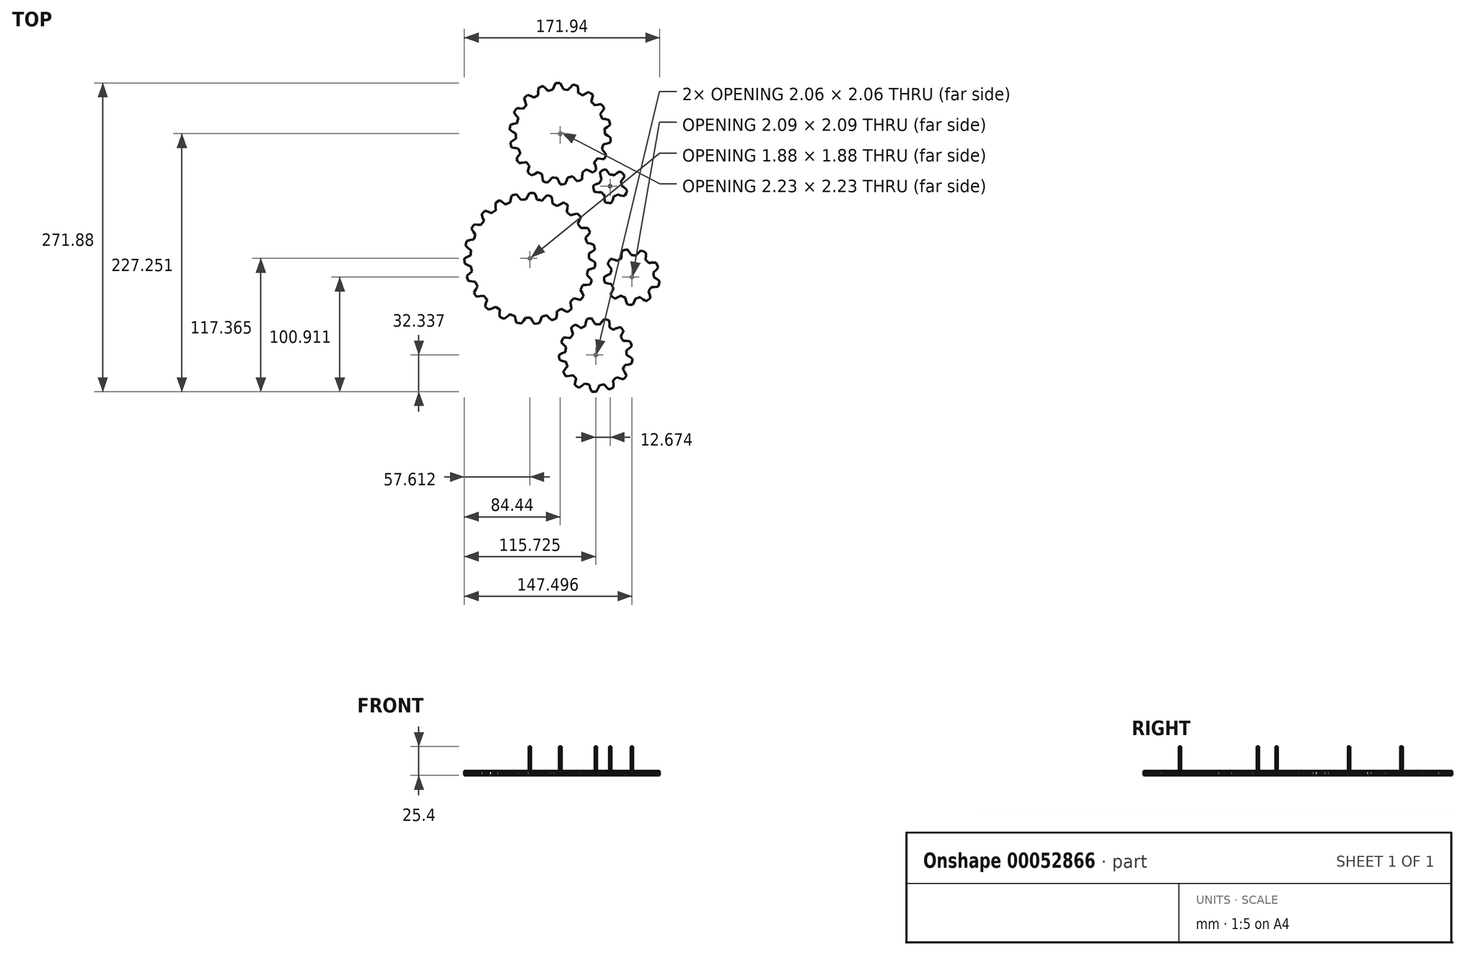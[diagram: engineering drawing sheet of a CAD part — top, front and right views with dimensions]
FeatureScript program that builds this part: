
annotation { "Feature Type Name" : "Feature", "Feature Type Description" : "" }
export const myFeature = defineFeature(function(context is Context, id is Id, definition is map)
    precondition{}
    {
        {
            var Q0;
            Q0=qCreatedBy(makeId("Top.planeOp"),FACE);
            var sketch = newSketch(context, id + "F0", { "sketchPlane" : qUnion([Q0])});
            skLineSegment(sketch, "E0", {"start": v(23.91, -18.64) * mm, "end": v(23.86, -16.49) * mm});
            skLineSegment(sketch, "E1", {"start": v(23.86, -16.49) * mm, "end": v(23.77, -15) * mm});
            skLineSegment(sketch, "E2", {"start": v(23.77, -15) * mm, "end": v(23.72, -14.33) * mm});
            skLineSegment(sketch, "E3", {"start": v(23.72, -14.33) * mm, "end": v(24.54, -13.82) * mm});
            skLineSegment(sketch, "E4", {"start": v(24.54, -13.82) * mm, "end": v(26.32, -12.65) * mm});
            skLineSegment(sketch, "E5", {"start": v(26.32, -12.65) * mm, "end": v(28.84, -10.83) * mm});
            skLineSegment(sketch, "E6", {"start": v(28.84, -10.83) * mm, "end": v(28.51, -8.7) * mm});
            skLineSegment(sketch, "E7", {"start": v(28.51, -8.7) * mm, "end": v(28.25, -7.25) * mm});
            skLineSegment(sketch, "E8", {"start": v(28.25, -7.25) * mm, "end": v(28.15, -6.77) * mm});
            skLineSegment(sketch, "E9", {"start": v(28.15, -6.77) * mm, "end": v(28.11, -6.6) * mm});
            skLineSegment(sketch, "E10", {"start": v(28.11, -6.6) * mm, "end": v(25.07, -5.56) * mm});
            skLineSegment(sketch, "E11", {"start": v(25.07, -5.56) * mm, "end": v(22.97, -4.95) * mm});
            skLineSegment(sketch, "E12", {"start": v(22.97, -4.95) * mm, "end": v(22.02, -4.7) * mm});
            skLineSegment(sketch, "E13", {"start": v(22.02, -4.7) * mm, "end": v(21.8, -3.9) * mm});
            skLineSegment(sketch, "E14", {"start": v(21.8, -3.9) * mm, "end": v(21.36, -2.5) * mm});
            skLineSegment(sketch, "E15", {"start": v(21.36, -2.5) * mm, "end": v(20.88, -1.09) * mm});
            skLineSegment(sketch, "E16", {"start": v(20.88, -1.09) * mm, "end": v(20.65, -0.46) * mm});
            skLineSegment(sketch, "E17", {"start": v(20.65, -0.46) * mm, "end": v(22.68, 1.86) * mm});
            skLineSegment(sketch, "E18", {"start": v(22.68, 1.86) * mm, "end": v(24.04, 3.53) * mm});
            skLineSegment(sketch, "E19", {"start": v(24.04, 3.53) * mm, "end": v(24.62, 4.3) * mm});
            skLineSegment(sketch, "E20", {"start": v(24.62, 4.3) * mm, "end": v(23.74, 6.27) * mm});
            skLineSegment(sketch, "E21", {"start": v(23.74, 6.27) * mm, "end": v(22.76, 8.18) * mm});
            skLineSegment(sketch, "E22", {"start": v(22.76, 8.18) * mm, "end": v(21.77, 8.26) * mm});
            skLineSegment(sketch, "E23", {"start": v(21.77, 8.26) * mm, "end": v(19.56, 8.35) * mm});
            skLineSegment(sketch, "E24", {"start": v(19.56, 8.35) * mm, "end": v(16.4, 8.36) * mm});
            skLineSegment(sketch, "E25", {"start": v(16.4, 8.36) * mm, "end": v(16.32, 8.48) * mm});
            skLineSegment(sketch, "E26", {"start": v(16.32, 8.48) * mm, "end": v(15.16, 10.3) * mm});
            skLineSegment(sketch, "E27", {"start": v(15.16, 10.3) * mm, "end": v(13.92, 12.06) * mm});
            skLineSegment(sketch, "E28", {"start": v(13.92, 12.06) * mm, "end": v(15.25, 14.85) * mm});
            skLineSegment(sketch, "E29", {"start": v(15.25, 14.85) * mm, "end": v(16.46, 17.73) * mm});
            skLineSegment(sketch, "E30", {"start": v(16.46, 17.73) * mm, "end": v(16.35, 17.87) * mm});
            skLineSegment(sketch, "E31", {"start": v(16.35, 17.87) * mm, "end": v(16.04, 18.25) * mm});
            skLineSegment(sketch, "E32", {"start": v(16.04, 18.25) * mm, "end": v(14.09, 20.47) * mm});
            skLineSegment(sketch, "E33", {"start": v(14.09, 20.47) * mm, "end": v(13.63, 20.95) * mm});
            skLineSegment(sketch, "E34", {"start": v(13.63, 20.95) * mm, "end": v(10.5, 20.26) * mm});
            skLineSegment(sketch, "E35", {"start": v(10.5, 20.26) * mm, "end": v(7.44, 19.4) * mm});
            skLineSegment(sketch, "E36", {"start": v(7.44, 19.4) * mm, "end": v(6.84, 19.97) * mm});
            skLineSegment(sketch, "E37", {"start": v(6.84, 19.97) * mm, "end": v(4.6, 21.9) * mm});
            skLineSegment(sketch, "E38", {"start": v(4.6, 21.9) * mm, "end": v(4.06, 22.31) * mm});
            skLineSegment(sketch, "E39", {"start": v(4.06, 22.31) * mm, "end": v(4.6, 25.37) * mm});
            skLineSegment(sketch, "E40", {"start": v(4.6, 25.37) * mm, "end": v(4.99, 28.45) * mm});
            skLineSegment(sketch, "E41", {"start": v(4.99, 28.45) * mm, "end": v(3.88, 29.23) * mm});
            skLineSegment(sketch, "E42", {"start": v(3.88, 29.23) * mm, "end": v(1.97, 30.46) * mm});
            skLineSegment(sketch, "E43", {"start": v(1.97, 30.46) * mm, "end": v(1.4, 30.8) * mm});
            skLineSegment(sketch, "E44", {"start": v(1.4, 30.8) * mm, "end": v(-1.44, 29.29) * mm});
            skLineSegment(sketch, "E45", {"start": v(-1.44, 29.29) * mm, "end": v(-3.31, 28.18) * mm});
            skLineSegment(sketch, "E46", {"start": v(-3.31, 28.18) * mm, "end": v(-4.15, 27.65) * mm});
            skLineSegment(sketch, "E47", {"start": v(-4.15, 27.65) * mm, "end": v(-4.88, 28.02) * mm});
            skLineSegment(sketch, "E48", {"start": v(-4.88, 28.02) * mm, "end": v(-6.21, 28.67) * mm});
            skLineSegment(sketch, "E49", {"start": v(-6.21, 28.67) * mm, "end": v(-8, 29.48) * mm});
            skLineSegment(sketch, "E50", {"start": v(-8, 29.48) * mm, "end": v(-8.18, 29.55) * mm});
            skLineSegment(sketch, "E51", {"start": v(-8.18, 29.55) * mm, "end": v(-8.5, 32.6) * mm});
            skLineSegment(sketch, "E52", {"start": v(-8.5, 32.6) * mm, "end": v(-8.78, 34.74) * mm});
            skLineSegment(sketch, "E53", {"start": v(-8.78, 34.74) * mm, "end": v(-8.95, 35.7) * mm});
            skLineSegment(sketch, "E54", {"start": v(-8.95, 35.7) * mm, "end": v(-10.98, 36.39) * mm});
            skLineSegment(sketch, "E55", {"start": v(-10.98, 36.39) * mm, "end": v(-13.05, 36.98) * mm});
            skLineSegment(sketch, "E56", {"start": v(-13.05, 36.98) * mm, "end": v(-15.36, 34.76) * mm});
            skLineSegment(sketch, "E57", {"start": v(-15.36, 34.76) * mm, "end": v(-17.53, 32.45) * mm});
            skLineSegment(sketch, "E58", {"start": v(-17.53, 32.45) * mm, "end": v(-17.67, 32.48) * mm});
            skLineSegment(sketch, "E59", {"start": v(-17.67, 32.48) * mm, "end": v(-17.85, 32.52) * mm});
            skLineSegment(sketch, "E60", {"start": v(-17.85, 32.52) * mm, "end": v(-19.79, 32.87) * mm});
            skLineSegment(sketch, "E61", {"start": v(-19.79, 32.87) * mm, "end": v(-21.26, 33.08) * mm});
            skLineSegment(sketch, "E62", {"start": v(-21.26, 33.08) * mm, "end": v(-21.92, 33.17) * mm});
            skLineSegment(sketch, "E63", {"start": v(-21.92, 33.17) * mm, "end": v(-22.26, 34.07) * mm});
            skLineSegment(sketch, "E64", {"start": v(-22.26, 34.07) * mm, "end": v(-23.05, 36.05) * mm});
            skLineSegment(sketch, "E65", {"start": v(-23.05, 36.05) * mm, "end": v(-24.33, 38.89) * mm});
            skLineSegment(sketch, "E66", {"start": v(-24.33, 38.89) * mm, "end": v(-26.47, 39) * mm});
            skLineSegment(sketch, "E67", {"start": v(-26.47, 39) * mm, "end": v(-27.95, 39.03) * mm});
            skLineSegment(sketch, "E68", {"start": v(-27.95, 39.03) * mm, "end": v(-28.62, 39.03) * mm});
            skLineSegment(sketch, "E69", {"start": v(-28.62, 39.03) * mm, "end": v(-30.25, 36.25) * mm});
            skLineSegment(sketch, "E70", {"start": v(-30.25, 36.25) * mm, "end": v(-31.72, 33.44) * mm});
            skLineSegment(sketch, "E71", {"start": v(-31.72, 33.44) * mm, "end": v(-34, 33.25) * mm});
            skLineSegment(sketch, "E72", {"start": v(-34, 33.25) * mm, "end": v(-36.15, 32.98) * mm});
            skLineSegment(sketch, "E73", {"start": v(-36.15, 32.98) * mm, "end": v(-36.71, 33.75) * mm});
            skLineSegment(sketch, "E74", {"start": v(-36.71, 33.75) * mm, "end": v(-38, 35.43) * mm});
            skLineSegment(sketch, "E75", {"start": v(-38, 35.43) * mm, "end": v(-39.36, 37.1) * mm});
            skLineSegment(sketch, "E76", {"start": v(-39.36, 37.1) * mm, "end": v(-40, 37.85) * mm});
            skLineSegment(sketch, "E77", {"start": v(-40, 37.85) * mm, "end": v(-42.1, 37.36) * mm});
            skLineSegment(sketch, "E78", {"start": v(-42.1, 37.36) * mm, "end": v(-43.52, 36.99) * mm});
            skLineSegment(sketch, "E79", {"start": v(-43.52, 36.99) * mm, "end": v(-44.17, 36.8) * mm});
            skLineSegment(sketch, "E80", {"start": v(-44.17, 36.8) * mm, "end": v(-44.44, 35.84) * mm});
            skLineSegment(sketch, "E81", {"start": v(-44.44, 35.84) * mm, "end": v(-45, 33.71) * mm});
            skLineSegment(sketch, "E82", {"start": v(-45, 33.71) * mm, "end": v(-45.64, 30.6) * mm});
            skLineSegment(sketch, "E83", {"start": v(-45.64, 30.6) * mm, "end": v(-45.96, 30.5) * mm});
            skLineSegment(sketch, "E84", {"start": v(-45.96, 30.5) * mm, "end": v(-46.42, 30.33) * mm});
            skLineSegment(sketch, "E85", {"start": v(-46.42, 30.33) * mm, "end": v(-48.53, 29.5) * mm});
            skLineSegment(sketch, "E86", {"start": v(-48.53, 29.5) * mm, "end": v(-49.78, 28.94) * mm});
            skLineSegment(sketch, "E87", {"start": v(-49.78, 28.94) * mm, "end": v(-50.53, 29.54) * mm});
            skLineSegment(sketch, "E88", {"start": v(-50.53, 29.54) * mm, "end": v(-52.24, 30.82) * mm});
            skLineSegment(sketch, "E89", {"start": v(-52.24, 30.82) * mm, "end": v(-54.8, 32.58) * mm});
            skLineSegment(sketch, "E90", {"start": v(-54.8, 32.58) * mm, "end": v(-55.4, 32.27) * mm});
            skLineSegment(sketch, "E91", {"start": v(-55.4, 32.27) * mm, "end": v(-57.97, 30.82) * mm});
            skLineSegment(sketch, "E92", {"start": v(-57.97, 30.82) * mm, "end": v(-58.39, 30.57) * mm});
            skLineSegment(sketch, "E93", {"start": v(-58.39, 30.57) * mm, "end": v(-58.54, 30.47) * mm});
            skLineSegment(sketch, "E94", {"start": v(-58.54, 30.47) * mm, "end": v(-58.5, 27.25) * mm});
            skLineSegment(sketch, "E95", {"start": v(-58.5, 27.25) * mm, "end": v(-58.44, 26.1) * mm});
            skLineSegment(sketch, "E96", {"start": v(-58.44, 26.1) * mm, "end": v(-58.28, 24.09) * mm});
            skLineSegment(sketch, "E97", {"start": v(-58.28, 24.09) * mm, "end": v(-59.5, 23.21) * mm});
            skLineSegment(sketch, "E98", {"start": v(-59.5, 23.21) * mm, "end": v(-61.3, 21.8) * mm});
            skLineSegment(sketch, "E99", {"start": v(-61.3, 21.8) * mm, "end": v(-61.67, 21.5) * mm});
            skLineSegment(sketch, "E100", {"start": v(-61.67, 21.5) * mm, "end": v(-61.81, 21.38) * mm});
            skLineSegment(sketch, "E101", {"start": v(-61.81, 21.38) * mm, "end": v(-64.68, 22.51) * mm});
            skLineSegment(sketch, "E102", {"start": v(-64.68, 22.51) * mm, "end": v(-67.63, 23.52) * mm});
            skLineSegment(sketch, "E103", {"start": v(-67.63, 23.52) * mm, "end": v(-69.18, 22.04) * mm});
            skLineSegment(sketch, "E104", {"start": v(-69.18, 22.04) * mm, "end": v(-70.66, 20.48) * mm});
            skLineSegment(sketch, "E105", {"start": v(-70.66, 20.48) * mm, "end": v(-70.4, 19.52) * mm});
            skLineSegment(sketch, "E106", {"start": v(-70.4, 19.52) * mm, "end": v(-69.75, 17.4) * mm});
            skLineSegment(sketch, "E107", {"start": v(-69.75, 17.4) * mm, "end": v(-69.05, 15.34) * mm});
            skLineSegment(sketch, "E108", {"start": v(-69.05, 15.34) * mm, "end": v(-68.7, 14.42) * mm});
            skLineSegment(sketch, "E109", {"start": v(-68.7, 14.42) * mm, "end": v(-70.13, 12.6) * mm});
            skLineSegment(sketch, "E110", {"start": v(-70.13, 12.6) * mm, "end": v(-71.38, 10.85) * mm});
            skLineSegment(sketch, "E111", {"start": v(-71.38, 10.85) * mm, "end": v(-72.34, 10.97) * mm});
            skLineSegment(sketch, "E112", {"start": v(-72.34, 10.97) * mm, "end": v(-74.44, 11.17) * mm});
            skLineSegment(sketch, "E113", {"start": v(-74.44, 11.17) * mm, "end": v(-77.57, 11.36) * mm});
            skLineSegment(sketch, "E114", {"start": v(-77.57, 11.36) * mm, "end": v(-77.66, 11.2) * mm});
            skLineSegment(sketch, "E115", {"start": v(-77.66, 11.2) * mm, "end": v(-79.03, 8.81) * mm});
            skLineSegment(sketch, "E116", {"start": v(-79.03, 8.81) * mm, "end": v(-79.65, 7.6) * mm});
            skLineSegment(sketch, "E117", {"start": v(-79.65, 7.6) * mm, "end": v(-79.13, 6.74) * mm});
            skLineSegment(sketch, "E118", {"start": v(-79.13, 6.74) * mm, "end": v(-77.96, 4.89) * mm});
            skLineSegment(sketch, "E119", {"start": v(-77.96, 4.89) * mm, "end": v(-76.13, 2.29) * mm});
            skLineSegment(sketch, "E120", {"start": v(-76.13, 2.29) * mm, "end": v(-76.46, 1.54) * mm});
            skLineSegment(sketch, "E121", {"start": v(-76.46, 1.54) * mm, "end": v(-77, 0.16) * mm});
            skLineSegment(sketch, "E122", {"start": v(-77, 0.16) * mm, "end": v(-77.52, -1.23) * mm});
            skLineSegment(sketch, "E123", {"start": v(-77.52, -1.23) * mm, "end": v(-77.74, -1.86) * mm});
            skLineSegment(sketch, "E124", {"start": v(-77.74, -1.86) * mm, "end": v(-80.8, -2.38) * mm});
            skLineSegment(sketch, "E125", {"start": v(-80.8, -2.38) * mm, "end": v(-83.83, -3.05) * mm});
            skLineSegment(sketch, "E126", {"start": v(-83.83, -3.05) * mm, "end": v(-84, -3.7) * mm});
            skLineSegment(sketch, "E127", {"start": v(-84, -3.7) * mm, "end": v(-84.37, -5.13) * mm});
            skLineSegment(sketch, "E128", {"start": v(-84.37, -5.13) * mm, "end": v(-84.8, -7.04) * mm});
            skLineSegment(sketch, "E129", {"start": v(-84.8, -7.04) * mm, "end": v(-84.84, -7.23) * mm});
            skLineSegment(sketch, "E130", {"start": v(-84.84, -7.23) * mm, "end": v(-82.45, -9.38) * mm});
            skLineSegment(sketch, "E131", {"start": v(-82.45, -9.38) * mm, "end": v(-80, -11.39) * mm});
            skLineSegment(sketch, "E132", {"start": v(-80, -11.39) * mm, "end": v(-80.27, -13.67) * mm});
            skLineSegment(sketch, "E133", {"start": v(-80.27, -13.67) * mm, "end": v(-80.43, -15.82) * mm});
            skLineSegment(sketch, "E134", {"start": v(-80.43, -15.82) * mm, "end": v(-81.3, -16.22) * mm});
            skLineSegment(sketch, "E135", {"start": v(-81.3, -16.22) * mm, "end": v(-83.2, -17.14) * mm});
            skLineSegment(sketch, "E136", {"start": v(-83.2, -17.14) * mm, "end": v(-85.97, -18.61) * mm});
            skLineSegment(sketch, "E137", {"start": v(-85.97, -18.61) * mm, "end": v(-85.9, -21.54) * mm});
            skLineSegment(sketch, "E138", {"start": v(-85.9, -21.54) * mm, "end": v(-85.8, -22.9) * mm});
            skLineSegment(sketch, "E139", {"start": v(-85.8, -22.9) * mm, "end": v(-82.95, -24.34) * mm});
            skLineSegment(sketch, "E140", {"start": v(-82.95, -24.34) * mm, "end": v(-80.03, -25.61) * mm});
            skLineSegment(sketch, "E141", {"start": v(-80.03, -25.61) * mm, "end": v(-79.93, -26.42) * mm});
            skLineSegment(sketch, "E142", {"start": v(-79.93, -26.42) * mm, "end": v(-79.4, -29.34) * mm});
            skLineSegment(sketch, "E143", {"start": v(-79.4, -29.34) * mm, "end": v(-79.25, -30) * mm});
            skLineSegment(sketch, "E144", {"start": v(-79.25, -30) * mm, "end": v(-81.6, -32.02) * mm});
            skLineSegment(sketch, "E145", {"start": v(-81.6, -32.02) * mm, "end": v(-83.15, -33.49) * mm});
            skLineSegment(sketch, "E146", {"start": v(-83.15, -33.49) * mm, "end": v(-83.84, -34.17) * mm});
            skLineSegment(sketch, "E147", {"start": v(-83.84, -34.17) * mm, "end": v(-83.23, -36.23) * mm});
            skLineSegment(sketch, "E148", {"start": v(-83.23, -36.23) * mm, "end": v(-82.55, -38.27) * mm});
            skLineSegment(sketch, "E149", {"start": v(-82.55, -38.27) * mm, "end": v(-81.56, -38.47) * mm});
            skLineSegment(sketch, "E150", {"start": v(-81.56, -38.47) * mm, "end": v(-79.38, -38.87) * mm});
            skLineSegment(sketch, "E151", {"start": v(-79.38, -38.87) * mm, "end": v(-77.23, -39.2) * mm});
            skLineSegment(sketch, "E152", {"start": v(-77.23, -39.2) * mm, "end": v(-76.25, -39.31) * mm});
            skLineSegment(sketch, "E153", {"start": v(-76.25, -39.31) * mm, "end": v(-75.3, -41.4) * mm});
            skLineSegment(sketch, "E154", {"start": v(-75.3, -41.4) * mm, "end": v(-74.31, -43.32) * mm});
            skLineSegment(sketch, "E155", {"start": v(-74.31, -43.32) * mm, "end": v(-74.85, -44.12) * mm});
            skLineSegment(sketch, "E156", {"start": v(-74.85, -44.12) * mm, "end": v(-76, -45.9) * mm});
            skLineSegment(sketch, "E157", {"start": v(-76, -45.9) * mm, "end": v(-77.6, -48.59) * mm});
            skLineSegment(sketch, "E158", {"start": v(-77.6, -48.59) * mm, "end": v(-76.44, -50.4) * mm});
            skLineSegment(sketch, "E159", {"start": v(-76.44, -50.4) * mm, "end": v(-75.61, -51.62) * mm});
            skLineSegment(sketch, "E160", {"start": v(-75.61, -51.62) * mm, "end": v(-75.22, -52.16) * mm});
            skLineSegment(sketch, "E161", {"start": v(-75.22, -52.16) * mm, "end": v(-74.22, -52.1) * mm});
            skLineSegment(sketch, "E162", {"start": v(-74.22, -52.1) * mm, "end": v(-72.03, -51.9) * mm});
            skLineSegment(sketch, "E163", {"start": v(-72.03, -51.9) * mm, "end": v(-68.88, -51.47) * mm});
            skLineSegment(sketch, "E164", {"start": v(-68.88, -51.47) * mm, "end": v(-68.8, -51.59) * mm});
            skLineSegment(sketch, "E165", {"start": v(-68.8, -51.59) * mm, "end": v(-68.37, -52.1) * mm});
            skLineSegment(sketch, "E166", {"start": v(-68.37, -52.1) * mm, "end": v(-66.87, -53.82) * mm});
            skLineSegment(sketch, "E167", {"start": v(-66.87, -53.82) * mm, "end": v(-65.93, -54.81) * mm});
            skLineSegment(sketch, "E168", {"start": v(-65.93, -54.81) * mm, "end": v(-66.24, -55.72) * mm});
            skLineSegment(sketch, "E169", {"start": v(-66.24, -55.72) * mm, "end": v(-66.88, -57.76) * mm});
            skLineSegment(sketch, "E170", {"start": v(-66.88, -57.76) * mm, "end": v(-67.68, -60.76) * mm});
            skLineSegment(sketch, "E171", {"start": v(-67.68, -60.76) * mm, "end": v(-67.2, -61.23) * mm});
            skLineSegment(sketch, "E172", {"start": v(-67.2, -61.23) * mm, "end": v(-64.97, -63.17) * mm});
            skLineSegment(sketch, "E173", {"start": v(-64.97, -63.17) * mm, "end": v(-64.44, -63.58) * mm});
            skLineSegment(sketch, "E174", {"start": v(-64.44, -63.58) * mm, "end": v(-61.43, -62.47) * mm});
            skLineSegment(sketch, "E175", {"start": v(-61.43, -62.47) * mm, "end": v(-59.41, -61.62) * mm});
            skLineSegment(sketch, "E176", {"start": v(-59.41, -61.62) * mm, "end": v(-58.51, -61.2) * mm});
            skLineSegment(sketch, "E177", {"start": v(-58.51, -61.2) * mm, "end": v(-57.85, -61.68) * mm});
            skLineSegment(sketch, "E178", {"start": v(-57.85, -61.68) * mm, "end": v(-55.36, -63.3) * mm});
            skLineSegment(sketch, "E179", {"start": v(-55.36, -63.3) * mm, "end": v(-54.78, -63.63) * mm});
            skLineSegment(sketch, "E180", {"start": v(-54.78, -63.63) * mm, "end": v(-54.9, -66.72) * mm});
            skLineSegment(sketch, "E181", {"start": v(-54.9, -66.72) * mm, "end": v(-54.89, -68.86) * mm});
            skLineSegment(sketch, "E182", {"start": v(-54.89, -68.86) * mm, "end": v(-54.86, -69.84) * mm});
            skLineSegment(sketch, "E183", {"start": v(-54.86, -69.84) * mm, "end": v(-52.94, -70.8) * mm});
            skLineSegment(sketch, "E184", {"start": v(-52.94, -70.8) * mm, "end": v(-50.98, -71.68) * mm});
            skLineSegment(sketch, "E185", {"start": v(-50.98, -71.68) * mm, "end": v(-50.16, -71.1) * mm});
            skLineSegment(sketch, "E186", {"start": v(-50.16, -71.1) * mm, "end": v(-48.38, -69.78) * mm});
            skLineSegment(sketch, "E187", {"start": v(-48.38, -69.78) * mm, "end": v(-46.68, -68.44) * mm});
            skLineSegment(sketch, "E188", {"start": v(-46.68, -68.44) * mm, "end": v(-45.92, -67.8) * mm});
            skLineSegment(sketch, "E189", {"start": v(-45.92, -67.8) * mm, "end": v(-43.74, -68.53) * mm});
            skLineSegment(sketch, "E190", {"start": v(-43.74, -68.53) * mm, "end": v(-41.67, -69.12) * mm});
            skLineSegment(sketch, "E191", {"start": v(-41.67, -69.12) * mm, "end": v(-41.46, -70.06) * mm});
            skLineSegment(sketch, "E192", {"start": v(-41.46, -70.06) * mm, "end": v(-40.94, -72.11) * mm});
            skLineSegment(sketch, "E193", {"start": v(-40.94, -72.11) * mm, "end": v(-40.06, -75.12) * mm});
            skLineSegment(sketch, "E194", {"start": v(-40.06, -75.12) * mm, "end": v(-39.88, -75.16) * mm});
            skLineSegment(sketch, "E195", {"start": v(-39.88, -75.16) * mm, "end": v(-37.17, -75.64) * mm});
            skLineSegment(sketch, "E196", {"start": v(-37.17, -75.64) * mm, "end": v(-35.83, -75.82) * mm});
            skLineSegment(sketch, "E197", {"start": v(-35.83, -75.82) * mm, "end": v(-33.84, -73.31) * mm});
            skLineSegment(sketch, "E198", {"start": v(-33.84, -73.31) * mm, "end": v(-32, -70.7) * mm});
            skLineSegment(sketch, "E199", {"start": v(-32, -70.7) * mm, "end": v(-31.19, -70.77) * mm});
            skLineSegment(sketch, "E200", {"start": v(-31.19, -70.77) * mm, "end": v(-28.22, -70.85) * mm});
            skLineSegment(sketch, "E201", {"start": v(-28.22, -70.85) * mm, "end": v(-27.55, -70.83) * mm});
            skLineSegment(sketch, "E202", {"start": v(-27.55, -70.83) * mm, "end": v(-26.04, -73.53) * mm});
            skLineSegment(sketch, "E203", {"start": v(-26.04, -73.53) * mm, "end": v(-24.93, -75.36) * mm});
            skLineSegment(sketch, "E204", {"start": v(-24.93, -75.36) * mm, "end": v(-24.4, -76.18) * mm});
            skLineSegment(sketch, "E205", {"start": v(-24.4, -76.18) * mm, "end": v(-22.26, -76) * mm});
            skLineSegment(sketch, "E206", {"start": v(-22.26, -76) * mm, "end": v(-20.13, -75.74) * mm});
            skLineSegment(sketch, "E207", {"start": v(-20.13, -75.74) * mm, "end": v(-19.72, -74.82) * mm});
            skLineSegment(sketch, "E208", {"start": v(-19.72, -74.82) * mm, "end": v(-18.88, -72.77) * mm});
            skLineSegment(sketch, "E209", {"start": v(-18.88, -72.77) * mm, "end": v(-17.81, -69.8) * mm});
            skLineSegment(sketch, "E210", {"start": v(-17.81, -69.8) * mm, "end": v(-15.57, -69.29) * mm});
            skLineSegment(sketch, "E211", {"start": v(-15.57, -69.29) * mm, "end": v(-13.5, -68.71) * mm});
            skLineSegment(sketch, "E212", {"start": v(-13.5, -68.71) * mm, "end": v(-12.82, -69.41) * mm});
            skLineSegment(sketch, "E213", {"start": v(-12.82, -69.41) * mm, "end": v(-11.32, -70.9) * mm});
            skLineSegment(sketch, "E214", {"start": v(-11.32, -70.9) * mm, "end": v(-9.01, -73) * mm});
            skLineSegment(sketch, "E215", {"start": v(-9.01, -73) * mm, "end": v(-8.38, -72.79) * mm});
            skLineSegment(sketch, "E216", {"start": v(-8.38, -72.79) * mm, "end": v(-5.63, -71.7) * mm});
            skLineSegment(sketch, "E217", {"start": v(-5.63, -71.7) * mm, "end": v(-5.02, -71.42) * mm});
            skLineSegment(sketch, "E218", {"start": v(-5.02, -71.42) * mm, "end": v(-4.63, -68.24) * mm});
            skLineSegment(sketch, "E219", {"start": v(-4.63, -68.24) * mm, "end": v(-4.46, -66.05) * mm});
            skLineSegment(sketch, "E220", {"start": v(-4.46, -66.05) * mm, "end": v(-4.4, -65.06) * mm});
            skLineSegment(sketch, "E221", {"start": v(-4.4, -65.06) * mm, "end": v(-4.28, -65) * mm});
            skLineSegment(sketch, "E222", {"start": v(-4.28, -65) * mm, "end": v(-2.39, -63.97) * mm});
            skLineSegment(sketch, "E223", {"start": v(-2.39, -63.97) * mm, "end": v(-1.1, -63.22) * mm});
            skLineSegment(sketch, "E224", {"start": v(-1.1, -63.22) * mm, "end": v(-0.54, -62.86) * mm});
            skLineSegment(sketch, "E225", {"start": v(-0.54, -62.86) * mm, "end": v(2.15, -64.38) * mm});
            skLineSegment(sketch, "E226", {"start": v(2.15, -64.38) * mm, "end": v(4.05, -65.35) * mm});
            skLineSegment(sketch, "E227", {"start": v(4.05, -65.35) * mm, "end": v(4.93, -65.78) * mm});
            skLineSegment(sketch, "E228", {"start": v(4.93, -65.78) * mm, "end": v(5.48, -65.39) * mm});
            skLineSegment(sketch, "E229", {"start": v(5.48, -65.39) * mm, "end": v(6.67, -64.5) * mm});
            skLineSegment(sketch, "E230", {"start": v(6.67, -64.5) * mm, "end": v(8.36, -63.18) * mm});
            skLineSegment(sketch, "E231", {"start": v(8.36, -63.18) * mm, "end": v(8.22, -62.18) * mm});
            skLineSegment(sketch, "E232", {"start": v(8.22, -62.18) * mm, "end": v(7.86, -60) * mm});
            skLineSegment(sketch, "E233", {"start": v(7.86, -60) * mm, "end": v(7.45, -57.86) * mm});
            skLineSegment(sketch, "E234", {"start": v(7.45, -57.86) * mm, "end": v(7.23, -56.9) * mm});
            skLineSegment(sketch, "E235", {"start": v(7.23, -56.9) * mm, "end": v(8.88, -55.3) * mm});
            skLineSegment(sketch, "E236", {"start": v(8.88, -55.3) * mm, "end": v(10.37, -53.73) * mm});
            skLineSegment(sketch, "E237", {"start": v(10.37, -53.73) * mm, "end": v(13.35, -54.46) * mm});
            skLineSegment(sketch, "E238", {"start": v(13.35, -54.46) * mm, "end": v(15.46, -54.9) * mm});
            skLineSegment(sketch, "E239", {"start": v(15.46, -54.9) * mm, "end": v(16.42, -55.07) * mm});
            skLineSegment(sketch, "E240", {"start": v(16.42, -55.07) * mm, "end": v(17.75, -53.38) * mm});
            skLineSegment(sketch, "E241", {"start": v(17.75, -53.38) * mm, "end": v(19, -51.64) * mm});
            skLineSegment(sketch, "E242", {"start": v(19, -51.64) * mm, "end": v(18.61, -50.71) * mm});
            skLineSegment(sketch, "E243", {"start": v(18.61, -50.71) * mm, "end": v(17.68, -48.7) * mm});
            skLineSegment(sketch, "E244", {"start": v(17.68, -48.7) * mm, "end": v(16.24, -45.9) * mm});
            skLineSegment(sketch, "E245", {"start": v(16.24, -45.9) * mm, "end": v(16.32, -45.77) * mm});
            skLineSegment(sketch, "E246", {"start": v(16.32, -45.77) * mm, "end": v(17.4, -43.9) * mm});
            skLineSegment(sketch, "E247", {"start": v(17.4, -43.9) * mm, "end": v(18.4, -42) * mm});
            skLineSegment(sketch, "E248", {"start": v(18.4, -42) * mm, "end": v(19.36, -41.98) * mm});
            skLineSegment(sketch, "E249", {"start": v(19.36, -41.98) * mm, "end": v(21.49, -41.9) * mm});
            skLineSegment(sketch, "E250", {"start": v(21.49, -41.9) * mm, "end": v(24.6, -41.66) * mm});
            skLineSegment(sketch, "E251", {"start": v(24.6, -41.66) * mm, "end": v(24.87, -41.04) * mm});
            skLineSegment(sketch, "E252", {"start": v(24.87, -41.04) * mm, "end": v(25.94, -38.3) * mm});
            skLineSegment(sketch, "E253", {"start": v(25.94, -38.3) * mm, "end": v(26.16, -37.65) * mm});
            skLineSegment(sketch, "E254", {"start": v(26.16, -37.65) * mm, "end": v(24.1, -35.2) * mm});
            skLineSegment(sketch, "E255", {"start": v(24.1, -35.2) * mm, "end": v(22.62, -33.58) * mm});
            skLineSegment(sketch, "E256", {"start": v(22.62, -33.58) * mm, "end": v(21.94, -32.87) * mm});
            skLineSegment(sketch, "E257", {"start": v(21.94, -32.87) * mm, "end": v(22.16, -32.08) * mm});
            skLineSegment(sketch, "E258", {"start": v(22.16, -32.08) * mm, "end": v(22.85, -29.2) * mm});
            skLineSegment(sketch, "E259", {"start": v(22.85, -29.2) * mm, "end": v(22.97, -28.54) * mm});
            skLineSegment(sketch, "E260", {"start": v(22.97, -28.54) * mm, "end": v(25.9, -27.6) * mm});
            skLineSegment(sketch, "E261", {"start": v(25.9, -27.6) * mm, "end": v(27.93, -26.88) * mm});
            skLineSegment(sketch, "E262", {"start": v(27.93, -26.88) * mm, "end": v(28.83, -26.53) * mm});
            skLineSegment(sketch, "E263", {"start": v(28.83, -26.53) * mm, "end": v(29.1, -24.4) * mm});
            skLineSegment(sketch, "E264", {"start": v(29.1, -24.4) * mm, "end": v(29.26, -22.25) * mm});
            skLineSegment(sketch, "E265", {"start": v(29.26, -22.25) * mm, "end": v(28.45, -21.67) * mm});
            skLineSegment(sketch, "E266", {"start": v(28.45, -21.67) * mm, "end": v(26.6, -20.44) * mm});
            skLineSegment(sketch, "E267", {"start": v(26.6, -20.44) * mm, "end": v(23.91, -18.79) * mm});
            skLineSegment(sketch, "E268", {"start": v(23.91, -18.79) * mm, "end": v(23.91, -18.64) * mm});
            skLineSegment(sketch, "E269", {"start": v(-40.68, 91.45) * mm, "end": v(-43.38, 93.06) * mm});
            skLineSegment(sketch, "E270", {"start": v(-43.38, 93.06) * mm, "end": v(-45.2, 94.29) * mm});
            skLineSegment(sketch, "E271", {"start": v(-45.2, 94.29) * mm, "end": v(-46, 94.88) * mm});
            skLineSegment(sketch, "E272", {"start": v(-46, 94.88) * mm, "end": v(-45.78, 96.99) * mm});
            skLineSegment(sketch, "E273", {"start": v(-45.78, 96.99) * mm, "end": v(-45.47, 99.09) * mm});
            skLineSegment(sketch, "E274", {"start": v(-45.47, 99.09) * mm, "end": v(-44.54, 99.4) * mm});
            skLineSegment(sketch, "E275", {"start": v(-44.54, 99.4) * mm, "end": v(-42.5, 100.02) * mm});
            skLineSegment(sketch, "E276", {"start": v(-42.5, 100.02) * mm, "end": v(-39.53, 100.76) * mm});
            skLineSegment(sketch, "E277", {"start": v(-39.53, 100.76) * mm, "end": v(-39.5, 100.93) * mm});
            skLineSegment(sketch, "E278", {"start": v(-39.5, 100.93) * mm, "end": v(-39.37, 101.38) * mm});
            skLineSegment(sketch, "E279", {"start": v(-39.37, 101.38) * mm, "end": v(-38.99, 102.75) * mm});
            skLineSegment(sketch, "E280", {"start": v(-38.99, 102.75) * mm, "end": v(-38.34, 104.7) * mm});
            skLineSegment(sketch, "E281", {"start": v(-38.34, 104.7) * mm, "end": v(-38.29, 104.84) * mm});
            skLineSegment(sketch, "E282", {"start": v(-38.29, 104.84) * mm, "end": v(-40.27, 107.27) * mm});
            skLineSegment(sketch, "E283", {"start": v(-40.27, 107.27) * mm, "end": v(-41.55, 109.05) * mm});
            skLineSegment(sketch, "E284", {"start": v(-41.55, 109.05) * mm, "end": v(-42.1, 109.88) * mm});
            skLineSegment(sketch, "E285", {"start": v(-42.1, 109.88) * mm, "end": v(-41.83, 110.49) * mm});
            skLineSegment(sketch, "E286", {"start": v(-41.83, 110.49) * mm, "end": v(-41.18, 111.79) * mm});
            skLineSegment(sketch, "E287", {"start": v(-41.18, 111.79) * mm, "end": v(-40.49, 113.08) * mm});
            skLineSegment(sketch, "E288", {"start": v(-40.49, 113.08) * mm, "end": v(-40.16, 113.65) * mm});
            skLineSegment(sketch, "E289", {"start": v(-40.16, 113.65) * mm, "end": v(-39.18, 113.63) * mm});
            skLineSegment(sketch, "E290", {"start": v(-39.18, 113.63) * mm, "end": v(-37.05, 113.5) * mm});
            skLineSegment(sketch, "E291", {"start": v(-37.05, 113.5) * mm, "end": v(-34.02, 113.18) * mm});
            skLineSegment(sketch, "E292", {"start": v(-34.02, 113.18) * mm, "end": v(-32.81, 114.86) * mm});
            skLineSegment(sketch, "E293", {"start": v(-32.81, 114.86) * mm, "end": v(-31.64, 116.34) * mm});
            skLineSegment(sketch, "E294", {"start": v(-31.64, 116.34) * mm, "end": v(-31.43, 116.58) * mm});
            skLineSegment(sketch, "E295", {"start": v(-31.43, 116.58) * mm, "end": v(-32.47, 119.56) * mm});
            skLineSegment(sketch, "E296", {"start": v(-32.47, 119.56) * mm, "end": v(-33.3, 122.64) * mm});
            skLineSegment(sketch, "E297", {"start": v(-33.3, 122.64) * mm, "end": v(-32.84, 123.1) * mm});
            skLineSegment(sketch, "E298", {"start": v(-32.84, 123.1) * mm, "end": v(-31.78, 124.11) * mm});
            skLineSegment(sketch, "E299", {"start": v(-31.78, 124.11) * mm, "end": v(-30.19, 125.51) * mm});
            skLineSegment(sketch, "E300", {"start": v(-30.19, 125.51) * mm, "end": v(-29.28, 125.16) * mm});
            skLineSegment(sketch, "E301", {"start": v(-29.28, 125.16) * mm, "end": v(-27.32, 124.31) * mm});
            skLineSegment(sketch, "E302", {"start": v(-27.32, 124.31) * mm, "end": v(-25.42, 123.41) * mm});
            skLineSegment(sketch, "E303", {"start": v(-25.42, 123.41) * mm, "end": v(-24.57, 122.97) * mm});
            skLineSegment(sketch, "E304", {"start": v(-24.57, 122.97) * mm, "end": v(-23.5, 123.73) * mm});
            skLineSegment(sketch, "E305", {"start": v(-23.5, 123.73) * mm, "end": v(-21.66, 124.9) * mm});
            skLineSegment(sketch, "E306", {"start": v(-21.66, 124.9) * mm, "end": v(-20.98, 125.29) * mm});
            skLineSegment(sketch, "E307", {"start": v(-20.98, 125.29) * mm, "end": v(-21, 126.27) * mm});
            skLineSegment(sketch, "E308", {"start": v(-21, 126.27) * mm, "end": v(-20.98, 127.28) * mm});
            skLineSegment(sketch, "E309", {"start": v(-20.98, 127.28) * mm, "end": v(-20.94, 128.43) * mm});
            skLineSegment(sketch, "E310", {"start": v(-20.94, 128.43) * mm, "end": v(-20.79, 130.62) * mm});
            skLineSegment(sketch, "E311", {"start": v(-20.79, 130.62) * mm, "end": v(-20.68, 131.62) * mm});
            skLineSegment(sketch, "E312", {"start": v(-20.68, 131.62) * mm, "end": v(-18.74, 132.5) * mm});
            skLineSegment(sketch, "E313", {"start": v(-18.74, 132.5) * mm, "end": v(-16.94, 133.2) * mm});
            skLineSegment(sketch, "E314", {"start": v(-16.94, 133.2) * mm, "end": v(-16.76, 133.27) * mm});
            skLineSegment(sketch, "E315", {"start": v(-16.76, 133.27) * mm, "end": v(-14.48, 131.15) * mm});
            skLineSegment(sketch, "E316", {"start": v(-14.48, 131.15) * mm, "end": v(-13.68, 130.36) * mm});
            skLineSegment(sketch, "E317", {"start": v(-13.68, 130.36) * mm, "end": v(-12.35, 128.94) * mm});
            skLineSegment(sketch, "E318", {"start": v(-12.35, 128.94) * mm, "end": v(-11.73, 129.12) * mm});
            skLineSegment(sketch, "E319", {"start": v(-11.73, 129.12) * mm, "end": v(-10.36, 129.46) * mm});
            skLineSegment(sketch, "E320", {"start": v(-10.36, 129.46) * mm, "end": v(-8.97, 129.75) * mm});
            skLineSegment(sketch, "E321", {"start": v(-8.97, 129.75) * mm, "end": v(-8.2, 129.9) * mm});
            skLineSegment(sketch, "E322", {"start": v(-8.2, 129.9) * mm, "end": v(-7.07, 132.83) * mm});
            skLineSegment(sketch, "E323", {"start": v(-7.07, 132.83) * mm, "end": v(-6.18, 134.83) * mm});
            skLineSegment(sketch, "E324", {"start": v(-6.18, 134.83) * mm, "end": v(-5.73, 135.73) * mm});
            skLineSegment(sketch, "E325", {"start": v(-5.73, 135.73) * mm, "end": v(-3.62, 135.88) * mm});
            skLineSegment(sketch, "E326", {"start": v(-3.62, 135.88) * mm, "end": v(-1.5, 135.94) * mm});
            skLineSegment(sketch, "E327", {"start": v(-1.5, 135.94) * mm, "end": v(-0.07, 133.17) * mm});
            skLineSegment(sketch, "E328", {"start": v(-0.07, 133.17) * mm, "end": v(0.8, 131.25) * mm});
            skLineSegment(sketch, "E329", {"start": v(0.8, 131.25) * mm, "end": v(1.17, 130.37) * mm});
            skLineSegment(sketch, "E330", {"start": v(1.17, 130.37) * mm, "end": v(2.48, 130.27) * mm});
            skLineSegment(sketch, "E331", {"start": v(2.48, 130.27) * mm, "end": v(4.64, 129.98) * mm});
            skLineSegment(sketch, "E332", {"start": v(4.64, 129.98) * mm, "end": v(5.4, 129.84) * mm});
            skLineSegment(sketch, "E333", {"start": v(5.4, 129.84) * mm, "end": v(6.03, 130.6) * mm});
            skLineSegment(sketch, "E334", {"start": v(6.03, 130.6) * mm, "end": v(6.69, 131.37) * mm});
            skLineSegment(sketch, "E335", {"start": v(6.69, 131.37) * mm, "end": v(7.46, 132.22) * mm});
            skLineSegment(sketch, "E336", {"start": v(7.46, 132.22) * mm, "end": v(8.99, 133.8) * mm});
            skLineSegment(sketch, "E337", {"start": v(8.99, 133.8) * mm, "end": v(9.71, 134.5) * mm});
            skLineSegment(sketch, "E338", {"start": v(9.71, 134.5) * mm, "end": v(11.76, 133.93) * mm});
            skLineSegment(sketch, "E339", {"start": v(11.76, 133.93) * mm, "end": v(13.77, 133.24) * mm});
            skLineSegment(sketch, "E340", {"start": v(13.77, 133.24) * mm, "end": v(13.91, 132.27) * mm});
            skLineSegment(sketch, "E341", {"start": v(13.91, 132.27) * mm, "end": v(14.16, 130.15) * mm});
            skLineSegment(sketch, "E342", {"start": v(14.16, 130.15) * mm, "end": v(14.33, 128.05) * mm});
            skLineSegment(sketch, "E343", {"start": v(14.33, 128.05) * mm, "end": v(14.37, 127.1) * mm});
            skLineSegment(sketch, "E344", {"start": v(14.37, 127.1) * mm, "end": v(14.95, 126.83) * mm});
            skLineSegment(sketch, "E345", {"start": v(14.95, 126.83) * mm, "end": v(16.23, 126.2) * mm});
            skLineSegment(sketch, "E346", {"start": v(16.23, 126.2) * mm, "end": v(17.48, 125.54) * mm});
            skLineSegment(sketch, "E347", {"start": v(17.48, 125.54) * mm, "end": v(18.16, 125.15) * mm});
            skLineSegment(sketch, "E348", {"start": v(18.16, 125.15) * mm, "end": v(20.91, 126.68) * mm});
            skLineSegment(sketch, "E349", {"start": v(20.91, 126.68) * mm, "end": v(22.89, 127.64) * mm});
            skLineSegment(sketch, "E350", {"start": v(22.89, 127.64) * mm, "end": v(23.8, 128.04) * mm});
            skLineSegment(sketch, "E351", {"start": v(23.8, 128.04) * mm, "end": v(25.52, 126.8) * mm});
            skLineSegment(sketch, "E352", {"start": v(25.52, 126.8) * mm, "end": v(26.67, 125.9) * mm});
            skLineSegment(sketch, "E353", {"start": v(26.67, 125.9) * mm, "end": v(27.04, 125.59) * mm});
            skLineSegment(sketch, "E354", {"start": v(27.04, 125.59) * mm, "end": v(27.18, 125.47) * mm});
            skLineSegment(sketch, "E355", {"start": v(27.18, 125.47) * mm, "end": v(26.5, 122.44) * mm});
            skLineSegment(sketch, "E356", {"start": v(26.5, 122.44) * mm, "end": v(25.93, 120.4) * mm});
            skLineSegment(sketch, "E357", {"start": v(25.93, 120.4) * mm, "end": v(25.64, 119.5) * mm});
            skLineSegment(sketch, "E358", {"start": v(25.64, 119.5) * mm, "end": v(26.1, 119.05) * mm});
            skLineSegment(sketch, "E359", {"start": v(26.1, 119.05) * mm, "end": v(27.1, 118.02) * mm});
            skLineSegment(sketch, "E360", {"start": v(27.1, 118.02) * mm, "end": v(28.56, 116.37) * mm});
            skLineSegment(sketch, "E361", {"start": v(28.56, 116.37) * mm, "end": v(29.51, 116.55) * mm});
            skLineSegment(sketch, "E362", {"start": v(29.51, 116.55) * mm, "end": v(31.65, 116.87) * mm});
            skLineSegment(sketch, "E363", {"start": v(31.65, 116.87) * mm, "end": v(32.82, 117) * mm});
            skLineSegment(sketch, "E364", {"start": v(32.82, 117) * mm, "end": v(33.83, 117.1) * mm});
            skLineSegment(sketch, "E365", {"start": v(33.83, 117.1) * mm, "end": v(34.83, 117.16) * mm});
            skLineSegment(sketch, "E366", {"start": v(34.83, 117.16) * mm, "end": v(35.22, 116.62) * mm});
            skLineSegment(sketch, "E367", {"start": v(35.22, 116.62) * mm, "end": v(36.02, 115.4) * mm});
            skLineSegment(sketch, "E368", {"start": v(36.02, 115.4) * mm, "end": v(37.13, 113.6) * mm});
            skLineSegment(sketch, "E369", {"start": v(37.13, 113.6) * mm, "end": v(36.62, 112.76) * mm});
            skLineSegment(sketch, "E370", {"start": v(36.62, 112.76) * mm, "end": v(35.46, 110.98) * mm});
            skLineSegment(sketch, "E371", {"start": v(35.46, 110.98) * mm, "end": v(33.66, 108.5) * mm});
            skLineSegment(sketch, "E372", {"start": v(33.66, 108.5) * mm, "end": v(33.93, 107.92) * mm});
            skLineSegment(sketch, "E373", {"start": v(33.93, 107.92) * mm, "end": v(34.52, 106.63) * mm});
            skLineSegment(sketch, "E374", {"start": v(34.52, 106.63) * mm, "end": v(35.21, 104.87) * mm});
            skLineSegment(sketch, "E375", {"start": v(35.21, 104.87) * mm, "end": v(35.28, 104.7) * mm});
            skLineSegment(sketch, "E376", {"start": v(35.28, 104.7) * mm, "end": v(35.32, 104.57) * mm});
            skLineSegment(sketch, "E377", {"start": v(35.32, 104.57) * mm, "end": v(38.4, 103.98) * mm});
            skLineSegment(sketch, "E378", {"start": v(38.4, 103.98) * mm, "end": v(40.52, 103.45) * mm});
            skLineSegment(sketch, "E379", {"start": v(40.52, 103.45) * mm, "end": v(41.5, 103.17) * mm});
            skLineSegment(sketch, "E380", {"start": v(41.5, 103.17) * mm, "end": v(41.67, 102.53) * mm});
            skLineSegment(sketch, "E381", {"start": v(41.67, 102.53) * mm, "end": v(42.18, 100.35) * mm});
            skLineSegment(sketch, "E382", {"start": v(42.18, 100.35) * mm, "end": v(42.42, 99.02) * mm});
            skLineSegment(sketch, "E383", {"start": v(42.42, 99.02) * mm, "end": v(41.66, 98.42) * mm});
            skLineSegment(sketch, "E384", {"start": v(41.66, 98.42) * mm, "end": v(39.95, 97.14) * mm});
            skLineSegment(sketch, "E385", {"start": v(39.95, 97.14) * mm, "end": v(37.41, 95.44) * mm});
            skLineSegment(sketch, "E386", {"start": v(37.41, 95.44) * mm, "end": v(37.43, 95.26) * mm});
            skLineSegment(sketch, "E387", {"start": v(37.43, 95.26) * mm, "end": v(37.57, 93.38) * mm});
            skLineSegment(sketch, "E388", {"start": v(37.57, 93.38) * mm, "end": v(37.63, 91.31) * mm});
            skLineSegment(sketch, "E389", {"start": v(37.63, 91.31) * mm, "end": v(37.62, 91.17) * mm});
            skLineSegment(sketch, "E390", {"start": v(37.62, 91.17) * mm, "end": v(40.32, 89.56) * mm});
            skLineSegment(sketch, "E391", {"start": v(40.32, 89.56) * mm, "end": v(42.13, 88.33) * mm});
            skLineSegment(sketch, "E392", {"start": v(42.13, 88.33) * mm, "end": v(42.94, 87.74) * mm});
            skLineSegment(sketch, "E393", {"start": v(42.94, 87.74) * mm, "end": v(42.73, 85.63) * mm});
            skLineSegment(sketch, "E394", {"start": v(42.73, 85.63) * mm, "end": v(42.4, 83.53) * mm});
            skLineSegment(sketch, "E395", {"start": v(42.4, 83.53) * mm, "end": v(41.48, 83.22) * mm});
            skLineSegment(sketch, "E396", {"start": v(41.48, 83.22) * mm, "end": v(39.45, 82.6) * mm});
            skLineSegment(sketch, "E397", {"start": v(39.45, 82.6) * mm, "end": v(36.47, 81.86) * mm});
            skLineSegment(sketch, "E398", {"start": v(36.47, 81.86) * mm, "end": v(36.43, 81.7) * mm});
            skLineSegment(sketch, "E399", {"start": v(36.43, 81.7) * mm, "end": v(36.32, 81.24) * mm});
            skLineSegment(sketch, "E400", {"start": v(36.32, 81.24) * mm, "end": v(35.93, 79.87) * mm});
            skLineSegment(sketch, "E401", {"start": v(35.93, 79.87) * mm, "end": v(35.28, 77.91) * mm});
            skLineSegment(sketch, "E402", {"start": v(35.28, 77.91) * mm, "end": v(35.23, 77.78) * mm});
            skLineSegment(sketch, "E403", {"start": v(35.23, 77.78) * mm, "end": v(37.2, 75.35) * mm});
            skLineSegment(sketch, "E404", {"start": v(37.2, 75.35) * mm, "end": v(38.49, 73.57) * mm});
            skLineSegment(sketch, "E405", {"start": v(38.49, 73.57) * mm, "end": v(39.05, 72.74) * mm});
            skLineSegment(sketch, "E406", {"start": v(39.05, 72.74) * mm, "end": v(38.77, 72.14) * mm});
            skLineSegment(sketch, "E407", {"start": v(38.77, 72.14) * mm, "end": v(38.12, 70.83) * mm});
            skLineSegment(sketch, "E408", {"start": v(38.12, 70.83) * mm, "end": v(37.43, 69.55) * mm});
            skLineSegment(sketch, "E409", {"start": v(37.43, 69.55) * mm, "end": v(37.1, 68.97) * mm});
            skLineSegment(sketch, "E410", {"start": v(37.1, 68.97) * mm, "end": v(36.12, 69) * mm});
            skLineSegment(sketch, "E411", {"start": v(36.12, 69) * mm, "end": v(34, 69.12) * mm});
            skLineSegment(sketch, "E412", {"start": v(34, 69.12) * mm, "end": v(30.96, 69.44) * mm});
            skLineSegment(sketch, "E413", {"start": v(30.96, 69.44) * mm, "end": v(29.75, 67.76) * mm});
            skLineSegment(sketch, "E414", {"start": v(29.75, 67.76) * mm, "end": v(28.58, 66.28) * mm});
            skLineSegment(sketch, "E415", {"start": v(28.58, 66.28) * mm, "end": v(28.37, 66.04) * mm});
            skLineSegment(sketch, "E416", {"start": v(28.37, 66.04) * mm, "end": v(29.4, 63.07) * mm});
            skLineSegment(sketch, "E417", {"start": v(29.4, 63.07) * mm, "end": v(30.25, 59.99) * mm});
            skLineSegment(sketch, "E418", {"start": v(30.25, 59.99) * mm, "end": v(29.78, 59.52) * mm});
            skLineSegment(sketch, "E419", {"start": v(29.78, 59.52) * mm, "end": v(28.72, 58.51) * mm});
            skLineSegment(sketch, "E420", {"start": v(28.72, 58.51) * mm, "end": v(27.13, 57.1) * mm});
            skLineSegment(sketch, "E421", {"start": v(27.13, 57.1) * mm, "end": v(26.22, 57.46) * mm});
            skLineSegment(sketch, "E422", {"start": v(26.22, 57.46) * mm, "end": v(24.26, 58.3) * mm});
            skLineSegment(sketch, "E423", {"start": v(24.26, 58.3) * mm, "end": v(22.36, 59.2) * mm});
            skLineSegment(sketch, "E424", {"start": v(22.36, 59.2) * mm, "end": v(21.5, 59.65) * mm});
            skLineSegment(sketch, "E425", {"start": v(21.5, 59.65) * mm, "end": v(20.44, 58.9) * mm});
            skLineSegment(sketch, "E426", {"start": v(20.44, 58.9) * mm, "end": v(18.6, 57.72) * mm});
            skLineSegment(sketch, "E427", {"start": v(18.6, 57.72) * mm, "end": v(17.92, 57.33) * mm});
            skLineSegment(sketch, "E428", {"start": v(17.92, 57.33) * mm, "end": v(17.93, 56.35) * mm});
            skLineSegment(sketch, "E429", {"start": v(17.93, 56.35) * mm, "end": v(17.93, 55.34) * mm});
            skLineSegment(sketch, "E430", {"start": v(17.93, 55.34) * mm, "end": v(17.88, 54.19) * mm});
            skLineSegment(sketch, "E431", {"start": v(17.88, 54.19) * mm, "end": v(17.73, 52) * mm});
            skLineSegment(sketch, "E432", {"start": v(17.73, 52) * mm, "end": v(17.62, 51) * mm});
            skLineSegment(sketch, "E433", {"start": v(17.62, 51) * mm, "end": v(15.68, 50.13) * mm});
            skLineSegment(sketch, "E434", {"start": v(15.68, 50.13) * mm, "end": v(13.88, 49.42) * mm});
            skLineSegment(sketch, "E435", {"start": v(13.88, 49.42) * mm, "end": v(13.7, 49.36) * mm});
            skLineSegment(sketch, "E436", {"start": v(13.7, 49.36) * mm, "end": v(11.42, 51.47) * mm});
            skLineSegment(sketch, "E437", {"start": v(11.42, 51.47) * mm, "end": v(10.62, 52.26) * mm});
            skLineSegment(sketch, "E438", {"start": v(10.62, 52.26) * mm, "end": v(9.3, 53.68) * mm});
            skLineSegment(sketch, "E439", {"start": v(9.3, 53.68) * mm, "end": v(8.67, 53.5) * mm});
            skLineSegment(sketch, "E440", {"start": v(8.67, 53.5) * mm, "end": v(7.3, 53.16) * mm});
            skLineSegment(sketch, "E441", {"start": v(7.3, 53.16) * mm, "end": v(5.9, 52.87) * mm});
            skLineSegment(sketch, "E442", {"start": v(5.9, 52.87) * mm, "end": v(5.14, 52.73) * mm});
            skLineSegment(sketch, "E443", {"start": v(5.14, 52.73) * mm, "end": v(4.01, 49.8) * mm});
            skLineSegment(sketch, "E444", {"start": v(4.01, 49.8) * mm, "end": v(3.12, 47.79) * mm});
            skLineSegment(sketch, "E445", {"start": v(3.12, 47.79) * mm, "end": v(2.68, 46.89) * mm});
            skLineSegment(sketch, "E446", {"start": v(2.68, 46.89) * mm, "end": v(0.56, 46.74) * mm});
            skLineSegment(sketch, "E447", {"start": v(0.56, 46.74) * mm, "end": v(-1.56, 46.69) * mm});
            skLineSegment(sketch, "E448", {"start": v(-1.56, 46.69) * mm, "end": v(-3, 49.46) * mm});
            skLineSegment(sketch, "E449", {"start": v(-3, 49.46) * mm, "end": v(-3.86, 51.37) * mm});
            skLineSegment(sketch, "E450", {"start": v(-3.86, 51.37) * mm, "end": v(-4.23, 52.26) * mm});
            skLineSegment(sketch, "E451", {"start": v(-4.23, 52.26) * mm, "end": v(-5.54, 52.35) * mm});
            skLineSegment(sketch, "E452", {"start": v(-5.54, 52.35) * mm, "end": v(-7.7, 52.64) * mm});
            skLineSegment(sketch, "E453", {"start": v(-7.7, 52.64) * mm, "end": v(-8.47, 52.78) * mm});
            skLineSegment(sketch, "E454", {"start": v(-8.47, 52.78) * mm, "end": v(-9.1, 52.02) * mm});
            skLineSegment(sketch, "E455", {"start": v(-9.1, 52.02) * mm, "end": v(-9.75, 51.25) * mm});
            skLineSegment(sketch, "E456", {"start": v(-9.75, 51.25) * mm, "end": v(-10.52, 50.4) * mm});
            skLineSegment(sketch, "E457", {"start": v(-10.52, 50.4) * mm, "end": v(-12.05, 48.82) * mm});
            skLineSegment(sketch, "E458", {"start": v(-12.05, 48.82) * mm, "end": v(-12.77, 48.12) * mm});
            skLineSegment(sketch, "E459", {"start": v(-12.77, 48.12) * mm, "end": v(-14.81, 48.7) * mm});
            skLineSegment(sketch, "E460", {"start": v(-14.81, 48.7) * mm, "end": v(-16.83, 49.38) * mm});
            skLineSegment(sketch, "E461", {"start": v(-16.83, 49.38) * mm, "end": v(-16.97, 50.35) * mm});
            skLineSegment(sketch, "E462", {"start": v(-16.97, 50.35) * mm, "end": v(-17.22, 52.47) * mm});
            skLineSegment(sketch, "E463", {"start": v(-17.22, 52.47) * mm, "end": v(-17.38, 54.57) * mm});
            skLineSegment(sketch, "E464", {"start": v(-17.38, 54.57) * mm, "end": v(-17.43, 55.53) * mm});
            skLineSegment(sketch, "E465", {"start": v(-17.43, 55.53) * mm, "end": v(-18.01, 55.8) * mm});
            skLineSegment(sketch, "E466", {"start": v(-18.01, 55.8) * mm, "end": v(-19.29, 56.42) * mm});
            skLineSegment(sketch, "E467", {"start": v(-19.29, 56.42) * mm, "end": v(-20.54, 57.08) * mm});
            skLineSegment(sketch, "E468", {"start": v(-20.54, 57.08) * mm, "end": v(-21.22, 57.47) * mm});
            skLineSegment(sketch, "E469", {"start": v(-21.22, 57.47) * mm, "end": v(-23.97, 55.94) * mm});
            skLineSegment(sketch, "E470", {"start": v(-23.97, 55.94) * mm, "end": v(-25.95, 54.98) * mm});
            skLineSegment(sketch, "E471", {"start": v(-25.95, 54.98) * mm, "end": v(-26.86, 54.58) * mm});
            skLineSegment(sketch, "E472", {"start": v(-26.86, 54.58) * mm, "end": v(-28.58, 55.82) * mm});
            skLineSegment(sketch, "E473", {"start": v(-28.58, 55.82) * mm, "end": v(-29.73, 56.73) * mm});
            skLineSegment(sketch, "E474", {"start": v(-29.73, 56.73) * mm, "end": v(-30.1, 57.03) * mm});
            skLineSegment(sketch, "E475", {"start": v(-30.1, 57.03) * mm, "end": v(-30.24, 57.15) * mm});
            skLineSegment(sketch, "E476", {"start": v(-30.24, 57.15) * mm, "end": v(-29.56, 60.18) * mm});
            skLineSegment(sketch, "E477", {"start": v(-29.56, 60.18) * mm, "end": v(-28.98, 62.22) * mm});
            skLineSegment(sketch, "E478", {"start": v(-28.98, 62.22) * mm, "end": v(-28.7, 63.13) * mm});
            skLineSegment(sketch, "E479", {"start": v(-28.7, 63.13) * mm, "end": v(-29.17, 63.57) * mm});
            skLineSegment(sketch, "E480", {"start": v(-29.17, 63.57) * mm, "end": v(-30.15, 64.6) * mm});
            skLineSegment(sketch, "E481", {"start": v(-30.15, 64.6) * mm, "end": v(-31.61, 66.25) * mm});
            skLineSegment(sketch, "E482", {"start": v(-31.61, 66.25) * mm, "end": v(-32.57, 66.07) * mm});
            skLineSegment(sketch, "E483", {"start": v(-32.57, 66.07) * mm, "end": v(-34.71, 65.75) * mm});
            skLineSegment(sketch, "E484", {"start": v(-34.71, 65.75) * mm, "end": v(-35.88, 65.61) * mm});
            skLineSegment(sketch, "E485", {"start": v(-35.88, 65.61) * mm, "end": v(-36.9, 65.53) * mm});
            skLineSegment(sketch, "E486", {"start": v(-36.9, 65.53) * mm, "end": v(-37.9, 65.46) * mm});
            skLineSegment(sketch, "E487", {"start": v(-37.9, 65.46) * mm, "end": v(-38.28, 66) * mm});
            skLineSegment(sketch, "E488", {"start": v(-38.28, 66) * mm, "end": v(-39.08, 67.21) * mm});
            skLineSegment(sketch, "E489", {"start": v(-39.08, 67.21) * mm, "end": v(-40.19, 69.03) * mm});
            skLineSegment(sketch, "E490", {"start": v(-40.19, 69.03) * mm, "end": v(-39.68, 69.86) * mm});
            skLineSegment(sketch, "E491", {"start": v(-39.68, 69.86) * mm, "end": v(-38.52, 71.64) * mm});
            skLineSegment(sketch, "E492", {"start": v(-38.52, 71.64) * mm, "end": v(-36.72, 74.12) * mm});
            skLineSegment(sketch, "E493", {"start": v(-36.72, 74.12) * mm, "end": v(-37, 74.7) * mm});
            skLineSegment(sketch, "E494", {"start": v(-37, 74.7) * mm, "end": v(-37.58, 76) * mm});
            skLineSegment(sketch, "E495", {"start": v(-37.58, 76) * mm, "end": v(-38.27, 77.75) * mm});
            skLineSegment(sketch, "E496", {"start": v(-38.27, 77.75) * mm, "end": v(-38.34, 77.91) * mm});
            skLineSegment(sketch, "E497", {"start": v(-38.34, 77.91) * mm, "end": v(-38.38, 78.05) * mm});
            skLineSegment(sketch, "E498", {"start": v(-38.38, 78.05) * mm, "end": v(-41.47, 78.64) * mm});
            skLineSegment(sketch, "E499", {"start": v(-41.47, 78.64) * mm, "end": v(-43.58, 79.18) * mm});
            skLineSegment(sketch, "E500", {"start": v(-43.58, 79.18) * mm, "end": v(-44.55, 79.45) * mm});
            skLineSegment(sketch, "E501", {"start": v(-44.55, 79.45) * mm, "end": v(-44.73, 80.1) * mm});
            skLineSegment(sketch, "E502", {"start": v(-44.73, 80.1) * mm, "end": v(-45.24, 82.27) * mm});
            skLineSegment(sketch, "E503", {"start": v(-45.24, 82.27) * mm, "end": v(-45.48, 83.6) * mm});
            skLineSegment(sketch, "E504", {"start": v(-45.48, 83.6) * mm, "end": v(-44.72, 84.2) * mm});
            skLineSegment(sketch, "E505", {"start": v(-44.72, 84.2) * mm, "end": v(-43, 85.48) * mm});
            skLineSegment(sketch, "E506", {"start": v(-43, 85.48) * mm, "end": v(-40.47, 87.18) * mm});
            skLineSegment(sketch, "E507", {"start": v(-40.47, 87.18) * mm, "end": v(-40.49, 87.36) * mm});
            skLineSegment(sketch, "E508", {"start": v(-40.49, 87.36) * mm, "end": v(-40.63, 89.24) * mm});
            skLineSegment(sketch, "E509", {"start": v(-40.63, 89.24) * mm, "end": v(-40.69, 91.31) * mm});
            skLineSegment(sketch, "E510", {"start": v(-40.69, 91.31) * mm, "end": v(-40.68, 91.45) * mm});
            skLineSegment(sketch, "E511", {"start": v(56.84, -103.49) * mm, "end": v(56.83, -102.87) * mm});
            skLineSegment(sketch, "E512", {"start": v(56.83, -102.87) * mm, "end": v(56.76, -101.52) * mm});
            skLineSegment(sketch, "E513", {"start": v(56.76, -101.52) * mm, "end": v(56.7, -100.8) * mm});
            skLineSegment(sketch, "E514", {"start": v(56.7, -100.8) * mm, "end": v(56.55, -99.56) * mm});
            skLineSegment(sketch, "E515", {"start": v(56.55, -99.56) * mm, "end": v(57.34, -99.03) * mm});
            skLineSegment(sketch, "E516", {"start": v(57.34, -99.03) * mm, "end": v(59.02, -97.78) * mm});
            skLineSegment(sketch, "E517", {"start": v(59.02, -97.78) * mm, "end": v(60.65, -96.41) * mm});
            skLineSegment(sketch, "E518", {"start": v(60.65, -96.41) * mm, "end": v(61.38, -95.76) * mm});
            skLineSegment(sketch, "E519", {"start": v(61.38, -95.76) * mm, "end": v(61.34, -95.58) * mm});
            skLineSegment(sketch, "E520", {"start": v(61.34, -95.58) * mm, "end": v(61.21, -95.1) * mm});
            skLineSegment(sketch, "E521", {"start": v(61.21, -95.1) * mm, "end": v(60.8, -93.7) * mm});
            skLineSegment(sketch, "E522", {"start": v(60.8, -93.7) * mm, "end": v(60.33, -92.3) * mm});
            skLineSegment(sketch, "E523", {"start": v(60.33, -92.3) * mm, "end": v(60.09, -91.68) * mm});
            skLineSegment(sketch, "E524", {"start": v(60.09, -91.68) * mm, "end": v(59.1, -91.5) * mm});
            skLineSegment(sketch, "E525", {"start": v(59.1, -91.5) * mm, "end": v(56.93, -91.22) * mm});
            skLineSegment(sketch, "E526", {"start": v(56.93, -91.22) * mm, "end": v(54.78, -91.08) * mm});
            skLineSegment(sketch, "E527", {"start": v(54.78, -91.08) * mm, "end": v(53.81, -91.07) * mm});
            skLineSegment(sketch, "E528", {"start": v(53.81, -91.07) * mm, "end": v(53.68, -90.8) * mm});
            skLineSegment(sketch, "E529", {"start": v(53.68, -90.8) * mm, "end": v(53.46, -90.4) * mm});
            skLineSegment(sketch, "E530", {"start": v(53.46, -90.4) * mm, "end": v(52.77, -89.24) * mm});
            skLineSegment(sketch, "E531", {"start": v(52.77, -89.24) * mm, "end": v(52.03, -88.1) * mm});
            skLineSegment(sketch, "E532", {"start": v(52.03, -88.1) * mm, "end": v(51.67, -87.6) * mm});
            skLineSegment(sketch, "E533", {"start": v(51.67, -87.6) * mm, "end": v(52.12, -86.77) * mm});
            skLineSegment(sketch, "E534", {"start": v(52.12, -86.77) * mm, "end": v(53.02, -84.88) * mm});
            skLineSegment(sketch, "E535", {"start": v(53.02, -84.88) * mm, "end": v(53.83, -82.91) * mm});
            skLineSegment(sketch, "E536", {"start": v(53.83, -82.91) * mm, "end": v(54.17, -82) * mm});
            skLineSegment(sketch, "E537", {"start": v(54.17, -82) * mm, "end": v(54.05, -81.86) * mm});
            skLineSegment(sketch, "E538", {"start": v(54.05, -81.86) * mm, "end": v(53.72, -81.5) * mm});
            skLineSegment(sketch, "E539", {"start": v(53.72, -81.5) * mm, "end": v(52.7, -80.44) * mm});
            skLineSegment(sketch, "E540", {"start": v(52.7, -80.44) * mm, "end": v(51.64, -79.43) * mm});
            skLineSegment(sketch, "E541", {"start": v(51.64, -79.43) * mm, "end": v(51.13, -78.99) * mm});
            skLineSegment(sketch, "E542", {"start": v(51.13, -78.99) * mm, "end": v(48.12, -80.05) * mm});
            skLineSegment(sketch, "E543", {"start": v(48.12, -80.05) * mm, "end": v(47.07, -80.5) * mm});
            skLineSegment(sketch, "E544", {"start": v(47.07, -80.5) * mm, "end": v(46.16, -80.92) * mm});
            skLineSegment(sketch, "E545", {"start": v(46.16, -80.92) * mm, "end": v(45.3, -81.36) * mm});
            skLineSegment(sketch, "E546", {"start": v(45.3, -81.36) * mm, "end": v(45.18, -81.28) * mm});
            skLineSegment(sketch, "E547", {"start": v(45.18, -81.28) * mm, "end": v(44.67, -80.93) * mm});
            skLineSegment(sketch, "E548", {"start": v(44.67, -80.93) * mm, "end": v(43.52, -80.22) * mm});
            skLineSegment(sketch, "E549", {"start": v(43.52, -80.22) * mm, "end": v(42.34, -79.56) * mm});
            skLineSegment(sketch, "E550", {"start": v(42.34, -79.56) * mm, "end": v(41.79, -79.28) * mm});
            skLineSegment(sketch, "E551", {"start": v(41.79, -79.28) * mm, "end": v(41.8, -78.33) * mm});
            skLineSegment(sketch, "E552", {"start": v(41.8, -78.33) * mm, "end": v(41.72, -76.24) * mm});
            skLineSegment(sketch, "E553", {"start": v(41.72, -76.24) * mm, "end": v(41.53, -74.12) * mm});
            skLineSegment(sketch, "E554", {"start": v(41.53, -74.12) * mm, "end": v(41.4, -73.15) * mm});
            skLineSegment(sketch, "E555", {"start": v(41.4, -73.15) * mm, "end": v(41.23, -73.09) * mm});
            skLineSegment(sketch, "E556", {"start": v(41.23, -73.09) * mm, "end": v(40.77, -72.92) * mm});
            skLineSegment(sketch, "E557", {"start": v(40.77, -72.92) * mm, "end": v(39.37, -72.45) * mm});
            skLineSegment(sketch, "E558", {"start": v(39.37, -72.45) * mm, "end": v(37.96, -72.05) * mm});
            skLineSegment(sketch, "E559", {"start": v(37.96, -72.05) * mm, "end": v(37.3, -71.9) * mm});
            skLineSegment(sketch, "E560", {"start": v(37.3, -71.9) * mm, "end": v(36.6, -72.62) * mm});
            skLineSegment(sketch, "E561", {"start": v(36.6, -72.62) * mm, "end": v(35.14, -74.24) * mm});
            skLineSegment(sketch, "E562", {"start": v(35.14, -74.24) * mm, "end": v(33.8, -75.93) * mm});
            skLineSegment(sketch, "E563", {"start": v(33.8, -75.93) * mm, "end": v(33.24, -76.72) * mm});
            skLineSegment(sketch, "E564", {"start": v(33.24, -76.72) * mm, "end": v(32.5, -76.63) * mm});
            skLineSegment(sketch, "E565", {"start": v(32.5, -76.63) * mm, "end": v(31.15, -76.53) * mm});
            skLineSegment(sketch, "E566", {"start": v(31.15, -76.53) * mm, "end": v(29.8, -76.5) * mm});
            skLineSegment(sketch, "E567", {"start": v(29.8, -76.5) * mm, "end": v(29.17, -76.52) * mm});
            skLineSegment(sketch, "E568", {"start": v(29.17, -76.52) * mm, "end": v(28.74, -75.68) * mm});
            skLineSegment(sketch, "E569", {"start": v(28.74, -75.68) * mm, "end": v(27.7, -73.85) * mm});
            skLineSegment(sketch, "E570", {"start": v(27.7, -73.85) * mm, "end": v(26.54, -72.06) * mm});
            skLineSegment(sketch, "E571", {"start": v(26.54, -72.06) * mm, "end": v(25.98, -71.27) * mm});
            skLineSegment(sketch, "E572", {"start": v(25.98, -71.27) * mm, "end": v(25.32, -71.35) * mm});
            skLineSegment(sketch, "E573", {"start": v(25.32, -71.35) * mm, "end": v(23.87, -71.6) * mm});
            skLineSegment(sketch, "E574", {"start": v(23.87, -71.6) * mm, "end": v(22.43, -71.9) * mm});
            skLineSegment(sketch, "E575", {"start": v(22.43, -71.9) * mm, "end": v(21.78, -72.05) * mm});
            skLineSegment(sketch, "E576", {"start": v(21.78, -72.05) * mm, "end": v(20.94, -75.13) * mm});
            skLineSegment(sketch, "E577", {"start": v(20.94, -75.13) * mm, "end": v(20.54, -77.25) * mm});
            skLineSegment(sketch, "E578", {"start": v(20.54, -77.25) * mm, "end": v(20.4, -78.2) * mm});
            skLineSegment(sketch, "E579", {"start": v(20.4, -78.2) * mm, "end": v(19.71, -78.48) * mm});
            skLineSegment(sketch, "E580", {"start": v(19.71, -78.48) * mm, "end": v(18.47, -79.02) * mm});
            skLineSegment(sketch, "E581", {"start": v(18.47, -79.02) * mm, "end": v(17.26, -79.62) * mm});
            skLineSegment(sketch, "E582", {"start": v(17.26, -79.62) * mm, "end": v(16.86, -79.83) * mm});
            skLineSegment(sketch, "E583", {"start": v(16.86, -79.83) * mm, "end": v(16.72, -79.92) * mm});
            skLineSegment(sketch, "E584", {"start": v(16.72, -79.92) * mm, "end": v(15.94, -79.38) * mm});
            skLineSegment(sketch, "E585", {"start": v(15.94, -79.38) * mm, "end": v(14.17, -78.24) * mm});
            skLineSegment(sketch, "E586", {"start": v(14.17, -78.24) * mm, "end": v(12.32, -77.2) * mm});
            skLineSegment(sketch, "E587", {"start": v(12.32, -77.2) * mm, "end": v(11.45, -76.76) * mm});
            skLineSegment(sketch, "E588", {"start": v(11.45, -76.76) * mm, "end": v(10.9, -77.15) * mm});
            skLineSegment(sketch, "E589", {"start": v(10.9, -77.15) * mm, "end": v(9.73, -78.04) * mm});
            skLineSegment(sketch, "E590", {"start": v(9.73, -78.04) * mm, "end": v(8.6, -78.97) * mm});
            skLineSegment(sketch, "E591", {"start": v(8.6, -78.97) * mm, "end": v(8.1, -79.41) * mm});
            skLineSegment(sketch, "E592", {"start": v(8.1, -79.41) * mm, "end": v(8.29, -80.4) * mm});
            skLineSegment(sketch, "E593", {"start": v(8.29, -80.4) * mm, "end": v(8.79, -82.53) * mm});
            skLineSegment(sketch, "E594", {"start": v(8.79, -82.53) * mm, "end": v(9.42, -84.59) * mm});
            skLineSegment(sketch, "E595", {"start": v(9.42, -84.59) * mm, "end": v(9.75, -85.5) * mm});
            skLineSegment(sketch, "E596", {"start": v(9.75, -85.5) * mm, "end": v(9.26, -86.06) * mm});
            skLineSegment(sketch, "E597", {"start": v(9.26, -86.06) * mm, "end": v(8.4, -87.12) * mm});
            skLineSegment(sketch, "E598", {"start": v(8.4, -87.12) * mm, "end": v(7.6, -88.22) * mm});
            skLineSegment(sketch, "E599", {"start": v(7.6, -88.22) * mm, "end": v(7.36, -88.59) * mm});
            skLineSegment(sketch, "E600", {"start": v(7.36, -88.59) * mm, "end": v(7.27, -88.73) * mm});
            skLineSegment(sketch, "E601", {"start": v(7.27, -88.73) * mm, "end": v(6.33, -88.6) * mm});
            skLineSegment(sketch, "E602", {"start": v(6.33, -88.6) * mm, "end": v(4.24, -88.42) * mm});
            skLineSegment(sketch, "E603", {"start": v(4.24, -88.42) * mm, "end": v(2.1, -88.36) * mm});
            skLineSegment(sketch, "E604", {"start": v(2.1, -88.36) * mm, "end": v(1.13, -88.37) * mm});
            skLineSegment(sketch, "E605", {"start": v(1.13, -88.37) * mm, "end": v(0.83, -88.97) * mm});
            skLineSegment(sketch, "E606", {"start": v(0.83, -88.97) * mm, "end": v(0.2, -90.3) * mm});
            skLineSegment(sketch, "E607", {"start": v(0.2, -90.3) * mm, "end": v(-0.37, -91.66) * mm});
            skLineSegment(sketch, "E608", {"start": v(-0.37, -91.66) * mm, "end": v(-0.6, -92.28) * mm});
            skLineSegment(sketch, "E609", {"start": v(-0.6, -92.28) * mm, "end": v(0.02, -93.07) * mm});
            skLineSegment(sketch, "E610", {"start": v(0.02, -93.07) * mm, "end": v(1.45, -94.72) * mm});
            skLineSegment(sketch, "E611", {"start": v(1.45, -94.72) * mm, "end": v(2.97, -96.24) * mm});
            skLineSegment(sketch, "E612", {"start": v(2.97, -96.24) * mm, "end": v(3.68, -96.9) * mm});
            skLineSegment(sketch, "E613", {"start": v(3.68, -96.9) * mm, "end": v(3.51, -97.63) * mm});
            skLineSegment(sketch, "E614", {"start": v(3.51, -97.63) * mm, "end": v(3.26, -98.96) * mm});
            skLineSegment(sketch, "E615", {"start": v(3.26, -98.96) * mm, "end": v(3, -100.74) * mm});
            skLineSegment(sketch, "E616", {"start": v(3, -100.74) * mm, "end": v(3, -100.9) * mm});
            skLineSegment(sketch, "E617", {"start": v(3, -100.9) * mm, "end": v(0.17, -102.05) * mm});
            skLineSegment(sketch, "E618", {"start": v(0.17, -102.05) * mm, "end": v(-2.6, -103.46) * mm});
            skLineSegment(sketch, "E619", {"start": v(-2.6, -103.46) * mm, "end": v(-2.58, -104.12) * mm});
            skLineSegment(sketch, "E620", {"start": v(-2.58, -104.12) * mm, "end": v(-2.53, -105.59) * mm});
            skLineSegment(sketch, "E621", {"start": v(-2.53, -105.59) * mm, "end": v(-2.4, -107.05) * mm});
            skLineSegment(sketch, "E622", {"start": v(-2.4, -107.05) * mm, "end": v(-2.32, -107.72) * mm});
            skLineSegment(sketch, "E623", {"start": v(-2.32, -107.72) * mm, "end": v(-1.4, -108.12) * mm});
            skLineSegment(sketch, "E624", {"start": v(-1.4, -108.12) * mm, "end": v(0.64, -108.92) * mm});
            skLineSegment(sketch, "E625", {"start": v(0.64, -108.92) * mm, "end": v(1.72, -109.29) * mm});
            skLineSegment(sketch, "E626", {"start": v(1.72, -109.29) * mm, "end": v(2.69, -109.57) * mm});
            skLineSegment(sketch, "E627", {"start": v(2.69, -109.57) * mm, "end": v(3.62, -109.82) * mm});
            skLineSegment(sketch, "E628", {"start": v(3.62, -109.82) * mm, "end": v(3.65, -109.95) * mm});
            skLineSegment(sketch, "E629", {"start": v(3.65, -109.95) * mm, "end": v(3.8, -110.55) * mm});
            skLineSegment(sketch, "E630", {"start": v(3.8, -110.55) * mm, "end": v(4.2, -111.84) * mm});
            skLineSegment(sketch, "E631", {"start": v(4.2, -111.84) * mm, "end": v(4.64, -113.12) * mm});
            skLineSegment(sketch, "E632", {"start": v(4.64, -113.12) * mm, "end": v(4.87, -113.7) * mm});
            skLineSegment(sketch, "E633", {"start": v(4.87, -113.7) * mm, "end": v(4.23, -114.4) * mm});
            skLineSegment(sketch, "E634", {"start": v(4.23, -114.4) * mm, "end": v(2.9, -116.01) * mm});
            skLineSegment(sketch, "E635", {"start": v(2.9, -116.01) * mm, "end": v(1.65, -117.73) * mm});
            skLineSegment(sketch, "E636", {"start": v(1.65, -117.73) * mm, "end": v(1.1, -118.54) * mm});
            skLineSegment(sketch, "E637", {"start": v(1.1, -118.54) * mm, "end": v(1.19, -118.7) * mm});
            skLineSegment(sketch, "E638", {"start": v(1.19, -118.7) * mm, "end": v(1.42, -119.13) * mm});
            skLineSegment(sketch, "E639", {"start": v(1.42, -119.13) * mm, "end": v(2.16, -120.4) * mm});
            skLineSegment(sketch, "E640", {"start": v(2.16, -120.4) * mm, "end": v(2.95, -121.64) * mm});
            skLineSegment(sketch, "E641", {"start": v(2.95, -121.64) * mm, "end": v(3.34, -122.19) * mm});
            skLineSegment(sketch, "E642", {"start": v(3.34, -122.19) * mm, "end": v(4.34, -122.12) * mm});
            skLineSegment(sketch, "E643", {"start": v(4.34, -122.12) * mm, "end": v(6.51, -121.87) * mm});
            skLineSegment(sketch, "E644", {"start": v(6.51, -121.87) * mm, "end": v(8.63, -121.5) * mm});
            skLineSegment(sketch, "E645", {"start": v(8.63, -121.5) * mm, "end": v(9.57, -121.28) * mm});
            skLineSegment(sketch, "E646", {"start": v(9.57, -121.28) * mm, "end": v(9.77, -121.5) * mm});
            skLineSegment(sketch, "E647", {"start": v(9.77, -121.5) * mm, "end": v(10.07, -121.84) * mm});
            skLineSegment(sketch, "E648", {"start": v(10.07, -121.84) * mm, "end": v(11.02, -122.8) * mm});
            skLineSegment(sketch, "E649", {"start": v(11.02, -122.8) * mm, "end": v(12.01, -123.73) * mm});
            skLineSegment(sketch, "E650", {"start": v(12.01, -123.73) * mm, "end": v(12.48, -124.13) * mm});
            skLineSegment(sketch, "E651", {"start": v(12.48, -124.13) * mm, "end": v(12.24, -125.05) * mm});
            skLineSegment(sketch, "E652", {"start": v(12.24, -125.05) * mm, "end": v(11.81, -127.1) * mm});
            skLineSegment(sketch, "E653", {"start": v(11.81, -127.1) * mm, "end": v(11.5, -129.2) * mm});
            skLineSegment(sketch, "E654", {"start": v(11.5, -129.2) * mm, "end": v(11.4, -130.18) * mm});
            skLineSegment(sketch, "E655", {"start": v(11.4, -130.18) * mm, "end": v(11.54, -130.28) * mm});
            skLineSegment(sketch, "E656", {"start": v(11.54, -130.28) * mm, "end": v(11.94, -130.55) * mm});
            skLineSegment(sketch, "E657", {"start": v(11.94, -130.55) * mm, "end": v(13.19, -131.34) * mm});
            skLineSegment(sketch, "E658", {"start": v(13.19, -131.34) * mm, "end": v(14.46, -132.07) * mm});
            skLineSegment(sketch, "E659", {"start": v(14.46, -132.07) * mm, "end": v(15.06, -132.37) * mm});
            skLineSegment(sketch, "E660", {"start": v(15.06, -132.37) * mm, "end": v(17.73, -130.62) * mm});
            skLineSegment(sketch, "E661", {"start": v(17.73, -130.62) * mm, "end": v(18.65, -129.93) * mm});
            skLineSegment(sketch, "E662", {"start": v(18.65, -129.93) * mm, "end": v(19.43, -129.3) * mm});
            skLineSegment(sketch, "E663", {"start": v(19.43, -129.3) * mm, "end": v(20.16, -128.67) * mm});
            skLineSegment(sketch, "E664", {"start": v(20.16, -128.67) * mm, "end": v(20.44, -128.79) * mm});
            skLineSegment(sketch, "E665", {"start": v(20.44, -128.79) * mm, "end": v(20.86, -128.94) * mm});
            skLineSegment(sketch, "E666", {"start": v(20.86, -128.94) * mm, "end": v(22.15, -129.35) * mm});
            skLineSegment(sketch, "E667", {"start": v(22.15, -129.35) * mm, "end": v(23.46, -129.7) * mm});
            skLineSegment(sketch, "E668", {"start": v(23.46, -129.7) * mm, "end": v(24.06, -129.84) * mm});
            skLineSegment(sketch, "E669", {"start": v(24.06, -129.84) * mm, "end": v(24.28, -130.77) * mm});
            skLineSegment(sketch, "E670", {"start": v(24.28, -130.77) * mm, "end": v(24.85, -132.78) * mm});
            skLineSegment(sketch, "E671", {"start": v(24.85, -132.78) * mm, "end": v(25.55, -134.8) * mm});
            skLineSegment(sketch, "E672", {"start": v(25.55, -134.8) * mm, "end": v(25.91, -135.7) * mm});
            skLineSegment(sketch, "E673", {"start": v(25.91, -135.7) * mm, "end": v(26.58, -135.78) * mm});
            skLineSegment(sketch, "E674", {"start": v(26.58, -135.78) * mm, "end": v(28.04, -135.9) * mm});
            skLineSegment(sketch, "E675", {"start": v(28.04, -135.9) * mm, "end": v(29.51, -135.94) * mm});
            skLineSegment(sketch, "E676", {"start": v(29.51, -135.94) * mm, "end": v(30.18, -135.94) * mm});
            skLineSegment(sketch, "E677", {"start": v(30.18, -135.94) * mm, "end": v(30.7, -135.07) * mm});
            skLineSegment(sketch, "E678", {"start": v(30.7, -135.07) * mm, "end": v(31.72, -133.15) * mm});
            skLineSegment(sketch, "E679", {"start": v(31.72, -133.15) * mm, "end": v(32.62, -131.2) * mm});
            skLineSegment(sketch, "E680", {"start": v(32.62, -131.2) * mm, "end": v(32.98, -130.29) * mm});
            skLineSegment(sketch, "E681", {"start": v(32.98, -130.29) * mm, "end": v(33.72, -130.2) * mm});
            skLineSegment(sketch, "E682", {"start": v(33.72, -130.2) * mm, "end": v(35.06, -129.97) * mm});
            skLineSegment(sketch, "E683", {"start": v(35.06, -129.97) * mm, "end": v(36.38, -129.68) * mm});
            skLineSegment(sketch, "E684", {"start": v(36.38, -129.68) * mm, "end": v(36.81, -129.57) * mm});
            skLineSegment(sketch, "E685", {"start": v(36.81, -129.57) * mm, "end": v(36.98, -129.52) * mm});
            skLineSegment(sketch, "E686", {"start": v(36.98, -129.52) * mm, "end": v(37.6, -130.23) * mm});
            skLineSegment(sketch, "E687", {"start": v(37.6, -130.23) * mm, "end": v(39.04, -131.76) * mm});
            skLineSegment(sketch, "E688", {"start": v(39.04, -131.76) * mm, "end": v(40.6, -133.21) * mm});
            skLineSegment(sketch, "E689", {"start": v(40.6, -133.21) * mm, "end": v(41.33, -133.85) * mm});
            skLineSegment(sketch, "E690", {"start": v(41.33, -133.85) * mm, "end": v(41.96, -133.6) * mm});
            skLineSegment(sketch, "E691", {"start": v(41.96, -133.6) * mm, "end": v(43.3, -133.02) * mm});
            skLineSegment(sketch, "E692", {"start": v(43.3, -133.02) * mm, "end": v(44.63, -132.38) * mm});
            skLineSegment(sketch, "E693", {"start": v(44.63, -132.38) * mm, "end": v(45.23, -132.08) * mm});
            skLineSegment(sketch, "E694", {"start": v(45.23, -132.08) * mm, "end": v(45.24, -131.8) * mm});
            skLineSegment(sketch, "E695", {"start": v(45.24, -131.8) * mm, "end": v(45.28, -131.07) * mm});
            skLineSegment(sketch, "E696", {"start": v(45.28, -131.07) * mm, "end": v(45.3, -128.89) * mm});
            skLineSegment(sketch, "E697", {"start": v(45.3, -128.89) * mm, "end": v(45.17, -126.74) * mm});
            skLineSegment(sketch, "E698", {"start": v(45.17, -126.74) * mm, "end": v(45.07, -125.77) * mm});
            skLineSegment(sketch, "E699", {"start": v(45.07, -125.77) * mm, "end": v(45.68, -125.34) * mm});
            skLineSegment(sketch, "E700", {"start": v(45.68, -125.34) * mm, "end": v(46.76, -124.52) * mm});
            skLineSegment(sketch, "E701", {"start": v(46.76, -124.52) * mm, "end": v(47.8, -123.64) * mm});
            skLineSegment(sketch, "E702", {"start": v(47.8, -123.64) * mm, "end": v(48.13, -123.34) * mm});
            skLineSegment(sketch, "E703", {"start": v(48.13, -123.34) * mm, "end": v(48.25, -123.23) * mm});
            skLineSegment(sketch, "E704", {"start": v(48.25, -123.23) * mm, "end": v(49.13, -123.57) * mm});
            skLineSegment(sketch, "E705", {"start": v(49.13, -123.57) * mm, "end": v(51.12, -124.24) * mm});
            skLineSegment(sketch, "E706", {"start": v(51.12, -124.24) * mm, "end": v(53.17, -124.81) * mm});
            skLineSegment(sketch, "E707", {"start": v(53.17, -124.81) * mm, "end": v(54.12, -125.03) * mm});
            skLineSegment(sketch, "E708", {"start": v(54.12, -125.03) * mm, "end": v(54.56, -124.53) * mm});
            skLineSegment(sketch, "E709", {"start": v(54.56, -124.53) * mm, "end": v(55.49, -123.39) * mm});
            skLineSegment(sketch, "E710", {"start": v(55.49, -123.39) * mm, "end": v(56.36, -122.2) * mm});
            skLineSegment(sketch, "E711", {"start": v(56.36, -122.2) * mm, "end": v(56.75, -121.66) * mm});
            skLineSegment(sketch, "E712", {"start": v(56.75, -121.66) * mm, "end": v(55.33, -118.8) * mm});
            skLineSegment(sketch, "E713", {"start": v(55.33, -118.8) * mm, "end": v(54.23, -116.95) * mm});
            skLineSegment(sketch, "E714", {"start": v(54.23, -116.95) * mm, "end": v(53.7, -116.15) * mm});
            skLineSegment(sketch, "E715", {"start": v(53.7, -116.15) * mm, "end": v(53.75, -116.03) * mm});
            skLineSegment(sketch, "E716", {"start": v(53.75, -116.03) * mm, "end": v(54.6, -114.25) * mm});
            skLineSegment(sketch, "E717", {"start": v(54.6, -114.25) * mm, "end": v(55.12, -113) * mm});
            skLineSegment(sketch, "E718", {"start": v(55.12, -113) * mm, "end": v(55.27, -112.58) * mm});
            skLineSegment(sketch, "E719", {"start": v(55.27, -112.58) * mm, "end": v(55.32, -112.42) * mm});
            skLineSegment(sketch, "E720", {"start": v(55.32, -112.42) * mm, "end": v(56.26, -112.31) * mm});
            skLineSegment(sketch, "E721", {"start": v(56.26, -112.31) * mm, "end": v(58.34, -111.99) * mm});
            skLineSegment(sketch, "E722", {"start": v(58.34, -111.99) * mm, "end": v(60.42, -111.53) * mm});
            skLineSegment(sketch, "E723", {"start": v(60.42, -111.53) * mm, "end": v(61.36, -111.29) * mm});
            skLineSegment(sketch, "E724", {"start": v(61.36, -111.29) * mm, "end": v(61.66, -109.97) * mm});
            skLineSegment(sketch, "E725", {"start": v(61.66, -109.97) * mm, "end": v(61.94, -108.42) * mm});
            skLineSegment(sketch, "E726", {"start": v(61.94, -108.42) * mm, "end": v(62.1, -107.08) * mm});
            skLineSegment(sketch, "E727", {"start": v(62.1, -107.08) * mm, "end": v(61.31, -106.46) * mm});
            skLineSegment(sketch, "E728", {"start": v(61.31, -106.46) * mm, "end": v(59.52, -105.2) * mm});
            skLineSegment(sketch, "E729", {"start": v(59.52, -105.2) * mm, "end": v(57.68, -104.09) * mm});
            skLineSegment(sketch, "E730", {"start": v(57.68, -104.09) * mm, "end": v(56.84, -103.62) * mm});
            skLineSegment(sketch, "E731", {"start": v(56.84, -103.62) * mm, "end": v(56.84, -103.49) * mm});
            skLineSegment(sketch, "E732", {"start": v(43.7, -41.4) * mm, "end": v(44.49, -43.25) * mm});
            skLineSegment(sketch, "E733", {"start": v(44.49, -43.25) * mm, "end": v(44.82, -43.9) * mm});
            skLineSegment(sketch, "E734", {"start": v(44.82, -43.9) * mm, "end": v(45.14, -44.47) * mm});
            skLineSegment(sketch, "E735", {"start": v(45.14, -44.47) * mm, "end": v(45.47, -45.01) * mm});
            skLineSegment(sketch, "E736", {"start": v(45.47, -45.01) * mm, "end": v(44, -47.7) * mm});
            skLineSegment(sketch, "E737", {"start": v(44, -47.7) * mm, "end": v(43.15, -49.7) * mm});
            skLineSegment(sketch, "E738", {"start": v(43.15, -49.7) * mm, "end": v(42.81, -50.64) * mm});
            skLineSegment(sketch, "E739", {"start": v(42.81, -50.64) * mm, "end": v(44.4, -52.36) * mm});
            skLineSegment(sketch, "E740", {"start": v(44.4, -52.36) * mm, "end": v(45.58, -53.45) * mm});
            skLineSegment(sketch, "E741", {"start": v(45.58, -53.45) * mm, "end": v(45.98, -53.8) * mm});
            skLineSegment(sketch, "E742", {"start": v(45.98, -53.8) * mm, "end": v(46.14, -53.92) * mm});
            skLineSegment(sketch, "E743", {"start": v(46.14, -53.92) * mm, "end": v(47.13, -53.6) * mm});
            skLineSegment(sketch, "E744", {"start": v(47.13, -53.6) * mm, "end": v(49.2, -52.8) * mm});
            skLineSegment(sketch, "E745", {"start": v(49.2, -52.8) * mm, "end": v(51.16, -51.84) * mm});
            skLineSegment(sketch, "E746", {"start": v(51.16, -51.84) * mm, "end": v(51.77, -51.5) * mm});
            skLineSegment(sketch, "E747", {"start": v(51.77, -51.5) * mm, "end": v(52, -51.35) * mm});
            skLineSegment(sketch, "E748", {"start": v(52, -51.35) * mm, "end": v(52.12, -51.42) * mm});
            skLineSegment(sketch, "E749", {"start": v(52.12, -51.42) * mm, "end": v(53.91, -52.34) * mm});
            skLineSegment(sketch, "E750", {"start": v(53.91, -52.34) * mm, "end": v(54.6, -52.63) * mm});
            skLineSegment(sketch, "E751", {"start": v(54.6, -52.63) * mm, "end": v(55.2, -52.86) * mm});
            skLineSegment(sketch, "E752", {"start": v(55.2, -52.86) * mm, "end": v(55.8, -53.06) * mm});
            skLineSegment(sketch, "E753", {"start": v(55.8, -53.06) * mm, "end": v(55.94, -54) * mm});
            skLineSegment(sketch, "E754", {"start": v(55.94, -54) * mm, "end": v(56.4, -56.07) * mm});
            skLineSegment(sketch, "E755", {"start": v(56.4, -56.07) * mm, "end": v(57.03, -58.14) * mm});
            skLineSegment(sketch, "E756", {"start": v(57.03, -58.14) * mm, "end": v(57.38, -59.07) * mm});
            skLineSegment(sketch, "E757", {"start": v(57.38, -59.07) * mm, "end": v(58.1, -59.2) * mm});
            skLineSegment(sketch, "E758", {"start": v(58.1, -59.2) * mm, "end": v(59.7, -59.37) * mm});
            skLineSegment(sketch, "E759", {"start": v(59.7, -59.37) * mm, "end": v(61.3, -59.45) * mm});
            skLineSegment(sketch, "E760", {"start": v(61.3, -59.45) * mm, "end": v(62.04, -59.45) * mm});
            skLineSegment(sketch, "E761", {"start": v(62.04, -59.45) * mm, "end": v(63.67, -56.63) * mm});
            skLineSegment(sketch, "E762", {"start": v(63.67, -56.63) * mm, "end": v(64.54, -54.63) * mm});
            skLineSegment(sketch, "E763", {"start": v(64.54, -54.63) * mm, "end": v(64.79, -53.97) * mm});
            skLineSegment(sketch, "E764", {"start": v(64.79, -53.97) * mm, "end": v(64.88, -53.72) * mm});
            skLineSegment(sketch, "E765", {"start": v(64.88, -53.72) * mm, "end": v(65.63, -53.58) * mm});
            skLineSegment(sketch, "E766", {"start": v(65.63, -53.58) * mm, "end": v(66.97, -53.24) * mm});
            skLineSegment(sketch, "E767", {"start": v(66.97, -53.24) * mm, "end": v(68.3, -52.81) * mm});
            skLineSegment(sketch, "E768", {"start": v(68.3, -52.81) * mm, "end": v(68.88, -52.58) * mm});
            skLineSegment(sketch, "E769", {"start": v(68.88, -52.58) * mm, "end": v(69.07, -52.76) * mm});
            skLineSegment(sketch, "E770", {"start": v(69.07, -52.76) * mm, "end": v(69.6, -53.21) * mm});
            skLineSegment(sketch, "E771", {"start": v(69.6, -53.21) * mm, "end": v(71.27, -54.5) * mm});
            skLineSegment(sketch, "E772", {"start": v(71.27, -54.5) * mm, "end": v(73.09, -55.68) * mm});
            skLineSegment(sketch, "E773", {"start": v(73.09, -55.68) * mm, "end": v(73.96, -56.17) * mm});
            skLineSegment(sketch, "E774", {"start": v(73.96, -56.17) * mm, "end": v(74.59, -55.8) * mm});
            skLineSegment(sketch, "E775", {"start": v(74.59, -55.8) * mm, "end": v(75.92, -54.9) * mm});
            skLineSegment(sketch, "E776", {"start": v(75.92, -54.9) * mm, "end": v(77.2, -53.94) * mm});
            skLineSegment(sketch, "E777", {"start": v(77.2, -53.94) * mm, "end": v(77.77, -53.46) * mm});
            skLineSegment(sketch, "E778", {"start": v(77.77, -53.46) * mm, "end": v(77.64, -52.45) * mm});
            skLineSegment(sketch, "E779", {"start": v(77.64, -52.45) * mm, "end": v(77.2, -50.26) * mm});
            skLineSegment(sketch, "E780", {"start": v(77.2, -50.26) * mm, "end": v(76.6, -48.16) * mm});
            skLineSegment(sketch, "E781", {"start": v(76.6, -48.16) * mm, "end": v(76.25, -47.25) * mm});
            skLineSegment(sketch, "E782", {"start": v(76.25, -47.25) * mm, "end": v(76.46, -47.02) * mm});
            skLineSegment(sketch, "E783", {"start": v(76.46, -47.02) * mm, "end": v(76.74, -46.65) * mm});
            skLineSegment(sketch, "E784", {"start": v(76.74, -46.65) * mm, "end": v(77.56, -45.54) * mm});
            skLineSegment(sketch, "E785", {"start": v(77.56, -45.54) * mm, "end": v(78.3, -44.35) * mm});
            skLineSegment(sketch, "E786", {"start": v(78.3, -44.35) * mm, "end": v(78.52, -43.96) * mm});
            skLineSegment(sketch, "E787", {"start": v(78.52, -43.96) * mm, "end": v(78.6, -43.8) * mm});
            skLineSegment(sketch, "E788", {"start": v(78.6, -43.8) * mm, "end": v(79.55, -43.82) * mm});
            skLineSegment(sketch, "E789", {"start": v(79.55, -43.82) * mm, "end": v(81.66, -43.74) * mm});
            skLineSegment(sketch, "E790", {"start": v(81.66, -43.74) * mm, "end": v(83.81, -43.48) * mm});
            skLineSegment(sketch, "E791", {"start": v(83.81, -43.48) * mm, "end": v(84.8, -43.3) * mm});
            skLineSegment(sketch, "E792", {"start": v(84.8, -43.3) * mm, "end": v(85.03, -42.6) * mm});
            skLineSegment(sketch, "E793", {"start": v(85.03, -42.6) * mm, "end": v(85.5, -41.06) * mm});
            skLineSegment(sketch, "E794", {"start": v(85.5, -41.06) * mm, "end": v(85.97, -38.77) * mm});
            skLineSegment(sketch, "E795", {"start": v(85.97, -38.77) * mm, "end": v(85.21, -38.07) * mm});
            skLineSegment(sketch, "E796", {"start": v(85.21, -38.07) * mm, "end": v(83.47, -36.68) * mm});
            skLineSegment(sketch, "E797", {"start": v(83.47, -36.68) * mm, "end": v(81.66, -35.47) * mm});
            skLineSegment(sketch, "E798", {"start": v(81.66, -35.47) * mm, "end": v(80.82, -34.98) * mm});
            skLineSegment(sketch, "E799", {"start": v(80.82, -34.98) * mm, "end": v(80.82, -34.85) * mm});
            skLineSegment(sketch, "E800", {"start": v(80.82, -34.85) * mm, "end": v(80.8, -34.22) * mm});
            skLineSegment(sketch, "E801", {"start": v(80.8, -34.22) * mm, "end": v(80.71, -32.83) * mm});
            skLineSegment(sketch, "E802", {"start": v(80.71, -32.83) * mm, "end": v(80.52, -31.46) * mm});
            skLineSegment(sketch, "E803", {"start": v(80.52, -31.46) * mm, "end": v(80.44, -31) * mm});
            skLineSegment(sketch, "E804", {"start": v(80.44, -31) * mm, "end": v(80.4, -30.84) * mm});
            skLineSegment(sketch, "E805", {"start": v(80.4, -30.84) * mm, "end": v(81.14, -30.24) * mm});
            skLineSegment(sketch, "E806", {"start": v(81.14, -30.24) * mm, "end": v(82.7, -28.82) * mm});
            skLineSegment(sketch, "E807", {"start": v(82.7, -28.82) * mm, "end": v(84.18, -27.24) * mm});
            skLineSegment(sketch, "E808", {"start": v(84.18, -27.24) * mm, "end": v(84.82, -26.46) * mm});
            skLineSegment(sketch, "E809", {"start": v(84.82, -26.46) * mm, "end": v(84.56, -25.78) * mm});
            skLineSegment(sketch, "E810", {"start": v(84.56, -25.78) * mm, "end": v(83.92, -24.3) * mm});
            skLineSegment(sketch, "E811", {"start": v(83.92, -24.3) * mm, "end": v(82.81, -22.24) * mm});
            skLineSegment(sketch, "E812", {"start": v(82.81, -22.24) * mm, "end": v(82.53, -22.22) * mm});
            skLineSegment(sketch, "E813", {"start": v(82.53, -22.22) * mm, "end": v(81.78, -22.2) * mm});
            skLineSegment(sketch, "E814", {"start": v(81.78, -22.2) * mm, "end": v(79.55, -22.24) * mm});
            skLineSegment(sketch, "E815", {"start": v(79.55, -22.24) * mm, "end": v(78.4, -22.34) * mm});
            skLineSegment(sketch, "E816", {"start": v(78.4, -22.34) * mm, "end": v(77.39, -22.48) * mm});
            skLineSegment(sketch, "E817", {"start": v(77.39, -22.48) * mm, "end": v(76.43, -22.65) * mm});
            skLineSegment(sketch, "E818", {"start": v(76.43, -22.65) * mm, "end": v(75.93, -22.07) * mm});
            skLineSegment(sketch, "E819", {"start": v(75.93, -22.07) * mm, "end": v(75.49, -21.6) * mm});
            skLineSegment(sketch, "E820", {"start": v(75.49, -21.6) * mm, "end": v(74.96, -21.07) * mm});
            skLineSegment(sketch, "E821", {"start": v(74.96, -21.07) * mm, "end": v(73.93, -20.14) * mm});
            skLineSegment(sketch, "E822", {"start": v(73.93, -20.14) * mm, "end": v(73.44, -19.75) * mm});
            skLineSegment(sketch, "E823", {"start": v(73.44, -19.75) * mm, "end": v(73.63, -18.81) * mm});
            skLineSegment(sketch, "E824", {"start": v(73.63, -18.81) * mm, "end": v(73.91, -16.71) * mm});
            skLineSegment(sketch, "E825", {"start": v(73.91, -16.71) * mm, "end": v(74.03, -14.55) * mm});
            skLineSegment(sketch, "E826", {"start": v(74.03, -14.55) * mm, "end": v(74.02, -13.56) * mm});
            skLineSegment(sketch, "E827", {"start": v(74.02, -13.56) * mm, "end": v(73.38, -13.2) * mm});
            skLineSegment(sketch, "E828", {"start": v(73.38, -13.2) * mm, "end": v(71.94, -12.48) * mm});
            skLineSegment(sketch, "E829", {"start": v(71.94, -12.48) * mm, "end": v(69.77, -11.6) * mm});
            skLineSegment(sketch, "E830", {"start": v(69.77, -11.6) * mm, "end": v(68.95, -12.23) * mm});
            skLineSegment(sketch, "E831", {"start": v(68.95, -12.23) * mm, "end": v(67.27, -13.7) * mm});
            skLineSegment(sketch, "E832", {"start": v(67.27, -13.7) * mm, "end": v(65.77, -15.27) * mm});
            skLineSegment(sketch, "E833", {"start": v(65.77, -15.27) * mm, "end": v(65.14, -16.03) * mm});
            skLineSegment(sketch, "E834", {"start": v(65.14, -16.03) * mm, "end": v(65, -16) * mm});
            skLineSegment(sketch, "E835", {"start": v(65, -16) * mm, "end": v(63, -15.76) * mm});
            skLineSegment(sketch, "E836", {"start": v(63, -15.76) * mm, "end": v(62.26, -15.73) * mm});
            skLineSegment(sketch, "E837", {"start": v(62.26, -15.73) * mm, "end": v(61.62, -15.71) * mm});
            skLineSegment(sketch, "E838", {"start": v(61.62, -15.71) * mm, "end": v(60.98, -15.73) * mm});
            skLineSegment(sketch, "E839", {"start": v(60.98, -15.73) * mm, "end": v(60.86, -15.5) * mm});
            skLineSegment(sketch, "E840", {"start": v(60.86, -15.5) * mm, "end": v(60.53, -14.9) * mm});
            skLineSegment(sketch, "E841", {"start": v(60.53, -14.9) * mm, "end": v(59.4, -13.1) * mm});
            skLineSegment(sketch, "E842", {"start": v(59.4, -13.1) * mm, "end": v(58.1, -11.37) * mm});
            skLineSegment(sketch, "E843", {"start": v(58.1, -11.37) * mm, "end": v(57.45, -10.61) * mm});
            skLineSegment(sketch, "E844", {"start": v(57.45, -10.61) * mm, "end": v(56.73, -10.74) * mm});
            skLineSegment(sketch, "E845", {"start": v(56.73, -10.74) * mm, "end": v(55.16, -11.12) * mm});
            skLineSegment(sketch, "E846", {"start": v(55.16, -11.12) * mm, "end": v(54.34, -11.36) * mm});
            skLineSegment(sketch, "E847", {"start": v(54.34, -11.36) * mm, "end": v(53.62, -11.6) * mm});
            skLineSegment(sketch, "E848", {"start": v(53.62, -11.6) * mm, "end": v(52.94, -11.85) * mm});
            skLineSegment(sketch, "E849", {"start": v(52.94, -11.85) * mm, "end": v(52.37, -15.06) * mm});
            skLineSegment(sketch, "E850", {"start": v(52.37, -15.06) * mm, "end": v(52.23, -17.23) * mm});
            skLineSegment(sketch, "E851", {"start": v(52.23, -17.23) * mm, "end": v(52.24, -18.2) * mm});
            skLineSegment(sketch, "E852", {"start": v(52.24, -18.2) * mm, "end": v(52.12, -18.27) * mm});
            skLineSegment(sketch, "E853", {"start": v(52.12, -18.27) * mm, "end": v(50.43, -19.37) * mm});
            skLineSegment(sketch, "E854", {"start": v(50.43, -19.37) * mm, "end": v(49.84, -19.82) * mm});
            skLineSegment(sketch, "E855", {"start": v(49.84, -19.82) * mm, "end": v(49.33, -20.23) * mm});
            skLineSegment(sketch, "E856", {"start": v(49.33, -20.23) * mm, "end": v(48.86, -20.65) * mm});
            skLineSegment(sketch, "E857", {"start": v(48.86, -20.65) * mm, "end": v(47.97, -20.3) * mm});
            skLineSegment(sketch, "E858", {"start": v(47.97, -20.3) * mm, "end": v(45.95, -19.66) * mm});
            skLineSegment(sketch, "E859", {"start": v(45.95, -19.66) * mm, "end": v(43.85, -19.17) * mm});
            skLineSegment(sketch, "E860", {"start": v(43.85, -19.17) * mm, "end": v(42.86, -19) * mm});
            skLineSegment(sketch, "E861", {"start": v(42.86, -19) * mm, "end": v(42.4, -19.57) * mm});
            skLineSegment(sketch, "E862", {"start": v(42.4, -19.57) * mm, "end": v(41.94, -20.16) * mm});
            skLineSegment(sketch, "E863", {"start": v(41.94, -20.16) * mm, "end": v(41.44, -20.86) * mm});
            skLineSegment(sketch, "E864", {"start": v(41.44, -20.86) * mm, "end": v(40.57, -22.22) * mm});
            skLineSegment(sketch, "E865", {"start": v(40.57, -22.22) * mm, "end": v(40.2, -22.85) * mm});
            skLineSegment(sketch, "E866", {"start": v(40.2, -22.85) * mm, "end": v(40.68, -23.77) * mm});
            skLineSegment(sketch, "E867", {"start": v(40.68, -23.77) * mm, "end": v(41.83, -25.68) * mm});
            skLineSegment(sketch, "E868", {"start": v(41.83, -25.68) * mm, "end": v(43.12, -27.43) * mm});
            skLineSegment(sketch, "E869", {"start": v(43.12, -27.43) * mm, "end": v(43.74, -28.17) * mm});
            skLineSegment(sketch, "E870", {"start": v(43.74, -28.17) * mm, "end": v(43.7, -28.3) * mm});
            skLineSegment(sketch, "E871", {"start": v(43.7, -28.3) * mm, "end": v(43.5, -28.9) * mm});
            skLineSegment(sketch, "E872", {"start": v(43.5, -28.9) * mm, "end": v(43.3, -29.52) * mm});
            skLineSegment(sketch, "E873", {"start": v(43.3, -29.52) * mm, "end": v(43.1, -30.23) * mm});
            skLineSegment(sketch, "E874", {"start": v(43.1, -30.23) * mm, "end": v(42.94, -30.95) * mm});
            skLineSegment(sketch, "E875", {"start": v(42.94, -30.95) * mm, "end": v(42.83, -31.59) * mm});
            skLineSegment(sketch, "E876", {"start": v(42.83, -31.59) * mm, "end": v(42.73, -32.21) * mm});
            skLineSegment(sketch, "E877", {"start": v(42.73, -32.21) * mm, "end": v(41.83, -32.52) * mm});
            skLineSegment(sketch, "E878", {"start": v(41.83, -32.52) * mm, "end": v(39.87, -33.32) * mm});
            skLineSegment(sketch, "E879", {"start": v(39.87, -33.32) * mm, "end": v(37.94, -34.3) * mm});
            skLineSegment(sketch, "E880", {"start": v(37.94, -34.3) * mm, "end": v(37.08, -34.81) * mm});
            skLineSegment(sketch, "E881", {"start": v(37.08, -34.81) * mm, "end": v(37.1, -35.54) * mm});
            skLineSegment(sketch, "E882", {"start": v(37.1, -35.54) * mm, "end": v(37.19, -37.15) * mm});
            skLineSegment(sketch, "E883", {"start": v(37.19, -37.15) * mm, "end": v(37.39, -38.74) * mm});
            skLineSegment(sketch, "E884", {"start": v(37.39, -38.74) * mm, "end": v(37.52, -39.46) * mm});
            skLineSegment(sketch, "E885", {"start": v(37.52, -39.46) * mm, "end": v(37.77, -39.58) * mm});
            skLineSegment(sketch, "E886", {"start": v(37.77, -39.58) * mm, "end": v(38.47, -39.86) * mm});
            skLineSegment(sketch, "E887", {"start": v(38.47, -39.86) * mm, "end": v(40.58, -40.59) * mm});
            skLineSegment(sketch, "E888", {"start": v(40.58, -40.59) * mm, "end": v(42.7, -41.1) * mm});
            skLineSegment(sketch, "E889", {"start": v(42.7, -41.1) * mm, "end": v(43.65, -41.27) * mm});
            skLineSegment(sketch, "E890", {"start": v(43.65, -41.27) * mm, "end": v(43.7, -41.4) * mm});
            skLineSegment(sketch, "E891", {"start": v(52.54, 45.44) * mm, "end": v(52.5, 46.02) * mm});
            skLineSegment(sketch, "E892", {"start": v(52.5, 46.02) * mm, "end": v(52.35, 47.29) * mm});
            skLineSegment(sketch, "E893", {"start": v(52.35, 47.29) * mm, "end": v(52.2, 47.95) * mm});
            skLineSegment(sketch, "E894", {"start": v(52.2, 47.95) * mm, "end": v(52.03, 48.52) * mm});
            skLineSegment(sketch, "E895", {"start": v(52.03, 48.52) * mm, "end": v(51.83, 49.06) * mm});
            skLineSegment(sketch, "E896", {"start": v(51.83, 49.06) * mm, "end": v(52.01, 49.25) * mm});
            skLineSegment(sketch, "E897", {"start": v(52.01, 49.25) * mm, "end": v(52.47, 49.76) * mm});
            skLineSegment(sketch, "E898", {"start": v(52.47, 49.76) * mm, "end": v(53.72, 51.47) * mm});
            skLineSegment(sketch, "E899", {"start": v(53.72, 51.47) * mm, "end": v(54.73, 53.42) * mm});
            skLineSegment(sketch, "E900", {"start": v(54.73, 53.42) * mm, "end": v(55, 54.1) * mm});
            skLineSegment(sketch, "E901", {"start": v(55, 54.1) * mm, "end": v(55.1, 54.37) * mm});
            skLineSegment(sketch, "E902", {"start": v(55.1, 54.37) * mm, "end": v(54.61, 55.02) * mm});
            skLineSegment(sketch, "E903", {"start": v(54.61, 55.02) * mm, "end": v(54.06, 55.65) * mm});
            skLineSegment(sketch, "E904", {"start": v(54.06, 55.65) * mm, "end": v(53.4, 56.34) * mm});
            skLineSegment(sketch, "E905", {"start": v(53.4, 56.34) * mm, "end": v(52.05, 57.51) * mm});
            skLineSegment(sketch, "E906", {"start": v(52.05, 57.51) * mm, "end": v(51.4, 58) * mm});
            skLineSegment(sketch, "E907", {"start": v(51.4, 58) * mm, "end": v(51.11, 57.91) * mm});
            skLineSegment(sketch, "E908", {"start": v(51.11, 57.91) * mm, "end": v(50.39, 57.63) * mm});
            skLineSegment(sketch, "E909", {"start": v(50.39, 57.63) * mm, "end": v(48.35, 56.62) * mm});
            skLineSegment(sketch, "E910", {"start": v(48.35, 56.62) * mm, "end": v(46.6, 55.35) * mm});
            skLineSegment(sketch, "E911", {"start": v(46.6, 55.35) * mm, "end": v(45.89, 54.7) * mm});
            skLineSegment(sketch, "E912", {"start": v(45.89, 54.7) * mm, "end": v(45.77, 54.74) * mm});
            skLineSegment(sketch, "E913", {"start": v(45.77, 54.74) * mm, "end": v(45.62, 54.8) * mm});
            skLineSegment(sketch, "E914", {"start": v(45.62, 54.8) * mm, "end": v(44.64, 55.04) * mm});
            skLineSegment(sketch, "E915", {"start": v(44.64, 55.04) * mm, "end": v(43.96, 55.14) * mm});
            skLineSegment(sketch, "E916", {"start": v(43.96, 55.14) * mm, "end": v(43.28, 55.2) * mm});
            skLineSegment(sketch, "E917", {"start": v(43.28, 55.2) * mm, "end": v(42.68, 55.22) * mm});
            skLineSegment(sketch, "E918", {"start": v(42.68, 55.22) * mm, "end": v(42.1, 55.19) * mm});
            skLineSegment(sketch, "E919", {"start": v(42.1, 55.19) * mm, "end": v(41.64, 56.02) * mm});
            skLineSegment(sketch, "E920", {"start": v(41.64, 56.02) * mm, "end": v(40.4, 57.73) * mm});
            skLineSegment(sketch, "E921", {"start": v(40.4, 57.73) * mm, "end": v(38.86, 59.3) * mm});
            skLineSegment(sketch, "E922", {"start": v(38.86, 59.3) * mm, "end": v(38.3, 59.79) * mm});
            skLineSegment(sketch, "E923", {"start": v(38.3, 59.79) * mm, "end": v(38.07, 59.96) * mm});
            skLineSegment(sketch, "E924", {"start": v(38.07, 59.96) * mm, "end": v(37.3, 59.68) * mm});
            skLineSegment(sketch, "E925", {"start": v(37.3, 59.68) * mm, "end": v(35.66, 58.94) * mm});
            skLineSegment(sketch, "E926", {"start": v(35.66, 58.94) * mm, "end": v(34.83, 58.47) * mm});
            skLineSegment(sketch, "E927", {"start": v(34.83, 58.47) * mm, "end": v(34.12, 58.02) * mm});
            skLineSegment(sketch, "E928", {"start": v(34.12, 58.02) * mm, "end": v(33.47, 57.53) * mm});
            skLineSegment(sketch, "E929", {"start": v(33.47, 57.53) * mm, "end": v(33.47, 57.24) * mm});
            skLineSegment(sketch, "E930", {"start": v(33.47, 57.24) * mm, "end": v(33.5, 56.47) * mm});
            skLineSegment(sketch, "E931", {"start": v(33.5, 56.47) * mm, "end": v(33.84, 54.23) * mm});
            skLineSegment(sketch, "E932", {"start": v(33.84, 54.23) * mm, "end": v(34.5, 52.16) * mm});
            skLineSegment(sketch, "E933", {"start": v(34.5, 52.16) * mm, "end": v(34.9, 51.28) * mm});
            skLineSegment(sketch, "E934", {"start": v(34.9, 51.28) * mm, "end": v(34.63, 50.9) * mm});
            skLineSegment(sketch, "E935", {"start": v(34.63, 50.9) * mm, "end": v(34.2, 50.2) * mm});
            skLineSegment(sketch, "E936", {"start": v(34.2, 50.2) * mm, "end": v(33.74, 49.27) * mm});
            skLineSegment(sketch, "E937", {"start": v(33.74, 49.27) * mm, "end": v(33.42, 48.4) * mm});
            skLineSegment(sketch, "E938", {"start": v(33.42, 48.4) * mm, "end": v(33.27, 47.84) * mm});
            skLineSegment(sketch, "E939", {"start": v(33.27, 47.84) * mm, "end": v(32.34, 47.66) * mm});
            skLineSegment(sketch, "E940", {"start": v(32.34, 47.66) * mm, "end": v(30.33, 47) * mm});
            skLineSegment(sketch, "E941", {"start": v(30.33, 47) * mm, "end": v(29.78, 46.77) * mm});
            skLineSegment(sketch, "E942", {"start": v(29.78, 46.77) * mm, "end": v(29.27, 46.52) * mm});
            skLineSegment(sketch, "E943", {"start": v(29.27, 46.52) * mm, "end": v(28.37, 46.03) * mm});
            skLineSegment(sketch, "E944", {"start": v(28.37, 46.03) * mm, "end": v(27.49, 45.48) * mm});
            skLineSegment(sketch, "E945", {"start": v(27.49, 45.48) * mm, "end": v(27.5, 45.25) * mm});
            skLineSegment(sketch, "E946", {"start": v(27.5, 45.25) * mm, "end": v(27.57, 43.83) * mm});
            skLineSegment(sketch, "E947", {"start": v(27.57, 43.83) * mm, "end": v(27.8, 42.4) * mm});
            skLineSegment(sketch, "E948", {"start": v(27.8, 42.4) * mm, "end": v(28.11, 41.13) * mm});
            skLineSegment(sketch, "E949", {"start": v(28.11, 41.13) * mm, "end": v(28.3, 40.56) * mm});
            skLineSegment(sketch, "E950", {"start": v(28.3, 40.56) * mm, "end": v(28.37, 40.35) * mm});
            skLineSegment(sketch, "E951", {"start": v(28.37, 40.35) * mm, "end": v(29.4, 40.05) * mm});
            skLineSegment(sketch, "E952", {"start": v(29.4, 40.05) * mm, "end": v(31.63, 39.68) * mm});
            skLineSegment(sketch, "E953", {"start": v(31.63, 39.68) * mm, "end": v(32.8, 39.64) * mm});
            skLineSegment(sketch, "E954", {"start": v(32.8, 39.64) * mm, "end": v(33.8, 39.68) * mm});
            skLineSegment(sketch, "E955", {"start": v(33.8, 39.68) * mm, "end": v(34.5, 39.75) * mm});
            skLineSegment(sketch, "E956", {"start": v(34.5, 39.75) * mm, "end": v(34.76, 39.8) * mm});
            skLineSegment(sketch, "E957", {"start": v(34.76, 39.8) * mm, "end": v(35.18, 39.22) * mm});
            skLineSegment(sketch, "E958", {"start": v(35.18, 39.22) * mm, "end": v(35.8, 38.53) * mm});
            skLineSegment(sketch, "E959", {"start": v(35.8, 38.53) * mm, "end": v(36.57, 37.84) * mm});
            skLineSegment(sketch, "E960", {"start": v(36.57, 37.84) * mm, "end": v(37.05, 37.49) * mm});
            skLineSegment(sketch, "E961", {"start": v(37.05, 37.49) * mm, "end": v(37.4, 37.25) * mm});
            skLineSegment(sketch, "E962", {"start": v(37.4, 37.25) * mm, "end": v(37.53, 37.16) * mm});
            skLineSegment(sketch, "E963", {"start": v(37.53, 37.16) * mm, "end": v(37.42, 36.23) * mm});
            skLineSegment(sketch, "E964", {"start": v(37.42, 36.23) * mm, "end": v(37.42, 34.11) * mm});
            skLineSegment(sketch, "E965", {"start": v(37.42, 34.11) * mm, "end": v(37.54, 32.95) * mm});
            skLineSegment(sketch, "E966", {"start": v(37.54, 32.95) * mm, "end": v(37.74, 31.94) * mm});
            skLineSegment(sketch, "E967", {"start": v(37.74, 31.94) * mm, "end": v(38, 30.94) * mm});
            skLineSegment(sketch, "E968", {"start": v(38, 30.94) * mm, "end": v(38.2, 30.87) * mm});
            skLineSegment(sketch, "E969", {"start": v(38.2, 30.87) * mm, "end": v(39.6, 30.5) * mm});
            skLineSegment(sketch, "E970", {"start": v(39.6, 30.5) * mm, "end": v(40.54, 30.35) * mm});
            skLineSegment(sketch, "E971", {"start": v(40.54, 30.35) * mm, "end": v(42.32, 30.2) * mm});
            skLineSegment(sketch, "E972", {"start": v(42.32, 30.2) * mm, "end": v(42.91, 30.19) * mm});
            skLineSegment(sketch, "E973", {"start": v(42.91, 30.19) * mm, "end": v(43.14, 30.2) * mm});
            skLineSegment(sketch, "E974", {"start": v(43.14, 30.2) * mm, "end": v(43.73, 31.08) * mm});
            skLineSegment(sketch, "E975", {"start": v(43.73, 31.08) * mm, "end": v(44.27, 32) * mm});
            skLineSegment(sketch, "E976", {"start": v(44.27, 32) * mm, "end": v(44.78, 33.1) * mm});
            skLineSegment(sketch, "E977", {"start": v(44.78, 33.1) * mm, "end": v(45.46, 35.16) * mm});
            skLineSegment(sketch, "E978", {"start": v(45.46, 35.16) * mm, "end": v(45.65, 36.08) * mm});
            skLineSegment(sketch, "E979", {"start": v(45.65, 36.08) * mm, "end": v(46.58, 36.43) * mm});
            skLineSegment(sketch, "E980", {"start": v(46.58, 36.43) * mm, "end": v(47.47, 36.86) * mm});
            skLineSegment(sketch, "E981", {"start": v(47.47, 36.86) * mm, "end": v(48.54, 37.56) * mm});
            skLineSegment(sketch, "E982", {"start": v(48.54, 37.56) * mm, "end": v(48.88, 37.81) * mm});
            skLineSegment(sketch, "E983", {"start": v(48.88, 37.81) * mm, "end": v(49, 37.91) * mm});
            skLineSegment(sketch, "E984", {"start": v(49, 37.91) * mm, "end": v(49.85, 37.53) * mm});
            skLineSegment(sketch, "E985", {"start": v(49.85, 37.53) * mm, "end": v(51.87, 36.87) * mm});
            skLineSegment(sketch, "E986", {"start": v(51.87, 36.87) * mm, "end": v(54.03, 36.5) * mm});
            skLineSegment(sketch, "E987", {"start": v(54.03, 36.5) * mm, "end": v(55.05, 36.44) * mm});
            skLineSegment(sketch, "E988", {"start": v(55.05, 36.44) * mm, "end": v(55.19, 36.62) * mm});
            skLineSegment(sketch, "E989", {"start": v(55.19, 36.62) * mm, "end": v(55.52, 37.1) * mm});
            skLineSegment(sketch, "E990", {"start": v(55.52, 37.1) * mm, "end": v(56.4, 38.67) * mm});
            skLineSegment(sketch, "E991", {"start": v(56.4, 38.67) * mm, "end": v(56.82, 39.54) * mm});
            skLineSegment(sketch, "E992", {"start": v(56.82, 39.54) * mm, "end": v(57.31, 40.88) * mm});
            skLineSegment(sketch, "E993", {"start": v(57.31, 40.88) * mm, "end": v(57.37, 41.1) * mm});
            skLineSegment(sketch, "E994", {"start": v(57.37, 41.1) * mm, "end": v(56.7, 41.94) * mm});
            skLineSegment(sketch, "E995", {"start": v(56.7, 41.94) * mm, "end": v(56, 42.73) * mm});
            skLineSegment(sketch, "E996", {"start": v(56, 42.73) * mm, "end": v(55.11, 43.56) * mm});
            skLineSegment(sketch, "E997", {"start": v(55.11, 43.56) * mm, "end": v(54.2, 44.28) * mm});
            skLineSegment(sketch, "E998", {"start": v(54.2, 44.28) * mm, "end": v(53.36, 44.84) * mm});
            skLineSegment(sketch, "E999", {"start": v(53.36, 44.84) * mm, "end": v(52.53, 45.31) * mm});
            skLineSegment(sketch, "E1000", {"start": v(52.53, 45.31) * mm, "end": v(52.54, 45.44) * mm});
            skSolve(sketch);
        }
        {
            var Q0;
            Q0=makeQuery(id+"F0.imprint","IMPRINT",FACE,{"disambiguationData":[TD([[makeQuery(id+"F0.imprint","IMPRINT",EDGE,{"derivedFrom":sQuery(id+"F0.wireOp",EDGE,"E0")}),1.0]])]});
            extrude(context, id + "F1", {"entities" : qUnion([Q0]), "depth" : 4 * mm});
        }
        {
            var Q0;
            Q0=qCreatedBy(makeId("Top.planeOp"),FACE);
            var sketch = newSketch(context, id + "F2", { "sketchPlane" : qUnion([Q0])});
            skLineSegment(sketch, "E1001", {"start": v(23.91, -18.79) * mm, "end": v(26.6, -20.44) * mm});
            skLineSegment(sketch, "E1002", {"start": v(26.6, -20.44) * mm, "end": v(28.45, -21.67) * mm});
            skLineSegment(sketch, "E1003", {"start": v(28.45, -21.67) * mm, "end": v(29.26, -22.25) * mm});
            skLineSegment(sketch, "E1004", {"start": v(29.26, -22.25) * mm, "end": v(29.1, -24.4) * mm});
            skLineSegment(sketch, "E1005", {"start": v(29.1, -24.4) * mm, "end": v(28.83, -26.53) * mm});
            skLineSegment(sketch, "E1006", {"start": v(28.83, -26.53) * mm, "end": v(27.93, -26.88) * mm});
            skLineSegment(sketch, "E1007", {"start": v(27.93, -26.88) * mm, "end": v(25.9, -27.6) * mm});
            skLineSegment(sketch, "E1008", {"start": v(25.9, -27.6) * mm, "end": v(22.97, -28.54) * mm});
            skLineSegment(sketch, "E1009", {"start": v(22.97, -28.54) * mm, "end": v(22.85, -29.2) * mm});
            skLineSegment(sketch, "E1010", {"start": v(22.85, -29.2) * mm, "end": v(22.16, -32.08) * mm});
            skLineSegment(sketch, "E1011", {"start": v(22.16, -32.08) * mm, "end": v(21.94, -32.87) * mm});
            skLineSegment(sketch, "E1012", {"start": v(21.94, -32.87) * mm, "end": v(22.62, -33.58) * mm});
            skLineSegment(sketch, "E1013", {"start": v(22.62, -33.58) * mm, "end": v(24.1, -35.2) * mm});
            skLineSegment(sketch, "E1014", {"start": v(24.1, -35.2) * mm, "end": v(26.16, -37.65) * mm});
            skLineSegment(sketch, "E1015", {"start": v(26.16, -37.65) * mm, "end": v(25.94, -38.3) * mm});
            skLineSegment(sketch, "E1016", {"start": v(25.94, -38.3) * mm, "end": v(24.87, -41.04) * mm});
            skLineSegment(sketch, "E1017", {"start": v(24.87, -41.04) * mm, "end": v(24.6, -41.66) * mm});
            skLineSegment(sketch, "E1018", {"start": v(24.6, -41.66) * mm, "end": v(21.49, -41.9) * mm});
            skLineSegment(sketch, "E1019", {"start": v(21.49, -41.9) * mm, "end": v(19.36, -41.98) * mm});
            skLineSegment(sketch, "E1020", {"start": v(19.36, -41.98) * mm, "end": v(18.4, -42) * mm});
            skLineSegment(sketch, "E1021", {"start": v(18.4, -42) * mm, "end": v(17.4, -43.9) * mm});
            skLineSegment(sketch, "E1022", {"start": v(17.4, -43.9) * mm, "end": v(16.32, -45.77) * mm});
            skLineSegment(sketch, "E1023", {"start": v(16.32, -45.77) * mm, "end": v(16.24, -45.9) * mm});
            skLineSegment(sketch, "E1024", {"start": v(16.24, -45.9) * mm, "end": v(17.68, -48.7) * mm});
            skLineSegment(sketch, "E1025", {"start": v(17.68, -48.7) * mm, "end": v(18.61, -50.71) * mm});
            skLineSegment(sketch, "E1026", {"start": v(18.61, -50.71) * mm, "end": v(19, -51.64) * mm});
            skLineSegment(sketch, "E1027", {"start": v(19, -51.64) * mm, "end": v(17.75, -53.38) * mm});
            skLineSegment(sketch, "E1028", {"start": v(17.75, -53.38) * mm, "end": v(16.42, -55.07) * mm});
            skLineSegment(sketch, "E1029", {"start": v(16.42, -55.07) * mm, "end": v(15.46, -54.9) * mm});
            skLineSegment(sketch, "E1030", {"start": v(15.46, -54.9) * mm, "end": v(13.35, -54.46) * mm});
            skLineSegment(sketch, "E1031", {"start": v(13.35, -54.46) * mm, "end": v(10.37, -53.73) * mm});
            skLineSegment(sketch, "E1032", {"start": v(10.37, -53.73) * mm, "end": v(8.88, -55.3) * mm});
            skLineSegment(sketch, "E1033", {"start": v(8.88, -55.3) * mm, "end": v(7.23, -56.9) * mm});
            skLineSegment(sketch, "E1034", {"start": v(7.23, -56.9) * mm, "end": v(7.45, -57.86) * mm});
            skLineSegment(sketch, "E1035", {"start": v(7.45, -57.86) * mm, "end": v(7.86, -60) * mm});
            skLineSegment(sketch, "E1036", {"start": v(7.86, -60) * mm, "end": v(8.22, -62.18) * mm});
            skLineSegment(sketch, "E1037", {"start": v(8.22, -62.18) * mm, "end": v(8.36, -63.18) * mm});
            skLineSegment(sketch, "E1038", {"start": v(8.36, -63.18) * mm, "end": v(6.67, -64.5) * mm});
            skLineSegment(sketch, "E1039", {"start": v(6.67, -64.5) * mm, "end": v(5.48, -65.39) * mm});
            skLineSegment(sketch, "E1040", {"start": v(5.48, -65.39) * mm, "end": v(4.93, -65.78) * mm});
            skLineSegment(sketch, "E1041", {"start": v(4.93, -65.78) * mm, "end": v(4.05, -65.35) * mm});
            skLineSegment(sketch, "E1042", {"start": v(4.05, -65.35) * mm, "end": v(2.15, -64.38) * mm});
            skLineSegment(sketch, "E1043", {"start": v(2.15, -64.38) * mm, "end": v(-0.54, -62.86) * mm});
            skLineSegment(sketch, "E1044", {"start": v(-0.54, -62.86) * mm, "end": v(-1.1, -63.22) * mm});
            skLineSegment(sketch, "E1045", {"start": v(-1.1, -63.22) * mm, "end": v(-2.39, -63.97) * mm});
            skLineSegment(sketch, "E1046", {"start": v(-2.39, -63.97) * mm, "end": v(-4.28, -65) * mm});
            skLineSegment(sketch, "E1047", {"start": v(-4.28, -65) * mm, "end": v(-4.4, -65.06) * mm});
            skLineSegment(sketch, "E1048", {"start": v(-4.4, -65.06) * mm, "end": v(-4.46, -66.05) * mm});
            skLineSegment(sketch, "E1049", {"start": v(-4.46, -66.05) * mm, "end": v(-4.63, -68.24) * mm});
            skLineSegment(sketch, "E1050", {"start": v(-4.63, -68.24) * mm, "end": v(-5.02, -71.42) * mm});
            skLineSegment(sketch, "E1051", {"start": v(-5.02, -71.42) * mm, "end": v(-5.63, -71.7) * mm});
            skLineSegment(sketch, "E1052", {"start": v(-5.63, -71.7) * mm, "end": v(-8.38, -72.79) * mm});
            skLineSegment(sketch, "E1053", {"start": v(-8.38, -72.79) * mm, "end": v(-9.01, -73) * mm});
            skLineSegment(sketch, "E1054", {"start": v(-9.01, -73) * mm, "end": v(-11.32, -70.9) * mm});
            skLineSegment(sketch, "E1055", {"start": v(-11.32, -70.9) * mm, "end": v(-12.82, -69.41) * mm});
            skLineSegment(sketch, "E1056", {"start": v(-12.82, -69.41) * mm, "end": v(-13.5, -68.71) * mm});
            skLineSegment(sketch, "E1057", {"start": v(-13.5, -68.71) * mm, "end": v(-15.57, -69.29) * mm});
            skLineSegment(sketch, "E1058", {"start": v(-15.57, -69.29) * mm, "end": v(-17.81, -69.8) * mm});
            skLineSegment(sketch, "E1059", {"start": v(-17.81, -69.8) * mm, "end": v(-18.88, -72.77) * mm});
            skLineSegment(sketch, "E1060", {"start": v(-18.88, -72.77) * mm, "end": v(-19.72, -74.82) * mm});
            skLineSegment(sketch, "E1061", {"start": v(-19.72, -74.82) * mm, "end": v(-20.13, -75.74) * mm});
            skLineSegment(sketch, "E1062", {"start": v(-20.13, -75.74) * mm, "end": v(-22.26, -76) * mm});
            skLineSegment(sketch, "E1063", {"start": v(-22.26, -76) * mm, "end": v(-24.4, -76.18) * mm});
            skLineSegment(sketch, "E1064", {"start": v(-24.4, -76.18) * mm, "end": v(-24.93, -75.36) * mm});
            skLineSegment(sketch, "E1065", {"start": v(-24.93, -75.36) * mm, "end": v(-26.04, -73.53) * mm});
            skLineSegment(sketch, "E1066", {"start": v(-26.04, -73.53) * mm, "end": v(-27.55, -70.83) * mm});
            skLineSegment(sketch, "E1067", {"start": v(-27.55, -70.83) * mm, "end": v(-28.22, -70.85) * mm});
            skLineSegment(sketch, "E1068", {"start": v(-28.22, -70.85) * mm, "end": v(-31.19, -70.77) * mm});
            skLineSegment(sketch, "E1069", {"start": v(-31.19, -70.77) * mm, "end": v(-32, -70.7) * mm});
            skLineSegment(sketch, "E1070", {"start": v(-32, -70.7) * mm, "end": v(-33.84, -73.31) * mm});
            skLineSegment(sketch, "E1071", {"start": v(-33.84, -73.31) * mm, "end": v(-35.83, -75.82) * mm});
            skLineSegment(sketch, "E1072", {"start": v(-35.83, -75.82) * mm, "end": v(-37.17, -75.64) * mm});
            skLineSegment(sketch, "E1073", {"start": v(-37.17, -75.64) * mm, "end": v(-39.88, -75.16) * mm});
            skLineSegment(sketch, "E1074", {"start": v(-39.88, -75.16) * mm, "end": v(-40.06, -75.12) * mm});
            skLineSegment(sketch, "E1075", {"start": v(-40.06, -75.12) * mm, "end": v(-40.94, -72.11) * mm});
            skLineSegment(sketch, "E1076", {"start": v(-40.94, -72.11) * mm, "end": v(-41.46, -70.06) * mm});
            skLineSegment(sketch, "E1077", {"start": v(-41.46, -70.06) * mm, "end": v(-41.67, -69.12) * mm});
            skLineSegment(sketch, "E1078", {"start": v(-41.67, -69.12) * mm, "end": v(-43.74, -68.53) * mm});
            skLineSegment(sketch, "E1079", {"start": v(-43.74, -68.53) * mm, "end": v(-45.92, -67.8) * mm});
            skLineSegment(sketch, "E1080", {"start": v(-45.92, -67.8) * mm, "end": v(-46.68, -68.44) * mm});
            skLineSegment(sketch, "E1081", {"start": v(-46.68, -68.44) * mm, "end": v(-48.38, -69.78) * mm});
            skLineSegment(sketch, "E1082", {"start": v(-48.38, -69.78) * mm, "end": v(-50.16, -71.1) * mm});
            skLineSegment(sketch, "E1083", {"start": v(-50.16, -71.1) * mm, "end": v(-50.98, -71.68) * mm});
            skLineSegment(sketch, "E1084", {"start": v(-50.98, -71.68) * mm, "end": v(-52.94, -70.8) * mm});
            skLineSegment(sketch, "E1085", {"start": v(-52.94, -70.8) * mm, "end": v(-54.86, -69.84) * mm});
            skLineSegment(sketch, "E1086", {"start": v(-54.86, -69.84) * mm, "end": v(-54.89, -68.86) * mm});
            skLineSegment(sketch, "E1087", {"start": v(-54.89, -68.86) * mm, "end": v(-54.9, -66.72) * mm});
            skLineSegment(sketch, "E1088", {"start": v(-54.9, -66.72) * mm, "end": v(-54.78, -63.63) * mm});
            skLineSegment(sketch, "E1089", {"start": v(-54.78, -63.63) * mm, "end": v(-55.36, -63.3) * mm});
            skLineSegment(sketch, "E1090", {"start": v(-55.36, -63.3) * mm, "end": v(-57.85, -61.68) * mm});
            skLineSegment(sketch, "E1091", {"start": v(-57.85, -61.68) * mm, "end": v(-58.51, -61.2) * mm});
            skLineSegment(sketch, "E1092", {"start": v(-58.51, -61.2) * mm, "end": v(-59.41, -61.62) * mm});
            skLineSegment(sketch, "E1093", {"start": v(-59.41, -61.62) * mm, "end": v(-61.43, -62.47) * mm});
            skLineSegment(sketch, "E1094", {"start": v(-61.43, -62.47) * mm, "end": v(-64.44, -63.58) * mm});
            skLineSegment(sketch, "E1095", {"start": v(-64.44, -63.58) * mm, "end": v(-64.97, -63.17) * mm});
            skLineSegment(sketch, "E1096", {"start": v(-64.97, -63.17) * mm, "end": v(-67.2, -61.23) * mm});
            skLineSegment(sketch, "E1097", {"start": v(-67.2, -61.23) * mm, "end": v(-67.68, -60.76) * mm});
            skLineSegment(sketch, "E1098", {"start": v(-67.68, -60.76) * mm, "end": v(-66.88, -57.76) * mm});
            skLineSegment(sketch, "E1099", {"start": v(-66.88, -57.76) * mm, "end": v(-66.24, -55.72) * mm});
            skLineSegment(sketch, "E1100", {"start": v(-66.24, -55.72) * mm, "end": v(-65.93, -54.81) * mm});
            skLineSegment(sketch, "E1101", {"start": v(-65.93, -54.81) * mm, "end": v(-66.87, -53.82) * mm});
            skLineSegment(sketch, "E1102", {"start": v(-66.87, -53.82) * mm, "end": v(-68.37, -52.1) * mm});
            skLineSegment(sketch, "E1103", {"start": v(-68.37, -52.1) * mm, "end": v(-68.8, -51.59) * mm});
            skLineSegment(sketch, "E1104", {"start": v(-68.8, -51.59) * mm, "end": v(-68.88, -51.47) * mm});
            skLineSegment(sketch, "E1105", {"start": v(-68.88, -51.47) * mm, "end": v(-72.03, -51.9) * mm});
            skLineSegment(sketch, "E1106", {"start": v(-72.03, -51.9) * mm, "end": v(-74.22, -52.1) * mm});
            skLineSegment(sketch, "E1107", {"start": v(-74.22, -52.1) * mm, "end": v(-75.22, -52.16) * mm});
            skLineSegment(sketch, "E1108", {"start": v(-75.22, -52.16) * mm, "end": v(-75.61, -51.62) * mm});
            skLineSegment(sketch, "E1109", {"start": v(-75.61, -51.62) * mm, "end": v(-76.44, -50.4) * mm});
            skLineSegment(sketch, "E1110", {"start": v(-76.44, -50.4) * mm, "end": v(-77.6, -48.59) * mm});
            skLineSegment(sketch, "E1111", {"start": v(-77.6, -48.59) * mm, "end": v(-76, -45.9) * mm});
            skLineSegment(sketch, "E1112", {"start": v(-76, -45.9) * mm, "end": v(-74.85, -44.12) * mm});
            skLineSegment(sketch, "E1113", {"start": v(-74.85, -44.12) * mm, "end": v(-74.31, -43.32) * mm});
            skLineSegment(sketch, "E1114", {"start": v(-74.31, -43.32) * mm, "end": v(-75.3, -41.4) * mm});
            skLineSegment(sketch, "E1115", {"start": v(-75.3, -41.4) * mm, "end": v(-76.25, -39.31) * mm});
            skLineSegment(sketch, "E1116", {"start": v(-76.25, -39.31) * mm, "end": v(-77.23, -39.2) * mm});
            skLineSegment(sketch, "E1117", {"start": v(-77.23, -39.2) * mm, "end": v(-79.38, -38.87) * mm});
            skLineSegment(sketch, "E1118", {"start": v(-79.38, -38.87) * mm, "end": v(-81.56, -38.47) * mm});
            skLineSegment(sketch, "E1119", {"start": v(-81.56, -38.47) * mm, "end": v(-82.55, -38.27) * mm});
            skLineSegment(sketch, "E1120", {"start": v(-82.55, -38.27) * mm, "end": v(-83.23, -36.23) * mm});
            skLineSegment(sketch, "E1121", {"start": v(-83.23, -36.23) * mm, "end": v(-83.84, -34.17) * mm});
            skLineSegment(sketch, "E1122", {"start": v(-83.84, -34.17) * mm, "end": v(-83.15, -33.49) * mm});
            skLineSegment(sketch, "E1123", {"start": v(-83.15, -33.49) * mm, "end": v(-81.6, -32.02) * mm});
            skLineSegment(sketch, "E1124", {"start": v(-81.6, -32.02) * mm, "end": v(-79.25, -30) * mm});
            skLineSegment(sketch, "E1125", {"start": v(-79.25, -30) * mm, "end": v(-79.4, -29.34) * mm});
            skLineSegment(sketch, "E1126", {"start": v(-79.4, -29.34) * mm, "end": v(-79.93, -26.42) * mm});
            skLineSegment(sketch, "E1127", {"start": v(-79.93, -26.42) * mm, "end": v(-80.03, -25.61) * mm});
            skLineSegment(sketch, "E1128", {"start": v(-80.03, -25.61) * mm, "end": v(-82.95, -24.34) * mm});
            skLineSegment(sketch, "E1129", {"start": v(-82.95, -24.34) * mm, "end": v(-85.8, -22.9) * mm});
            skLineSegment(sketch, "E1130", {"start": v(-85.8, -22.9) * mm, "end": v(-85.9, -21.54) * mm});
            skLineSegment(sketch, "E1131", {"start": v(-85.9, -21.54) * mm, "end": v(-85.97, -18.61) * mm});
            skLineSegment(sketch, "E1132", {"start": v(-85.97, -18.61) * mm, "end": v(-83.2, -17.14) * mm});
            skLineSegment(sketch, "E1133", {"start": v(-83.2, -17.14) * mm, "end": v(-81.3, -16.22) * mm});
            skLineSegment(sketch, "E1134", {"start": v(-81.3, -16.22) * mm, "end": v(-80.43, -15.82) * mm});
            skLineSegment(sketch, "E1135", {"start": v(-80.43, -15.82) * mm, "end": v(-80.27, -13.67) * mm});
            skLineSegment(sketch, "E1136", {"start": v(-80.27, -13.67) * mm, "end": v(-80, -11.39) * mm});
            skLineSegment(sketch, "E1137", {"start": v(-80, -11.39) * mm, "end": v(-82.45, -9.38) * mm});
            skLineSegment(sketch, "E1138", {"start": v(-82.45, -9.38) * mm, "end": v(-84.84, -7.23) * mm});
            skLineSegment(sketch, "E1139", {"start": v(-84.84, -7.23) * mm, "end": v(-84.8, -7.04) * mm});
            skLineSegment(sketch, "E1140", {"start": v(-84.8, -7.04) * mm, "end": v(-84.37, -5.13) * mm});
            skLineSegment(sketch, "E1141", {"start": v(-84.37, -5.13) * mm, "end": v(-84, -3.7) * mm});
            skLineSegment(sketch, "E1142", {"start": v(-84, -3.7) * mm, "end": v(-83.83, -3.05) * mm});
            skLineSegment(sketch, "E1143", {"start": v(-83.83, -3.05) * mm, "end": v(-80.8, -2.38) * mm});
            skLineSegment(sketch, "E1144", {"start": v(-80.8, -2.38) * mm, "end": v(-77.74, -1.86) * mm});
            skLineSegment(sketch, "E1145", {"start": v(-77.74, -1.86) * mm, "end": v(-77.52, -1.23) * mm});
            skLineSegment(sketch, "E1146", {"start": v(-77.52, -1.23) * mm, "end": v(-77, 0.16) * mm});
            skLineSegment(sketch, "E1147", {"start": v(-77, 0.16) * mm, "end": v(-76.46, 1.54) * mm});
            skLineSegment(sketch, "E1148", {"start": v(-76.46, 1.54) * mm, "end": v(-76.13, 2.29) * mm});
            skLineSegment(sketch, "E1149", {"start": v(-76.13, 2.29) * mm, "end": v(-77.96, 4.89) * mm});
            skLineSegment(sketch, "E1150", {"start": v(-77.96, 4.89) * mm, "end": v(-79.13, 6.74) * mm});
            skLineSegment(sketch, "E1151", {"start": v(-79.13, 6.74) * mm, "end": v(-79.65, 7.6) * mm});
            skLineSegment(sketch, "E1152", {"start": v(-79.65, 7.6) * mm, "end": v(-79.03, 8.81) * mm});
            skLineSegment(sketch, "E1153", {"start": v(-79.03, 8.81) * mm, "end": v(-77.66, 11.2) * mm});
            skLineSegment(sketch, "E1154", {"start": v(-77.66, 11.2) * mm, "end": v(-77.57, 11.36) * mm});
            skLineSegment(sketch, "E1155", {"start": v(-77.57, 11.36) * mm, "end": v(-74.44, 11.17) * mm});
            skLineSegment(sketch, "E1156", {"start": v(-74.44, 11.17) * mm, "end": v(-72.34, 10.97) * mm});
            skLineSegment(sketch, "E1157", {"start": v(-72.34, 10.97) * mm, "end": v(-71.38, 10.85) * mm});
            skLineSegment(sketch, "E1158", {"start": v(-71.38, 10.85) * mm, "end": v(-70.13, 12.6) * mm});
            skLineSegment(sketch, "E1159", {"start": v(-70.13, 12.6) * mm, "end": v(-68.7, 14.42) * mm});
            skLineSegment(sketch, "E1160", {"start": v(-68.7, 14.42) * mm, "end": v(-69.05, 15.34) * mm});
            skLineSegment(sketch, "E1161", {"start": v(-69.05, 15.34) * mm, "end": v(-69.75, 17.4) * mm});
            skLineSegment(sketch, "E1162", {"start": v(-69.75, 17.4) * mm, "end": v(-70.4, 19.52) * mm});
            skLineSegment(sketch, "E1163", {"start": v(-70.4, 19.52) * mm, "end": v(-70.66, 20.48) * mm});
            skLineSegment(sketch, "E1164", {"start": v(-70.66, 20.48) * mm, "end": v(-69.18, 22.04) * mm});
            skLineSegment(sketch, "E1165", {"start": v(-69.18, 22.04) * mm, "end": v(-67.63, 23.52) * mm});
            skLineSegment(sketch, "E1166", {"start": v(-67.63, 23.52) * mm, "end": v(-64.68, 22.51) * mm});
            skLineSegment(sketch, "E1167", {"start": v(-64.68, 22.51) * mm, "end": v(-61.81, 21.38) * mm});
            skLineSegment(sketch, "E1168", {"start": v(-61.81, 21.38) * mm, "end": v(-61.67, 21.5) * mm});
            skLineSegment(sketch, "E1169", {"start": v(-61.67, 21.5) * mm, "end": v(-61.3, 21.8) * mm});
            skLineSegment(sketch, "E1170", {"start": v(-61.3, 21.8) * mm, "end": v(-59.5, 23.21) * mm});
            skLineSegment(sketch, "E1171", {"start": v(-59.5, 23.21) * mm, "end": v(-58.28, 24.09) * mm});
            skLineSegment(sketch, "E1172", {"start": v(-58.28, 24.09) * mm, "end": v(-58.44, 26.1) * mm});
            skLineSegment(sketch, "E1173", {"start": v(-58.44, 26.1) * mm, "end": v(-58.5, 27.25) * mm});
            skLineSegment(sketch, "E1174", {"start": v(-58.5, 27.25) * mm, "end": v(-58.54, 30.47) * mm});
            skLineSegment(sketch, "E1175", {"start": v(-58.54, 30.47) * mm, "end": v(-58.39, 30.57) * mm});
            skLineSegment(sketch, "E1176", {"start": v(-58.39, 30.57) * mm, "end": v(-57.97, 30.82) * mm});
            skLineSegment(sketch, "E1177", {"start": v(-57.97, 30.82) * mm, "end": v(-55.4, 32.27) * mm});
            skLineSegment(sketch, "E1178", {"start": v(-55.4, 32.27) * mm, "end": v(-54.8, 32.58) * mm});
            skLineSegment(sketch, "E1179", {"start": v(-54.8, 32.58) * mm, "end": v(-52.24, 30.82) * mm});
            skLineSegment(sketch, "E1180", {"start": v(-52.24, 30.82) * mm, "end": v(-50.53, 29.54) * mm});
            skLineSegment(sketch, "E1181", {"start": v(-50.53, 29.54) * mm, "end": v(-49.78, 28.94) * mm});
            skLineSegment(sketch, "E1182", {"start": v(-49.78, 28.94) * mm, "end": v(-48.53, 29.5) * mm});
            skLineSegment(sketch, "E1183", {"start": v(-48.53, 29.5) * mm, "end": v(-46.42, 30.33) * mm});
            skLineSegment(sketch, "E1184", {"start": v(-46.42, 30.33) * mm, "end": v(-45.96, 30.5) * mm});
            skLineSegment(sketch, "E1185", {"start": v(-45.96, 30.5) * mm, "end": v(-45.64, 30.6) * mm});
            skLineSegment(sketch, "E1186", {"start": v(-45.64, 30.6) * mm, "end": v(-45, 33.71) * mm});
            skLineSegment(sketch, "E1187", {"start": v(-45, 33.71) * mm, "end": v(-44.44, 35.84) * mm});
            skLineSegment(sketch, "E1188", {"start": v(-44.44, 35.84) * mm, "end": v(-44.17, 36.8) * mm});
            skLineSegment(sketch, "E1189", {"start": v(-44.17, 36.8) * mm, "end": v(-43.52, 36.99) * mm});
            skLineSegment(sketch, "E1190", {"start": v(-43.52, 36.99) * mm, "end": v(-42.1, 37.36) * mm});
            skLineSegment(sketch, "E1191", {"start": v(-42.1, 37.36) * mm, "end": v(-40, 37.85) * mm});
            skLineSegment(sketch, "E1192", {"start": v(-40, 37.85) * mm, "end": v(-39.36, 37.1) * mm});
            skLineSegment(sketch, "E1193", {"start": v(-39.36, 37.1) * mm, "end": v(-38, 35.43) * mm});
            skLineSegment(sketch, "E1194", {"start": v(-38, 35.43) * mm, "end": v(-36.71, 33.75) * mm});
            skLineSegment(sketch, "E1195", {"start": v(-36.71, 33.75) * mm, "end": v(-36.15, 32.98) * mm});
            skLineSegment(sketch, "E1196", {"start": v(-36.15, 32.98) * mm, "end": v(-34, 33.25) * mm});
            skLineSegment(sketch, "E1197", {"start": v(-34, 33.25) * mm, "end": v(-31.72, 33.44) * mm});
            skLineSegment(sketch, "E1198", {"start": v(-31.72, 33.44) * mm, "end": v(-30.25, 36.25) * mm});
            skLineSegment(sketch, "E1199", {"start": v(-30.25, 36.25) * mm, "end": v(-28.62, 39.03) * mm});
            skLineSegment(sketch, "E1200", {"start": v(-28.62, 39.03) * mm, "end": v(-27.95, 39.03) * mm});
            skLineSegment(sketch, "E1201", {"start": v(-27.95, 39.03) * mm, "end": v(-26.47, 39) * mm});
            skLineSegment(sketch, "E1202", {"start": v(-26.47, 39) * mm, "end": v(-24.33, 38.89) * mm});
            skLineSegment(sketch, "E1203", {"start": v(-24.33, 38.89) * mm, "end": v(-23.05, 36.05) * mm});
            skLineSegment(sketch, "E1204", {"start": v(-23.05, 36.05) * mm, "end": v(-22.26, 34.07) * mm});
            skLineSegment(sketch, "E1205", {"start": v(-22.26, 34.07) * mm, "end": v(-21.92, 33.17) * mm});
            skLineSegment(sketch, "E1206", {"start": v(-21.92, 33.17) * mm, "end": v(-21.26, 33.08) * mm});
            skLineSegment(sketch, "E1207", {"start": v(-21.26, 33.08) * mm, "end": v(-19.79, 32.87) * mm});
            skLineSegment(sketch, "E1208", {"start": v(-19.79, 32.87) * mm, "end": v(-17.85, 32.52) * mm});
            skLineSegment(sketch, "E1209", {"start": v(-17.85, 32.52) * mm, "end": v(-17.67, 32.48) * mm});
            skLineSegment(sketch, "E1210", {"start": v(-17.67, 32.48) * mm, "end": v(-17.53, 32.45) * mm});
            skLineSegment(sketch, "E1211", {"start": v(-17.53, 32.45) * mm, "end": v(-15.36, 34.76) * mm});
            skLineSegment(sketch, "E1212", {"start": v(-15.36, 34.76) * mm, "end": v(-13.05, 36.98) * mm});
            skLineSegment(sketch, "E1213", {"start": v(-13.05, 36.98) * mm, "end": v(-10.98, 36.39) * mm});
            skLineSegment(sketch, "E1214", {"start": v(-10.98, 36.39) * mm, "end": v(-8.95, 35.7) * mm});
            skLineSegment(sketch, "E1215", {"start": v(-8.95, 35.7) * mm, "end": v(-8.78, 34.74) * mm});
            skLineSegment(sketch, "E1216", {"start": v(-8.78, 34.74) * mm, "end": v(-8.5, 32.6) * mm});
            skLineSegment(sketch, "E1217", {"start": v(-8.5, 32.6) * mm, "end": v(-8.18, 29.55) * mm});
            skLineSegment(sketch, "E1218", {"start": v(-8.18, 29.55) * mm, "end": v(-8, 29.48) * mm});
            skLineSegment(sketch, "E1219", {"start": v(-8, 29.48) * mm, "end": v(-6.21, 28.67) * mm});
            skLineSegment(sketch, "E1220", {"start": v(-6.21, 28.67) * mm, "end": v(-4.88, 28.02) * mm});
            skLineSegment(sketch, "E1221", {"start": v(-4.88, 28.02) * mm, "end": v(-4.15, 27.65) * mm});
            skLineSegment(sketch, "E1222", {"start": v(-4.15, 27.65) * mm, "end": v(-3.31, 28.18) * mm});
            skLineSegment(sketch, "E1223", {"start": v(-3.31, 28.18) * mm, "end": v(-1.44, 29.29) * mm});
            skLineSegment(sketch, "E1224", {"start": v(-1.44, 29.29) * mm, "end": v(1.4, 30.8) * mm});
            skLineSegment(sketch, "E1225", {"start": v(1.4, 30.8) * mm, "end": v(1.97, 30.46) * mm});
            skLineSegment(sketch, "E1226", {"start": v(1.97, 30.46) * mm, "end": v(3.88, 29.23) * mm});
            skLineSegment(sketch, "E1227", {"start": v(3.88, 29.23) * mm, "end": v(4.99, 28.45) * mm});
            skLineSegment(sketch, "E1228", {"start": v(4.99, 28.45) * mm, "end": v(4.6, 25.37) * mm});
            skLineSegment(sketch, "E1229", {"start": v(4.6, 25.37) * mm, "end": v(4.06, 22.31) * mm});
            skLineSegment(sketch, "E1230", {"start": v(4.06, 22.31) * mm, "end": v(4.6, 21.9) * mm});
            skLineSegment(sketch, "E1231", {"start": v(4.6, 21.9) * mm, "end": v(6.84, 19.97) * mm});
            skLineSegment(sketch, "E1232", {"start": v(6.84, 19.97) * mm, "end": v(7.44, 19.4) * mm});
            skLineSegment(sketch, "E1233", {"start": v(7.44, 19.4) * mm, "end": v(10.5, 20.26) * mm});
            skLineSegment(sketch, "E1234", {"start": v(10.5, 20.26) * mm, "end": v(13.63, 20.95) * mm});
            skLineSegment(sketch, "E1235", {"start": v(13.63, 20.95) * mm, "end": v(14.09, 20.47) * mm});
            skLineSegment(sketch, "E1236", {"start": v(14.09, 20.47) * mm, "end": v(16.04, 18.25) * mm});
            skLineSegment(sketch, "E1237", {"start": v(16.04, 18.25) * mm, "end": v(16.35, 17.87) * mm});
            skLineSegment(sketch, "E1238", {"start": v(16.35, 17.87) * mm, "end": v(16.46, 17.73) * mm});
            skLineSegment(sketch, "E1239", {"start": v(16.46, 17.73) * mm, "end": v(15.25, 14.85) * mm});
            skLineSegment(sketch, "E1240", {"start": v(15.25, 14.85) * mm, "end": v(13.92, 12.06) * mm});
            skLineSegment(sketch, "E1241", {"start": v(13.92, 12.06) * mm, "end": v(15.16, 10.3) * mm});
            skLineSegment(sketch, "E1242", {"start": v(15.16, 10.3) * mm, "end": v(16.32, 8.48) * mm});
            skLineSegment(sketch, "E1243", {"start": v(16.32, 8.48) * mm, "end": v(16.4, 8.36) * mm});
            skLineSegment(sketch, "E1244", {"start": v(16.4, 8.36) * mm, "end": v(19.56, 8.35) * mm});
            skLineSegment(sketch, "E1245", {"start": v(19.56, 8.35) * mm, "end": v(21.77, 8.26) * mm});
            skLineSegment(sketch, "E1246", {"start": v(21.77, 8.26) * mm, "end": v(22.76, 8.18) * mm});
            skLineSegment(sketch, "E1247", {"start": v(22.76, 8.18) * mm, "end": v(23.74, 6.27) * mm});
            skLineSegment(sketch, "E1248", {"start": v(23.74, 6.27) * mm, "end": v(24.62, 4.3) * mm});
            skLineSegment(sketch, "E1249", {"start": v(24.62, 4.3) * mm, "end": v(24.04, 3.53) * mm});
            skLineSegment(sketch, "E1250", {"start": v(24.04, 3.53) * mm, "end": v(22.68, 1.86) * mm});
            skLineSegment(sketch, "E1251", {"start": v(22.68, 1.86) * mm, "end": v(20.65, -0.46) * mm});
            skLineSegment(sketch, "E1252", {"start": v(20.65, -0.46) * mm, "end": v(20.88, -1.09) * mm});
            skLineSegment(sketch, "E1253", {"start": v(20.88, -1.09) * mm, "end": v(21.36, -2.5) * mm});
            skLineSegment(sketch, "E1254", {"start": v(21.36, -2.5) * mm, "end": v(21.8, -3.9) * mm});
            skLineSegment(sketch, "E1255", {"start": v(21.8, -3.9) * mm, "end": v(22.02, -4.7) * mm});
            skLineSegment(sketch, "E1256", {"start": v(22.02, -4.7) * mm, "end": v(22.97, -4.95) * mm});
            skLineSegment(sketch, "E1257", {"start": v(22.97, -4.95) * mm, "end": v(25.07, -5.56) * mm});
            skLineSegment(sketch, "E1258", {"start": v(25.07, -5.56) * mm, "end": v(28.11, -6.6) * mm});
            skLineSegment(sketch, "E1259", {"start": v(28.11, -6.6) * mm, "end": v(28.15, -6.77) * mm});
            skLineSegment(sketch, "E1260", {"start": v(28.15, -6.77) * mm, "end": v(28.25, -7.25) * mm});
            skLineSegment(sketch, "E1261", {"start": v(28.25, -7.25) * mm, "end": v(28.51, -8.7) * mm});
            skLineSegment(sketch, "E1262", {"start": v(28.51, -8.7) * mm, "end": v(28.84, -10.83) * mm});
            skLineSegment(sketch, "E1263", {"start": v(28.84, -10.83) * mm, "end": v(26.32, -12.65) * mm});
            skLineSegment(sketch, "E1264", {"start": v(26.32, -12.65) * mm, "end": v(24.54, -13.82) * mm});
            skLineSegment(sketch, "E1265", {"start": v(24.54, -13.82) * mm, "end": v(23.72, -14.33) * mm});
            skLineSegment(sketch, "E1266", {"start": v(23.72, -14.33) * mm, "end": v(23.77, -15) * mm});
            skLineSegment(sketch, "E1267", {"start": v(23.77, -15) * mm, "end": v(23.86, -16.49) * mm});
            skLineSegment(sketch, "E1268", {"start": v(23.86, -16.49) * mm, "end": v(23.91, -18.64) * mm});
            skLineSegment(sketch, "E1269", {"start": v(23.91, -18.64) * mm, "end": v(23.91, -18.79) * mm});
            skLineSegment(sketch, "E1270", {"start": v(-28.36, -17.63) * mm, "end": v(-29.02, -17.9) * mm});
            skLineSegment(sketch, "E1271", {"start": v(-29.02, -17.9) * mm, "end": v(-29.3, -18.57) * mm});
            skLineSegment(sketch, "E1272", {"start": v(-29.3, -18.57) * mm, "end": v(-29.02, -19.24) * mm});
            skLineSegment(sketch, "E1273", {"start": v(-29.02, -19.24) * mm, "end": v(-28.36, -19.52) * mm});
            skLineSegment(sketch, "E1274", {"start": v(-28.36, -19.52) * mm, "end": v(-27.7, -19.24) * mm});
            skLineSegment(sketch, "E1275", {"start": v(-27.7, -19.24) * mm, "end": v(-27.42, -18.57) * mm});
            skLineSegment(sketch, "E1276", {"start": v(-27.42, -18.57) * mm, "end": v(-27.7, -17.9) * mm});
            skLineSegment(sketch, "E1277", {"start": v(-27.7, -17.9) * mm, "end": v(-28.36, -17.63) * mm});
            skLineSegment(sketch, "E1278", {"start": v(-40.68, 91.45) * mm, "end": v(-43.38, 93.06) * mm});
            skLineSegment(sketch, "E1279", {"start": v(-43.38, 93.06) * mm, "end": v(-45.2, 94.29) * mm});
            skLineSegment(sketch, "E1280", {"start": v(-45.2, 94.29) * mm, "end": v(-46, 94.88) * mm});
            skLineSegment(sketch, "E1281", {"start": v(-46, 94.88) * mm, "end": v(-45.78, 96.99) * mm});
            skLineSegment(sketch, "E1282", {"start": v(-45.78, 96.99) * mm, "end": v(-45.47, 99.09) * mm});
            skLineSegment(sketch, "E1283", {"start": v(-45.47, 99.09) * mm, "end": v(-44.54, 99.4) * mm});
            skLineSegment(sketch, "E1284", {"start": v(-44.54, 99.4) * mm, "end": v(-42.5, 100.02) * mm});
            skLineSegment(sketch, "E1285", {"start": v(-42.5, 100.02) * mm, "end": v(-39.53, 100.76) * mm});
            skLineSegment(sketch, "E1286", {"start": v(-39.53, 100.76) * mm, "end": v(-39.5, 100.93) * mm});
            skLineSegment(sketch, "E1287", {"start": v(-39.5, 100.93) * mm, "end": v(-39.37, 101.38) * mm});
            skLineSegment(sketch, "E1288", {"start": v(-39.37, 101.38) * mm, "end": v(-38.99, 102.75) * mm});
            skLineSegment(sketch, "E1289", {"start": v(-38.99, 102.75) * mm, "end": v(-38.34, 104.7) * mm});
            skLineSegment(sketch, "E1290", {"start": v(-38.34, 104.7) * mm, "end": v(-38.29, 104.84) * mm});
            skLineSegment(sketch, "E1291", {"start": v(-38.29, 104.84) * mm, "end": v(-40.27, 107.27) * mm});
            skLineSegment(sketch, "E1292", {"start": v(-40.27, 107.27) * mm, "end": v(-41.55, 109.05) * mm});
            skLineSegment(sketch, "E1293", {"start": v(-41.55, 109.05) * mm, "end": v(-42.1, 109.88) * mm});
            skLineSegment(sketch, "E1294", {"start": v(-42.1, 109.88) * mm, "end": v(-41.83, 110.49) * mm});
            skLineSegment(sketch, "E1295", {"start": v(-41.83, 110.49) * mm, "end": v(-41.18, 111.79) * mm});
            skLineSegment(sketch, "E1296", {"start": v(-41.18, 111.79) * mm, "end": v(-40.49, 113.08) * mm});
            skLineSegment(sketch, "E1297", {"start": v(-40.49, 113.08) * mm, "end": v(-40.16, 113.65) * mm});
            skLineSegment(sketch, "E1298", {"start": v(-40.16, 113.65) * mm, "end": v(-39.18, 113.63) * mm});
            skLineSegment(sketch, "E1299", {"start": v(-39.18, 113.63) * mm, "end": v(-37.05, 113.5) * mm});
            skLineSegment(sketch, "E1300", {"start": v(-37.05, 113.5) * mm, "end": v(-34.02, 113.18) * mm});
            skLineSegment(sketch, "E1301", {"start": v(-34.02, 113.18) * mm, "end": v(-32.81, 114.86) * mm});
            skLineSegment(sketch, "E1302", {"start": v(-32.81, 114.86) * mm, "end": v(-31.64, 116.34) * mm});
            skLineSegment(sketch, "E1303", {"start": v(-31.64, 116.34) * mm, "end": v(-31.43, 116.58) * mm});
            skLineSegment(sketch, "E1304", {"start": v(-31.43, 116.58) * mm, "end": v(-32.47, 119.56) * mm});
            skLineSegment(sketch, "E1305", {"start": v(-32.47, 119.56) * mm, "end": v(-33.3, 122.64) * mm});
            skLineSegment(sketch, "E1306", {"start": v(-33.3, 122.64) * mm, "end": v(-32.84, 123.1) * mm});
            skLineSegment(sketch, "E1307", {"start": v(-32.84, 123.1) * mm, "end": v(-31.78, 124.11) * mm});
            skLineSegment(sketch, "E1308", {"start": v(-31.78, 124.11) * mm, "end": v(-30.19, 125.51) * mm});
            skLineSegment(sketch, "E1309", {"start": v(-30.19, 125.51) * mm, "end": v(-29.28, 125.16) * mm});
            skLineSegment(sketch, "E1310", {"start": v(-29.28, 125.16) * mm, "end": v(-27.32, 124.31) * mm});
            skLineSegment(sketch, "E1311", {"start": v(-27.32, 124.31) * mm, "end": v(-25.42, 123.41) * mm});
            skLineSegment(sketch, "E1312", {"start": v(-25.42, 123.41) * mm, "end": v(-24.57, 122.97) * mm});
            skLineSegment(sketch, "E1313", {"start": v(-24.57, 122.97) * mm, "end": v(-23.5, 123.73) * mm});
            skLineSegment(sketch, "E1314", {"start": v(-23.5, 123.73) * mm, "end": v(-21.66, 124.9) * mm});
            skLineSegment(sketch, "E1315", {"start": v(-21.66, 124.9) * mm, "end": v(-20.98, 125.29) * mm});
            skLineSegment(sketch, "E1316", {"start": v(-20.98, 125.29) * mm, "end": v(-21, 126.27) * mm});
            skLineSegment(sketch, "E1317", {"start": v(-21, 126.27) * mm, "end": v(-20.98, 127.28) * mm});
            skLineSegment(sketch, "E1318", {"start": v(-20.98, 127.28) * mm, "end": v(-20.94, 128.43) * mm});
            skLineSegment(sketch, "E1319", {"start": v(-20.94, 128.43) * mm, "end": v(-20.79, 130.62) * mm});
            skLineSegment(sketch, "E1320", {"start": v(-20.79, 130.62) * mm, "end": v(-20.68, 131.62) * mm});
            skLineSegment(sketch, "E1321", {"start": v(-20.68, 131.62) * mm, "end": v(-18.74, 132.5) * mm});
            skLineSegment(sketch, "E1322", {"start": v(-18.74, 132.5) * mm, "end": v(-16.94, 133.2) * mm});
            skLineSegment(sketch, "E1323", {"start": v(-16.94, 133.2) * mm, "end": v(-16.76, 133.27) * mm});
            skLineSegment(sketch, "E1324", {"start": v(-16.76, 133.27) * mm, "end": v(-14.48, 131.15) * mm});
            skLineSegment(sketch, "E1325", {"start": v(-14.48, 131.15) * mm, "end": v(-13.68, 130.36) * mm});
            skLineSegment(sketch, "E1326", {"start": v(-13.68, 130.36) * mm, "end": v(-12.35, 128.94) * mm});
            skLineSegment(sketch, "E1327", {"start": v(-12.35, 128.94) * mm, "end": v(-11.73, 129.12) * mm});
            skLineSegment(sketch, "E1328", {"start": v(-11.73, 129.12) * mm, "end": v(-10.36, 129.46) * mm});
            skLineSegment(sketch, "E1329", {"start": v(-10.36, 129.46) * mm, "end": v(-8.97, 129.75) * mm});
            skLineSegment(sketch, "E1330", {"start": v(-8.97, 129.75) * mm, "end": v(-8.2, 129.9) * mm});
            skLineSegment(sketch, "E1331", {"start": v(-8.2, 129.9) * mm, "end": v(-7.07, 132.83) * mm});
            skLineSegment(sketch, "E1332", {"start": v(-7.07, 132.83) * mm, "end": v(-6.18, 134.83) * mm});
            skLineSegment(sketch, "E1333", {"start": v(-6.18, 134.83) * mm, "end": v(-5.73, 135.73) * mm});
            skLineSegment(sketch, "E1334", {"start": v(-5.73, 135.73) * mm, "end": v(-3.62, 135.88) * mm});
            skLineSegment(sketch, "E1335", {"start": v(-3.62, 135.88) * mm, "end": v(-1.5, 135.94) * mm});
            skLineSegment(sketch, "E1336", {"start": v(-1.5, 135.94) * mm, "end": v(-0.07, 133.17) * mm});
            skLineSegment(sketch, "E1337", {"start": v(-0.07, 133.17) * mm, "end": v(0.8, 131.25) * mm});
            skLineSegment(sketch, "E1338", {"start": v(0.8, 131.25) * mm, "end": v(1.17, 130.37) * mm});
            skLineSegment(sketch, "E1339", {"start": v(1.17, 130.37) * mm, "end": v(2.48, 130.27) * mm});
            skLineSegment(sketch, "E1340", {"start": v(2.48, 130.27) * mm, "end": v(4.64, 129.98) * mm});
            skLineSegment(sketch, "E1341", {"start": v(4.64, 129.98) * mm, "end": v(5.4, 129.84) * mm});
            skLineSegment(sketch, "E1342", {"start": v(5.4, 129.84) * mm, "end": v(6.03, 130.6) * mm});
            skLineSegment(sketch, "E1343", {"start": v(6.03, 130.6) * mm, "end": v(6.69, 131.37) * mm});
            skLineSegment(sketch, "E1344", {"start": v(6.69, 131.37) * mm, "end": v(7.46, 132.22) * mm});
            skLineSegment(sketch, "E1345", {"start": v(7.46, 132.22) * mm, "end": v(8.99, 133.8) * mm});
            skLineSegment(sketch, "E1346", {"start": v(8.99, 133.8) * mm, "end": v(9.71, 134.5) * mm});
            skLineSegment(sketch, "E1347", {"start": v(9.71, 134.5) * mm, "end": v(11.76, 133.93) * mm});
            skLineSegment(sketch, "E1348", {"start": v(11.76, 133.93) * mm, "end": v(13.77, 133.24) * mm});
            skLineSegment(sketch, "E1349", {"start": v(13.77, 133.24) * mm, "end": v(13.91, 132.27) * mm});
            skLineSegment(sketch, "E1350", {"start": v(13.91, 132.27) * mm, "end": v(14.16, 130.15) * mm});
            skLineSegment(sketch, "E1351", {"start": v(14.16, 130.15) * mm, "end": v(14.33, 128.05) * mm});
            skLineSegment(sketch, "E1352", {"start": v(14.33, 128.05) * mm, "end": v(14.37, 127.1) * mm});
            skLineSegment(sketch, "E1353", {"start": v(14.37, 127.1) * mm, "end": v(14.95, 126.83) * mm});
            skLineSegment(sketch, "E1354", {"start": v(14.95, 126.83) * mm, "end": v(16.23, 126.2) * mm});
            skLineSegment(sketch, "E1355", {"start": v(16.23, 126.2) * mm, "end": v(17.48, 125.54) * mm});
            skLineSegment(sketch, "E1356", {"start": v(17.48, 125.54) * mm, "end": v(18.16, 125.15) * mm});
            skLineSegment(sketch, "E1357", {"start": v(18.16, 125.15) * mm, "end": v(20.91, 126.68) * mm});
            skLineSegment(sketch, "E1358", {"start": v(20.91, 126.68) * mm, "end": v(22.89, 127.64) * mm});
            skLineSegment(sketch, "E1359", {"start": v(22.89, 127.64) * mm, "end": v(23.8, 128.04) * mm});
            skLineSegment(sketch, "E1360", {"start": v(23.8, 128.04) * mm, "end": v(25.52, 126.8) * mm});
            skLineSegment(sketch, "E1361", {"start": v(25.52, 126.8) * mm, "end": v(26.67, 125.9) * mm});
            skLineSegment(sketch, "E1362", {"start": v(26.67, 125.9) * mm, "end": v(27.04, 125.59) * mm});
            skLineSegment(sketch, "E1363", {"start": v(27.04, 125.59) * mm, "end": v(27.18, 125.47) * mm});
            skLineSegment(sketch, "E1364", {"start": v(27.18, 125.47) * mm, "end": v(26.5, 122.44) * mm});
            skLineSegment(sketch, "E1365", {"start": v(26.5, 122.44) * mm, "end": v(25.93, 120.4) * mm});
            skLineSegment(sketch, "E1366", {"start": v(25.93, 120.4) * mm, "end": v(25.64, 119.5) * mm});
            skLineSegment(sketch, "E1367", {"start": v(25.64, 119.5) * mm, "end": v(26.1, 119.05) * mm});
            skLineSegment(sketch, "E1368", {"start": v(26.1, 119.05) * mm, "end": v(27.1, 118.02) * mm});
            skLineSegment(sketch, "E1369", {"start": v(27.1, 118.02) * mm, "end": v(28.56, 116.37) * mm});
            skLineSegment(sketch, "E1370", {"start": v(28.56, 116.37) * mm, "end": v(29.51, 116.55) * mm});
            skLineSegment(sketch, "E1371", {"start": v(29.51, 116.55) * mm, "end": v(31.65, 116.87) * mm});
            skLineSegment(sketch, "E1372", {"start": v(31.65, 116.87) * mm, "end": v(32.82, 117) * mm});
            skLineSegment(sketch, "E1373", {"start": v(32.82, 117) * mm, "end": v(33.83, 117.1) * mm});
            skLineSegment(sketch, "E1374", {"start": v(33.83, 117.1) * mm, "end": v(34.83, 117.16) * mm});
            skLineSegment(sketch, "E1375", {"start": v(34.83, 117.16) * mm, "end": v(35.22, 116.62) * mm});
            skLineSegment(sketch, "E1376", {"start": v(35.22, 116.62) * mm, "end": v(36.02, 115.4) * mm});
            skLineSegment(sketch, "E1377", {"start": v(36.02, 115.4) * mm, "end": v(37.13, 113.6) * mm});
            skLineSegment(sketch, "E1378", {"start": v(37.13, 113.6) * mm, "end": v(36.62, 112.76) * mm});
            skLineSegment(sketch, "E1379", {"start": v(36.62, 112.76) * mm, "end": v(35.46, 110.98) * mm});
            skLineSegment(sketch, "E1380", {"start": v(35.46, 110.98) * mm, "end": v(33.66, 108.5) * mm});
            skLineSegment(sketch, "E1381", {"start": v(33.66, 108.5) * mm, "end": v(33.93, 107.92) * mm});
            skLineSegment(sketch, "E1382", {"start": v(33.93, 107.92) * mm, "end": v(34.52, 106.63) * mm});
            skLineSegment(sketch, "E1383", {"start": v(34.52, 106.63) * mm, "end": v(35.21, 104.87) * mm});
            skLineSegment(sketch, "E1384", {"start": v(35.21, 104.87) * mm, "end": v(35.28, 104.7) * mm});
            skLineSegment(sketch, "E1385", {"start": v(35.28, 104.7) * mm, "end": v(35.32, 104.57) * mm});
            skLineSegment(sketch, "E1386", {"start": v(35.32, 104.57) * mm, "end": v(38.4, 103.98) * mm});
            skLineSegment(sketch, "E1387", {"start": v(38.4, 103.98) * mm, "end": v(40.52, 103.45) * mm});
            skLineSegment(sketch, "E1388", {"start": v(40.52, 103.45) * mm, "end": v(41.5, 103.17) * mm});
            skLineSegment(sketch, "E1389", {"start": v(41.5, 103.17) * mm, "end": v(41.67, 102.53) * mm});
            skLineSegment(sketch, "E1390", {"start": v(41.67, 102.53) * mm, "end": v(42.18, 100.35) * mm});
            skLineSegment(sketch, "E1391", {"start": v(42.18, 100.35) * mm, "end": v(42.42, 99.02) * mm});
            skLineSegment(sketch, "E1392", {"start": v(42.42, 99.02) * mm, "end": v(41.66, 98.42) * mm});
            skLineSegment(sketch, "E1393", {"start": v(41.66, 98.42) * mm, "end": v(39.95, 97.14) * mm});
            skLineSegment(sketch, "E1394", {"start": v(39.95, 97.14) * mm, "end": v(37.41, 95.44) * mm});
            skLineSegment(sketch, "E1395", {"start": v(37.41, 95.44) * mm, "end": v(37.43, 95.26) * mm});
            skLineSegment(sketch, "E1396", {"start": v(37.43, 95.26) * mm, "end": v(37.57, 93.38) * mm});
            skLineSegment(sketch, "E1397", {"start": v(37.57, 93.38) * mm, "end": v(37.63, 91.31) * mm});
            skLineSegment(sketch, "E1398", {"start": v(37.63, 91.31) * mm, "end": v(37.62, 91.17) * mm});
            skLineSegment(sketch, "E1399", {"start": v(37.62, 91.17) * mm, "end": v(40.32, 89.56) * mm});
            skLineSegment(sketch, "E1400", {"start": v(40.32, 89.56) * mm, "end": v(42.13, 88.33) * mm});
            skLineSegment(sketch, "E1401", {"start": v(42.13, 88.33) * mm, "end": v(42.94, 87.74) * mm});
            skLineSegment(sketch, "E1402", {"start": v(42.94, 87.74) * mm, "end": v(42.73, 85.63) * mm});
            skLineSegment(sketch, "E1403", {"start": v(42.73, 85.63) * mm, "end": v(42.4, 83.53) * mm});
            skLineSegment(sketch, "E1404", {"start": v(42.4, 83.53) * mm, "end": v(41.48, 83.22) * mm});
            skLineSegment(sketch, "E1405", {"start": v(41.48, 83.22) * mm, "end": v(39.45, 82.6) * mm});
            skLineSegment(sketch, "E1406", {"start": v(39.45, 82.6) * mm, "end": v(36.47, 81.86) * mm});
            skLineSegment(sketch, "E1407", {"start": v(36.47, 81.86) * mm, "end": v(36.43, 81.7) * mm});
            skLineSegment(sketch, "E1408", {"start": v(36.43, 81.7) * mm, "end": v(36.32, 81.24) * mm});
            skLineSegment(sketch, "E1409", {"start": v(36.32, 81.24) * mm, "end": v(35.93, 79.87) * mm});
            skLineSegment(sketch, "E1410", {"start": v(35.93, 79.87) * mm, "end": v(35.28, 77.91) * mm});
            skLineSegment(sketch, "E1411", {"start": v(35.28, 77.91) * mm, "end": v(35.23, 77.78) * mm});
            skLineSegment(sketch, "E1412", {"start": v(35.23, 77.78) * mm, "end": v(37.2, 75.35) * mm});
            skLineSegment(sketch, "E1413", {"start": v(37.2, 75.35) * mm, "end": v(38.49, 73.57) * mm});
            skLineSegment(sketch, "E1414", {"start": v(38.49, 73.57) * mm, "end": v(39.05, 72.74) * mm});
            skLineSegment(sketch, "E1415", {"start": v(39.05, 72.74) * mm, "end": v(38.77, 72.14) * mm});
            skLineSegment(sketch, "E1416", {"start": v(38.77, 72.14) * mm, "end": v(38.12, 70.83) * mm});
            skLineSegment(sketch, "E1417", {"start": v(38.12, 70.83) * mm, "end": v(37.43, 69.55) * mm});
            skLineSegment(sketch, "E1418", {"start": v(37.43, 69.55) * mm, "end": v(37.1, 68.97) * mm});
            skLineSegment(sketch, "E1419", {"start": v(37.1, 68.97) * mm, "end": v(36.12, 69) * mm});
            skLineSegment(sketch, "E1420", {"start": v(36.12, 69) * mm, "end": v(34, 69.12) * mm});
            skLineSegment(sketch, "E1421", {"start": v(34, 69.12) * mm, "end": v(30.96, 69.44) * mm});
            skLineSegment(sketch, "E1422", {"start": v(30.96, 69.44) * mm, "end": v(29.75, 67.76) * mm});
            skLineSegment(sketch, "E1423", {"start": v(29.75, 67.76) * mm, "end": v(28.58, 66.28) * mm});
            skLineSegment(sketch, "E1424", {"start": v(28.58, 66.28) * mm, "end": v(28.37, 66.04) * mm});
            skLineSegment(sketch, "E1425", {"start": v(28.37, 66.04) * mm, "end": v(29.4, 63.07) * mm});
            skLineSegment(sketch, "E1426", {"start": v(29.4, 63.07) * mm, "end": v(30.25, 59.99) * mm});
            skLineSegment(sketch, "E1427", {"start": v(30.25, 59.99) * mm, "end": v(29.78, 59.52) * mm});
            skLineSegment(sketch, "E1428", {"start": v(29.78, 59.52) * mm, "end": v(28.72, 58.51) * mm});
            skLineSegment(sketch, "E1429", {"start": v(28.72, 58.51) * mm, "end": v(27.13, 57.1) * mm});
            skLineSegment(sketch, "E1430", {"start": v(27.13, 57.1) * mm, "end": v(26.22, 57.46) * mm});
            skLineSegment(sketch, "E1431", {"start": v(26.22, 57.46) * mm, "end": v(24.26, 58.3) * mm});
            skLineSegment(sketch, "E1432", {"start": v(24.26, 58.3) * mm, "end": v(22.36, 59.2) * mm});
            skLineSegment(sketch, "E1433", {"start": v(22.36, 59.2) * mm, "end": v(21.5, 59.65) * mm});
            skLineSegment(sketch, "E1434", {"start": v(21.5, 59.65) * mm, "end": v(20.44, 58.9) * mm});
            skLineSegment(sketch, "E1435", {"start": v(20.44, 58.9) * mm, "end": v(18.6, 57.72) * mm});
            skLineSegment(sketch, "E1436", {"start": v(18.6, 57.72) * mm, "end": v(17.92, 57.33) * mm});
            skLineSegment(sketch, "E1437", {"start": v(17.92, 57.33) * mm, "end": v(17.93, 56.35) * mm});
            skLineSegment(sketch, "E1438", {"start": v(17.93, 56.35) * mm, "end": v(17.93, 55.34) * mm});
            skLineSegment(sketch, "E1439", {"start": v(17.93, 55.34) * mm, "end": v(17.88, 54.19) * mm});
            skLineSegment(sketch, "E1440", {"start": v(17.88, 54.19) * mm, "end": v(17.73, 52) * mm});
            skLineSegment(sketch, "E1441", {"start": v(17.73, 52) * mm, "end": v(17.62, 51) * mm});
            skLineSegment(sketch, "E1442", {"start": v(17.62, 51) * mm, "end": v(15.68, 50.13) * mm});
            skLineSegment(sketch, "E1443", {"start": v(15.68, 50.13) * mm, "end": v(13.88, 49.42) * mm});
            skLineSegment(sketch, "E1444", {"start": v(13.88, 49.42) * mm, "end": v(13.7, 49.36) * mm});
            skLineSegment(sketch, "E1445", {"start": v(13.7, 49.36) * mm, "end": v(11.42, 51.47) * mm});
            skLineSegment(sketch, "E1446", {"start": v(11.42, 51.47) * mm, "end": v(10.62, 52.26) * mm});
            skLineSegment(sketch, "E1447", {"start": v(10.62, 52.26) * mm, "end": v(9.3, 53.68) * mm});
            skLineSegment(sketch, "E1448", {"start": v(9.3, 53.68) * mm, "end": v(8.67, 53.5) * mm});
            skLineSegment(sketch, "E1449", {"start": v(8.67, 53.5) * mm, "end": v(7.3, 53.16) * mm});
            skLineSegment(sketch, "E1450", {"start": v(7.3, 53.16) * mm, "end": v(5.9, 52.87) * mm});
            skLineSegment(sketch, "E1451", {"start": v(5.9, 52.87) * mm, "end": v(5.14, 52.73) * mm});
            skLineSegment(sketch, "E1452", {"start": v(5.14, 52.73) * mm, "end": v(4.01, 49.8) * mm});
            skLineSegment(sketch, "E1453", {"start": v(4.01, 49.8) * mm, "end": v(3.12, 47.79) * mm});
            skLineSegment(sketch, "E1454", {"start": v(3.12, 47.79) * mm, "end": v(2.68, 46.89) * mm});
            skLineSegment(sketch, "E1455", {"start": v(2.68, 46.89) * mm, "end": v(0.56, 46.74) * mm});
            skLineSegment(sketch, "E1456", {"start": v(0.56, 46.74) * mm, "end": v(-1.56, 46.69) * mm});
            skLineSegment(sketch, "E1457", {"start": v(-1.56, 46.69) * mm, "end": v(-3, 49.46) * mm});
            skLineSegment(sketch, "E1458", {"start": v(-3, 49.46) * mm, "end": v(-3.86, 51.37) * mm});
            skLineSegment(sketch, "E1459", {"start": v(-3.86, 51.37) * mm, "end": v(-4.23, 52.26) * mm});
            skLineSegment(sketch, "E1460", {"start": v(-4.23, 52.26) * mm, "end": v(-5.54, 52.35) * mm});
            skLineSegment(sketch, "E1461", {"start": v(-5.54, 52.35) * mm, "end": v(-7.7, 52.64) * mm});
            skLineSegment(sketch, "E1462", {"start": v(-7.7, 52.64) * mm, "end": v(-8.47, 52.78) * mm});
            skLineSegment(sketch, "E1463", {"start": v(-8.47, 52.78) * mm, "end": v(-9.1, 52.02) * mm});
            skLineSegment(sketch, "E1464", {"start": v(-9.1, 52.02) * mm, "end": v(-9.75, 51.25) * mm});
            skLineSegment(sketch, "E1465", {"start": v(-9.75, 51.25) * mm, "end": v(-10.52, 50.4) * mm});
            skLineSegment(sketch, "E1466", {"start": v(-10.52, 50.4) * mm, "end": v(-12.05, 48.82) * mm});
            skLineSegment(sketch, "E1467", {"start": v(-12.05, 48.82) * mm, "end": v(-12.77, 48.12) * mm});
            skLineSegment(sketch, "E1468", {"start": v(-12.77, 48.12) * mm, "end": v(-14.81, 48.7) * mm});
            skLineSegment(sketch, "E1469", {"start": v(-14.81, 48.7) * mm, "end": v(-16.83, 49.38) * mm});
            skLineSegment(sketch, "E1470", {"start": v(-16.83, 49.38) * mm, "end": v(-16.97, 50.35) * mm});
            skLineSegment(sketch, "E1471", {"start": v(-16.97, 50.35) * mm, "end": v(-17.22, 52.47) * mm});
            skLineSegment(sketch, "E1472", {"start": v(-17.22, 52.47) * mm, "end": v(-17.38, 54.57) * mm});
            skLineSegment(sketch, "E1473", {"start": v(-17.38, 54.57) * mm, "end": v(-17.43, 55.53) * mm});
            skLineSegment(sketch, "E1474", {"start": v(-17.43, 55.53) * mm, "end": v(-18.01, 55.8) * mm});
            skLineSegment(sketch, "E1475", {"start": v(-18.01, 55.8) * mm, "end": v(-19.29, 56.42) * mm});
            skLineSegment(sketch, "E1476", {"start": v(-19.29, 56.42) * mm, "end": v(-20.54, 57.08) * mm});
            skLineSegment(sketch, "E1477", {"start": v(-20.54, 57.08) * mm, "end": v(-21.22, 57.47) * mm});
            skLineSegment(sketch, "E1478", {"start": v(-21.22, 57.47) * mm, "end": v(-23.97, 55.94) * mm});
            skLineSegment(sketch, "E1479", {"start": v(-23.97, 55.94) * mm, "end": v(-25.95, 54.98) * mm});
            skLineSegment(sketch, "E1480", {"start": v(-25.95, 54.98) * mm, "end": v(-26.86, 54.58) * mm});
            skLineSegment(sketch, "E1481", {"start": v(-26.86, 54.58) * mm, "end": v(-28.58, 55.82) * mm});
            skLineSegment(sketch, "E1482", {"start": v(-28.58, 55.82) * mm, "end": v(-29.73, 56.73) * mm});
            skLineSegment(sketch, "E1483", {"start": v(-29.73, 56.73) * mm, "end": v(-30.1, 57.03) * mm});
            skLineSegment(sketch, "E1484", {"start": v(-30.1, 57.03) * mm, "end": v(-30.24, 57.15) * mm});
            skLineSegment(sketch, "E1485", {"start": v(-30.24, 57.15) * mm, "end": v(-29.56, 60.18) * mm});
            skLineSegment(sketch, "E1486", {"start": v(-29.56, 60.18) * mm, "end": v(-28.98, 62.22) * mm});
            skLineSegment(sketch, "E1487", {"start": v(-28.98, 62.22) * mm, "end": v(-28.7, 63.13) * mm});
            skLineSegment(sketch, "E1488", {"start": v(-28.7, 63.13) * mm, "end": v(-29.17, 63.57) * mm});
            skLineSegment(sketch, "E1489", {"start": v(-29.17, 63.57) * mm, "end": v(-30.15, 64.6) * mm});
            skLineSegment(sketch, "E1490", {"start": v(-30.15, 64.6) * mm, "end": v(-31.61, 66.25) * mm});
            skLineSegment(sketch, "E1491", {"start": v(-31.61, 66.25) * mm, "end": v(-32.57, 66.07) * mm});
            skLineSegment(sketch, "E1492", {"start": v(-32.57, 66.07) * mm, "end": v(-34.71, 65.75) * mm});
            skLineSegment(sketch, "E1493", {"start": v(-34.71, 65.75) * mm, "end": v(-35.88, 65.61) * mm});
            skLineSegment(sketch, "E1494", {"start": v(-35.88, 65.61) * mm, "end": v(-36.9, 65.53) * mm});
            skLineSegment(sketch, "E1495", {"start": v(-36.9, 65.53) * mm, "end": v(-37.9, 65.46) * mm});
            skLineSegment(sketch, "E1496", {"start": v(-37.9, 65.46) * mm, "end": v(-38.28, 66) * mm});
            skLineSegment(sketch, "E1497", {"start": v(-38.28, 66) * mm, "end": v(-39.08, 67.21) * mm});
            skLineSegment(sketch, "E1498", {"start": v(-39.08, 67.21) * mm, "end": v(-40.19, 69.03) * mm});
            skLineSegment(sketch, "E1499", {"start": v(-40.19, 69.03) * mm, "end": v(-39.68, 69.86) * mm});
            skLineSegment(sketch, "E1500", {"start": v(-39.68, 69.86) * mm, "end": v(-38.52, 71.64) * mm});
            skLineSegment(sketch, "E1501", {"start": v(-38.52, 71.64) * mm, "end": v(-36.72, 74.12) * mm});
            skLineSegment(sketch, "E1502", {"start": v(-36.72, 74.12) * mm, "end": v(-37, 74.7) * mm});
            skLineSegment(sketch, "E1503", {"start": v(-37, 74.7) * mm, "end": v(-37.58, 76) * mm});
            skLineSegment(sketch, "E1504", {"start": v(-37.58, 76) * mm, "end": v(-38.27, 77.75) * mm});
            skLineSegment(sketch, "E1505", {"start": v(-38.27, 77.75) * mm, "end": v(-38.34, 77.91) * mm});
            skLineSegment(sketch, "E1506", {"start": v(-38.34, 77.91) * mm, "end": v(-38.38, 78.05) * mm});
            skLineSegment(sketch, "E1507", {"start": v(-38.38, 78.05) * mm, "end": v(-41.47, 78.64) * mm});
            skLineSegment(sketch, "E1508", {"start": v(-41.47, 78.64) * mm, "end": v(-43.58, 79.18) * mm});
            skLineSegment(sketch, "E1509", {"start": v(-43.58, 79.18) * mm, "end": v(-44.55, 79.45) * mm});
            skLineSegment(sketch, "E1510", {"start": v(-44.55, 79.45) * mm, "end": v(-44.73, 80.1) * mm});
            skLineSegment(sketch, "E1511", {"start": v(-44.73, 80.1) * mm, "end": v(-45.24, 82.27) * mm});
            skLineSegment(sketch, "E1512", {"start": v(-45.24, 82.27) * mm, "end": v(-45.48, 83.6) * mm});
            skLineSegment(sketch, "E1513", {"start": v(-45.48, 83.6) * mm, "end": v(-44.72, 84.2) * mm});
            skLineSegment(sketch, "E1514", {"start": v(-44.72, 84.2) * mm, "end": v(-43, 85.48) * mm});
            skLineSegment(sketch, "E1515", {"start": v(-43, 85.48) * mm, "end": v(-40.47, 87.18) * mm});
            skLineSegment(sketch, "E1516", {"start": v(-40.47, 87.18) * mm, "end": v(-40.49, 87.36) * mm});
            skLineSegment(sketch, "E1517", {"start": v(-40.49, 87.36) * mm, "end": v(-40.63, 89.24) * mm});
            skLineSegment(sketch, "E1518", {"start": v(-40.63, 89.24) * mm, "end": v(-40.69, 91.31) * mm});
            skLineSegment(sketch, "E1519", {"start": v(-40.69, 91.31) * mm, "end": v(-40.68, 91.45) * mm});
            skLineSegment(sketch, "E1520", {"start": v(-1.53, 92.43) * mm, "end": v(-2.32, 92.1) * mm});
            skLineSegment(sketch, "E1521", {"start": v(-2.32, 92.1) * mm, "end": v(-2.65, 91.31) * mm});
            skLineSegment(sketch, "E1522", {"start": v(-2.65, 91.31) * mm, "end": v(-2.32, 90.52) * mm});
            skLineSegment(sketch, "E1523", {"start": v(-2.32, 90.52) * mm, "end": v(-1.53, 90.2) * mm});
            skLineSegment(sketch, "E1524", {"start": v(-1.53, 90.2) * mm, "end": v(-0.74, 90.52) * mm});
            skLineSegment(sketch, "E1525", {"start": v(-0.74, 90.52) * mm, "end": v(-0.41, 91.31) * mm});
            skLineSegment(sketch, "E1526", {"start": v(-0.41, 91.31) * mm, "end": v(-0.74, 92.1) * mm});
            skLineSegment(sketch, "E1527", {"start": v(-0.74, 92.1) * mm, "end": v(-1.53, 92.43) * mm});
            skLineSegment(sketch, "E1528", {"start": v(56.84, -103.62) * mm, "end": v(57.68, -104.09) * mm});
            skLineSegment(sketch, "E1529", {"start": v(57.68, -104.09) * mm, "end": v(59.52, -105.2) * mm});
            skLineSegment(sketch, "E1530", {"start": v(59.52, -105.2) * mm, "end": v(61.31, -106.46) * mm});
            skLineSegment(sketch, "E1531", {"start": v(61.31, -106.46) * mm, "end": v(62.1, -107.08) * mm});
            skLineSegment(sketch, "E1532", {"start": v(62.1, -107.08) * mm, "end": v(61.94, -108.42) * mm});
            skLineSegment(sketch, "E1533", {"start": v(61.94, -108.42) * mm, "end": v(61.66, -109.97) * mm});
            skLineSegment(sketch, "E1534", {"start": v(61.66, -109.97) * mm, "end": v(61.36, -111.29) * mm});
            skLineSegment(sketch, "E1535", {"start": v(61.36, -111.29) * mm, "end": v(60.42, -111.53) * mm});
            skLineSegment(sketch, "E1536", {"start": v(60.42, -111.53) * mm, "end": v(58.34, -111.99) * mm});
            skLineSegment(sketch, "E1537", {"start": v(58.34, -111.99) * mm, "end": v(56.26, -112.31) * mm});
            skLineSegment(sketch, "E1538", {"start": v(56.26, -112.31) * mm, "end": v(55.32, -112.42) * mm});
            skLineSegment(sketch, "E1539", {"start": v(55.32, -112.42) * mm, "end": v(55.27, -112.58) * mm});
            skLineSegment(sketch, "E1540", {"start": v(55.27, -112.58) * mm, "end": v(55.12, -113) * mm});
            skLineSegment(sketch, "E1541", {"start": v(55.12, -113) * mm, "end": v(54.6, -114.25) * mm});
            skLineSegment(sketch, "E1542", {"start": v(54.6, -114.25) * mm, "end": v(53.75, -116.03) * mm});
            skLineSegment(sketch, "E1543", {"start": v(53.75, -116.03) * mm, "end": v(53.7, -116.15) * mm});
            skLineSegment(sketch, "E1544", {"start": v(53.7, -116.15) * mm, "end": v(54.23, -116.95) * mm});
            skLineSegment(sketch, "E1545", {"start": v(54.23, -116.95) * mm, "end": v(55.33, -118.8) * mm});
            skLineSegment(sketch, "E1546", {"start": v(55.33, -118.8) * mm, "end": v(56.75, -121.66) * mm});
            skLineSegment(sketch, "E1547", {"start": v(56.75, -121.66) * mm, "end": v(56.36, -122.2) * mm});
            skLineSegment(sketch, "E1548", {"start": v(56.36, -122.2) * mm, "end": v(55.49, -123.39) * mm});
            skLineSegment(sketch, "E1549", {"start": v(55.49, -123.39) * mm, "end": v(54.56, -124.53) * mm});
            skLineSegment(sketch, "E1550", {"start": v(54.56, -124.53) * mm, "end": v(54.12, -125.03) * mm});
            skLineSegment(sketch, "E1551", {"start": v(54.12, -125.03) * mm, "end": v(53.17, -124.81) * mm});
            skLineSegment(sketch, "E1552", {"start": v(53.17, -124.81) * mm, "end": v(51.12, -124.24) * mm});
            skLineSegment(sketch, "E1553", {"start": v(51.12, -124.24) * mm, "end": v(49.13, -123.57) * mm});
            skLineSegment(sketch, "E1554", {"start": v(49.13, -123.57) * mm, "end": v(48.25, -123.23) * mm});
            skLineSegment(sketch, "E1555", {"start": v(48.25, -123.23) * mm, "end": v(48.13, -123.34) * mm});
            skLineSegment(sketch, "E1556", {"start": v(48.13, -123.34) * mm, "end": v(47.8, -123.64) * mm});
            skLineSegment(sketch, "E1557", {"start": v(47.8, -123.64) * mm, "end": v(46.76, -124.52) * mm});
            skLineSegment(sketch, "E1558", {"start": v(46.76, -124.52) * mm, "end": v(45.68, -125.34) * mm});
            skLineSegment(sketch, "E1559", {"start": v(45.68, -125.34) * mm, "end": v(45.07, -125.77) * mm});
            skLineSegment(sketch, "E1560", {"start": v(45.07, -125.77) * mm, "end": v(45.17, -126.74) * mm});
            skLineSegment(sketch, "E1561", {"start": v(45.17, -126.74) * mm, "end": v(45.3, -128.89) * mm});
            skLineSegment(sketch, "E1562", {"start": v(45.3, -128.89) * mm, "end": v(45.28, -131.07) * mm});
            skLineSegment(sketch, "E1563", {"start": v(45.28, -131.07) * mm, "end": v(45.24, -131.8) * mm});
            skLineSegment(sketch, "E1564", {"start": v(45.24, -131.8) * mm, "end": v(45.23, -132.08) * mm});
            skLineSegment(sketch, "E1565", {"start": v(45.23, -132.08) * mm, "end": v(44.63, -132.38) * mm});
            skLineSegment(sketch, "E1566", {"start": v(44.63, -132.38) * mm, "end": v(43.3, -133.02) * mm});
            skLineSegment(sketch, "E1567", {"start": v(43.3, -133.02) * mm, "end": v(41.96, -133.6) * mm});
            skLineSegment(sketch, "E1568", {"start": v(41.96, -133.6) * mm, "end": v(41.33, -133.85) * mm});
            skLineSegment(sketch, "E1569", {"start": v(41.33, -133.85) * mm, "end": v(40.6, -133.21) * mm});
            skLineSegment(sketch, "E1570", {"start": v(40.6, -133.21) * mm, "end": v(39.04, -131.76) * mm});
            skLineSegment(sketch, "E1571", {"start": v(39.04, -131.76) * mm, "end": v(37.6, -130.23) * mm});
            skLineSegment(sketch, "E1572", {"start": v(37.6, -130.23) * mm, "end": v(36.98, -129.52) * mm});
            skLineSegment(sketch, "E1573", {"start": v(36.98, -129.52) * mm, "end": v(36.81, -129.57) * mm});
            skLineSegment(sketch, "E1574", {"start": v(36.81, -129.57) * mm, "end": v(36.38, -129.68) * mm});
            skLineSegment(sketch, "E1575", {"start": v(36.38, -129.68) * mm, "end": v(35.06, -129.97) * mm});
            skLineSegment(sketch, "E1576", {"start": v(35.06, -129.97) * mm, "end": v(33.72, -130.2) * mm});
            skLineSegment(sketch, "E1577", {"start": v(33.72, -130.2) * mm, "end": v(32.98, -130.29) * mm});
            skLineSegment(sketch, "E1578", {"start": v(32.98, -130.29) * mm, "end": v(32.62, -131.2) * mm});
            skLineSegment(sketch, "E1579", {"start": v(32.62, -131.2) * mm, "end": v(31.72, -133.15) * mm});
            skLineSegment(sketch, "E1580", {"start": v(31.72, -133.15) * mm, "end": v(30.7, -135.07) * mm});
            skLineSegment(sketch, "E1581", {"start": v(30.7, -135.07) * mm, "end": v(30.18, -135.94) * mm});
            skLineSegment(sketch, "E1582", {"start": v(30.18, -135.94) * mm, "end": v(29.51, -135.94) * mm});
            skLineSegment(sketch, "E1583", {"start": v(29.51, -135.94) * mm, "end": v(28.04, -135.9) * mm});
            skLineSegment(sketch, "E1584", {"start": v(28.04, -135.9) * mm, "end": v(26.58, -135.78) * mm});
            skLineSegment(sketch, "E1585", {"start": v(26.58, -135.78) * mm, "end": v(25.91, -135.7) * mm});
            skLineSegment(sketch, "E1586", {"start": v(25.91, -135.7) * mm, "end": v(25.55, -134.8) * mm});
            skLineSegment(sketch, "E1587", {"start": v(25.55, -134.8) * mm, "end": v(24.85, -132.78) * mm});
            skLineSegment(sketch, "E1588", {"start": v(24.85, -132.78) * mm, "end": v(24.28, -130.77) * mm});
            skLineSegment(sketch, "E1589", {"start": v(24.28, -130.77) * mm, "end": v(24.06, -129.84) * mm});
            skLineSegment(sketch, "E1590", {"start": v(24.06, -129.84) * mm, "end": v(23.46, -129.7) * mm});
            skLineSegment(sketch, "E1591", {"start": v(23.46, -129.7) * mm, "end": v(22.15, -129.35) * mm});
            skLineSegment(sketch, "E1592", {"start": v(22.15, -129.35) * mm, "end": v(20.86, -128.94) * mm});
            skLineSegment(sketch, "E1593", {"start": v(20.86, -128.94) * mm, "end": v(20.44, -128.79) * mm});
            skLineSegment(sketch, "E1594", {"start": v(20.44, -128.79) * mm, "end": v(20.16, -128.67) * mm});
            skLineSegment(sketch, "E1595", {"start": v(20.16, -128.67) * mm, "end": v(19.43, -129.3) * mm});
            skLineSegment(sketch, "E1596", {"start": v(19.43, -129.3) * mm, "end": v(18.65, -129.93) * mm});
            skLineSegment(sketch, "E1597", {"start": v(18.65, -129.93) * mm, "end": v(17.73, -130.62) * mm});
            skLineSegment(sketch, "E1598", {"start": v(17.73, -130.62) * mm, "end": v(15.06, -132.37) * mm});
            skLineSegment(sketch, "E1599", {"start": v(15.06, -132.37) * mm, "end": v(14.46, -132.07) * mm});
            skLineSegment(sketch, "E1600", {"start": v(14.46, -132.07) * mm, "end": v(13.19, -131.34) * mm});
            skLineSegment(sketch, "E1601", {"start": v(13.19, -131.34) * mm, "end": v(11.94, -130.55) * mm});
            skLineSegment(sketch, "E1602", {"start": v(11.94, -130.55) * mm, "end": v(11.54, -130.28) * mm});
            skLineSegment(sketch, "E1603", {"start": v(11.54, -130.28) * mm, "end": v(11.4, -130.18) * mm});
            skLineSegment(sketch, "E1604", {"start": v(11.4, -130.18) * mm, "end": v(11.5, -129.2) * mm});
            skLineSegment(sketch, "E1605", {"start": v(11.5, -129.2) * mm, "end": v(11.81, -127.1) * mm});
            skLineSegment(sketch, "E1606", {"start": v(11.81, -127.1) * mm, "end": v(12.24, -125.05) * mm});
            skLineSegment(sketch, "E1607", {"start": v(12.24, -125.05) * mm, "end": v(12.48, -124.13) * mm});
            skLineSegment(sketch, "E1608", {"start": v(12.48, -124.13) * mm, "end": v(12.01, -123.73) * mm});
            skLineSegment(sketch, "E1609", {"start": v(12.01, -123.73) * mm, "end": v(11.02, -122.8) * mm});
            skLineSegment(sketch, "E1610", {"start": v(11.02, -122.8) * mm, "end": v(10.07, -121.84) * mm});
            skLineSegment(sketch, "E1611", {"start": v(10.07, -121.84) * mm, "end": v(9.77, -121.5) * mm});
            skLineSegment(sketch, "E1612", {"start": v(9.77, -121.5) * mm, "end": v(9.57, -121.28) * mm});
            skLineSegment(sketch, "E1613", {"start": v(9.57, -121.28) * mm, "end": v(8.63, -121.5) * mm});
            skLineSegment(sketch, "E1614", {"start": v(8.63, -121.5) * mm, "end": v(6.51, -121.87) * mm});
            skLineSegment(sketch, "E1615", {"start": v(6.51, -121.87) * mm, "end": v(4.34, -122.12) * mm});
            skLineSegment(sketch, "E1616", {"start": v(4.34, -122.12) * mm, "end": v(3.34, -122.19) * mm});
            skLineSegment(sketch, "E1617", {"start": v(3.34, -122.19) * mm, "end": v(2.95, -121.64) * mm});
            skLineSegment(sketch, "E1618", {"start": v(2.95, -121.64) * mm, "end": v(2.16, -120.4) * mm});
            skLineSegment(sketch, "E1619", {"start": v(2.16, -120.4) * mm, "end": v(1.42, -119.13) * mm});
            skLineSegment(sketch, "E1620", {"start": v(1.42, -119.13) * mm, "end": v(1.19, -118.7) * mm});
            skLineSegment(sketch, "E1621", {"start": v(1.19, -118.7) * mm, "end": v(1.1, -118.54) * mm});
            skLineSegment(sketch, "E1622", {"start": v(1.1, -118.54) * mm, "end": v(1.65, -117.73) * mm});
            skLineSegment(sketch, "E1623", {"start": v(1.65, -117.73) * mm, "end": v(2.9, -116.01) * mm});
            skLineSegment(sketch, "E1624", {"start": v(2.9, -116.01) * mm, "end": v(4.23, -114.4) * mm});
            skLineSegment(sketch, "E1625", {"start": v(4.23, -114.4) * mm, "end": v(4.87, -113.7) * mm});
            skLineSegment(sketch, "E1626", {"start": v(4.87, -113.7) * mm, "end": v(4.64, -113.12) * mm});
            skLineSegment(sketch, "E1627", {"start": v(4.64, -113.12) * mm, "end": v(4.2, -111.84) * mm});
            skLineSegment(sketch, "E1628", {"start": v(4.2, -111.84) * mm, "end": v(3.8, -110.55) * mm});
            skLineSegment(sketch, "E1629", {"start": v(3.8, -110.55) * mm, "end": v(3.65, -109.95) * mm});
            skLineSegment(sketch, "E1630", {"start": v(3.65, -109.95) * mm, "end": v(3.62, -109.82) * mm});
            skLineSegment(sketch, "E1631", {"start": v(3.62, -109.82) * mm, "end": v(2.69, -109.57) * mm});
            skLineSegment(sketch, "E1632", {"start": v(2.69, -109.57) * mm, "end": v(1.72, -109.29) * mm});
            skLineSegment(sketch, "E1633", {"start": v(1.72, -109.29) * mm, "end": v(0.64, -108.92) * mm});
            skLineSegment(sketch, "E1634", {"start": v(0.64, -108.92) * mm, "end": v(-1.4, -108.12) * mm});
            skLineSegment(sketch, "E1635", {"start": v(-1.4, -108.12) * mm, "end": v(-2.32, -107.72) * mm});
            skLineSegment(sketch, "E1636", {"start": v(-2.32, -107.72) * mm, "end": v(-2.4, -107.05) * mm});
            skLineSegment(sketch, "E1637", {"start": v(-2.4, -107.05) * mm, "end": v(-2.53, -105.59) * mm});
            skLineSegment(sketch, "E1638", {"start": v(-2.53, -105.59) * mm, "end": v(-2.58, -104.12) * mm});
            skLineSegment(sketch, "E1639", {"start": v(-2.58, -104.12) * mm, "end": v(-2.6, -103.46) * mm});
            skLineSegment(sketch, "E1640", {"start": v(-2.6, -103.46) * mm, "end": v(0.17, -102.05) * mm});
            skLineSegment(sketch, "E1641", {"start": v(0.17, -102.05) * mm, "end": v(3, -100.9) * mm});
            skLineSegment(sketch, "E1642", {"start": v(3, -100.9) * mm, "end": v(3, -100.74) * mm});
            skLineSegment(sketch, "E1643", {"start": v(3, -100.74) * mm, "end": v(3.26, -98.96) * mm});
            skLineSegment(sketch, "E1644", {"start": v(3.26, -98.96) * mm, "end": v(3.51, -97.63) * mm});
            skLineSegment(sketch, "E1645", {"start": v(3.51, -97.63) * mm, "end": v(3.68, -96.9) * mm});
            skLineSegment(sketch, "E1646", {"start": v(3.68, -96.9) * mm, "end": v(2.97, -96.24) * mm});
            skLineSegment(sketch, "E1647", {"start": v(2.97, -96.24) * mm, "end": v(1.45, -94.72) * mm});
            skLineSegment(sketch, "E1648", {"start": v(1.45, -94.72) * mm, "end": v(0.02, -93.07) * mm});
            skLineSegment(sketch, "E1649", {"start": v(0.02, -93.07) * mm, "end": v(-0.6, -92.28) * mm});
            skLineSegment(sketch, "E1650", {"start": v(-0.6, -92.28) * mm, "end": v(-0.37, -91.66) * mm});
            skLineSegment(sketch, "E1651", {"start": v(-0.37, -91.66) * mm, "end": v(0.2, -90.3) * mm});
            skLineSegment(sketch, "E1652", {"start": v(0.2, -90.3) * mm, "end": v(0.83, -88.97) * mm});
            skLineSegment(sketch, "E1653", {"start": v(0.83, -88.97) * mm, "end": v(1.13, -88.37) * mm});
            skLineSegment(sketch, "E1654", {"start": v(1.13, -88.37) * mm, "end": v(2.1, -88.36) * mm});
            skLineSegment(sketch, "E1655", {"start": v(2.1, -88.36) * mm, "end": v(4.24, -88.42) * mm});
            skLineSegment(sketch, "E1656", {"start": v(4.24, -88.42) * mm, "end": v(6.33, -88.6) * mm});
            skLineSegment(sketch, "E1657", {"start": v(6.33, -88.6) * mm, "end": v(7.27, -88.73) * mm});
            skLineSegment(sketch, "E1658", {"start": v(7.27, -88.73) * mm, "end": v(7.36, -88.59) * mm});
            skLineSegment(sketch, "E1659", {"start": v(7.36, -88.59) * mm, "end": v(7.6, -88.22) * mm});
            skLineSegment(sketch, "E1660", {"start": v(7.6, -88.22) * mm, "end": v(8.4, -87.12) * mm});
            skLineSegment(sketch, "E1661", {"start": v(8.4, -87.12) * mm, "end": v(9.26, -86.06) * mm});
            skLineSegment(sketch, "E1662", {"start": v(9.26, -86.06) * mm, "end": v(9.75, -85.5) * mm});
            skLineSegment(sketch, "E1663", {"start": v(9.75, -85.5) * mm, "end": v(9.42, -84.59) * mm});
            skLineSegment(sketch, "E1664", {"start": v(9.42, -84.59) * mm, "end": v(8.79, -82.53) * mm});
            skLineSegment(sketch, "E1665", {"start": v(8.79, -82.53) * mm, "end": v(8.29, -80.4) * mm});
            skLineSegment(sketch, "E1666", {"start": v(8.29, -80.4) * mm, "end": v(8.1, -79.41) * mm});
            skLineSegment(sketch, "E1667", {"start": v(8.1, -79.41) * mm, "end": v(8.6, -78.97) * mm});
            skLineSegment(sketch, "E1668", {"start": v(8.6, -78.97) * mm, "end": v(9.73, -78.04) * mm});
            skLineSegment(sketch, "E1669", {"start": v(9.73, -78.04) * mm, "end": v(10.9, -77.15) * mm});
            skLineSegment(sketch, "E1670", {"start": v(10.9, -77.15) * mm, "end": v(11.45, -76.76) * mm});
            skLineSegment(sketch, "E1671", {"start": v(11.45, -76.76) * mm, "end": v(12.32, -77.2) * mm});
            skLineSegment(sketch, "E1672", {"start": v(12.32, -77.2) * mm, "end": v(14.17, -78.24) * mm});
            skLineSegment(sketch, "E1673", {"start": v(14.17, -78.24) * mm, "end": v(15.94, -79.38) * mm});
            skLineSegment(sketch, "E1674", {"start": v(15.94, -79.38) * mm, "end": v(16.72, -79.92) * mm});
            skLineSegment(sketch, "E1675", {"start": v(16.72, -79.92) * mm, "end": v(16.86, -79.83) * mm});
            skLineSegment(sketch, "E1676", {"start": v(16.86, -79.83) * mm, "end": v(17.26, -79.62) * mm});
            skLineSegment(sketch, "E1677", {"start": v(17.26, -79.62) * mm, "end": v(18.47, -79.02) * mm});
            skLineSegment(sketch, "E1678", {"start": v(18.47, -79.02) * mm, "end": v(19.71, -78.48) * mm});
            skLineSegment(sketch, "E1679", {"start": v(19.71, -78.48) * mm, "end": v(20.4, -78.2) * mm});
            skLineSegment(sketch, "E1680", {"start": v(20.4, -78.2) * mm, "end": v(20.54, -77.25) * mm});
            skLineSegment(sketch, "E1681", {"start": v(20.54, -77.25) * mm, "end": v(20.94, -75.13) * mm});
            skLineSegment(sketch, "E1682", {"start": v(20.94, -75.13) * mm, "end": v(21.78, -72.05) * mm});
            skLineSegment(sketch, "E1683", {"start": v(21.78, -72.05) * mm, "end": v(22.43, -71.9) * mm});
            skLineSegment(sketch, "E1684", {"start": v(22.43, -71.9) * mm, "end": v(23.87, -71.6) * mm});
            skLineSegment(sketch, "E1685", {"start": v(23.87, -71.6) * mm, "end": v(25.32, -71.35) * mm});
            skLineSegment(sketch, "E1686", {"start": v(25.32, -71.35) * mm, "end": v(25.98, -71.27) * mm});
            skLineSegment(sketch, "E1687", {"start": v(25.98, -71.27) * mm, "end": v(26.54, -72.06) * mm});
            skLineSegment(sketch, "E1688", {"start": v(26.54, -72.06) * mm, "end": v(27.7, -73.85) * mm});
            skLineSegment(sketch, "E1689", {"start": v(27.7, -73.85) * mm, "end": v(28.74, -75.68) * mm});
            skLineSegment(sketch, "E1690", {"start": v(28.74, -75.68) * mm, "end": v(29.17, -76.52) * mm});
            skLineSegment(sketch, "E1691", {"start": v(29.17, -76.52) * mm, "end": v(29.8, -76.5) * mm});
            skLineSegment(sketch, "E1692", {"start": v(29.8, -76.5) * mm, "end": v(31.15, -76.53) * mm});
            skLineSegment(sketch, "E1693", {"start": v(31.15, -76.53) * mm, "end": v(32.5, -76.63) * mm});
            skLineSegment(sketch, "E1694", {"start": v(32.5, -76.63) * mm, "end": v(33.24, -76.72) * mm});
            skLineSegment(sketch, "E1695", {"start": v(33.24, -76.72) * mm, "end": v(33.8, -75.93) * mm});
            skLineSegment(sketch, "E1696", {"start": v(33.8, -75.93) * mm, "end": v(35.14, -74.24) * mm});
            skLineSegment(sketch, "E1697", {"start": v(35.14, -74.24) * mm, "end": v(36.6, -72.62) * mm});
            skLineSegment(sketch, "E1698", {"start": v(36.6, -72.62) * mm, "end": v(37.3, -71.9) * mm});
            skLineSegment(sketch, "E1699", {"start": v(37.3, -71.9) * mm, "end": v(37.96, -72.05) * mm});
            skLineSegment(sketch, "E1700", {"start": v(37.96, -72.05) * mm, "end": v(39.37, -72.45) * mm});
            skLineSegment(sketch, "E1701", {"start": v(39.37, -72.45) * mm, "end": v(40.77, -72.92) * mm});
            skLineSegment(sketch, "E1702", {"start": v(40.77, -72.92) * mm, "end": v(41.23, -73.09) * mm});
            skLineSegment(sketch, "E1703", {"start": v(41.23, -73.09) * mm, "end": v(41.4, -73.15) * mm});
            skLineSegment(sketch, "E1704", {"start": v(41.4, -73.15) * mm, "end": v(41.53, -74.12) * mm});
            skLineSegment(sketch, "E1705", {"start": v(41.53, -74.12) * mm, "end": v(41.72, -76.24) * mm});
            skLineSegment(sketch, "E1706", {"start": v(41.72, -76.24) * mm, "end": v(41.8, -78.33) * mm});
            skLineSegment(sketch, "E1707", {"start": v(41.8, -78.33) * mm, "end": v(41.79, -79.28) * mm});
            skLineSegment(sketch, "E1708", {"start": v(41.79, -79.28) * mm, "end": v(42.34, -79.56) * mm});
            skLineSegment(sketch, "E1709", {"start": v(42.34, -79.56) * mm, "end": v(43.52, -80.22) * mm});
            skLineSegment(sketch, "E1710", {"start": v(43.52, -80.22) * mm, "end": v(44.67, -80.93) * mm});
            skLineSegment(sketch, "E1711", {"start": v(44.67, -80.93) * mm, "end": v(45.18, -81.28) * mm});
            skLineSegment(sketch, "E1712", {"start": v(45.18, -81.28) * mm, "end": v(45.3, -81.36) * mm});
            skLineSegment(sketch, "E1713", {"start": v(45.3, -81.36) * mm, "end": v(46.16, -80.92) * mm});
            skLineSegment(sketch, "E1714", {"start": v(46.16, -80.92) * mm, "end": v(47.07, -80.5) * mm});
            skLineSegment(sketch, "E1715", {"start": v(47.07, -80.5) * mm, "end": v(48.12, -80.05) * mm});
            skLineSegment(sketch, "E1716", {"start": v(48.12, -80.05) * mm, "end": v(51.13, -78.99) * mm});
            skLineSegment(sketch, "E1717", {"start": v(51.13, -78.99) * mm, "end": v(51.64, -79.43) * mm});
            skLineSegment(sketch, "E1718", {"start": v(51.64, -79.43) * mm, "end": v(52.7, -80.44) * mm});
            skLineSegment(sketch, "E1719", {"start": v(52.7, -80.44) * mm, "end": v(53.72, -81.5) * mm});
            skLineSegment(sketch, "E1720", {"start": v(53.72, -81.5) * mm, "end": v(54.05, -81.86) * mm});
            skLineSegment(sketch, "E1721", {"start": v(54.05, -81.86) * mm, "end": v(54.17, -82) * mm});
            skLineSegment(sketch, "E1722", {"start": v(54.17, -82) * mm, "end": v(53.83, -82.91) * mm});
            skLineSegment(sketch, "E1723", {"start": v(53.83, -82.91) * mm, "end": v(53.02, -84.88) * mm});
            skLineSegment(sketch, "E1724", {"start": v(53.02, -84.88) * mm, "end": v(52.12, -86.77) * mm});
            skLineSegment(sketch, "E1725", {"start": v(52.12, -86.77) * mm, "end": v(51.67, -87.6) * mm});
            skLineSegment(sketch, "E1726", {"start": v(51.67, -87.6) * mm, "end": v(52.03, -88.1) * mm});
            skLineSegment(sketch, "E1727", {"start": v(52.03, -88.1) * mm, "end": v(52.77, -89.24) * mm});
            skLineSegment(sketch, "E1728", {"start": v(52.77, -89.24) * mm, "end": v(53.46, -90.4) * mm});
            skLineSegment(sketch, "E1729", {"start": v(53.46, -90.4) * mm, "end": v(53.68, -90.8) * mm});
            skLineSegment(sketch, "E1730", {"start": v(53.68, -90.8) * mm, "end": v(53.81, -91.07) * mm});
            skLineSegment(sketch, "E1731", {"start": v(53.81, -91.07) * mm, "end": v(54.78, -91.08) * mm});
            skLineSegment(sketch, "E1732", {"start": v(54.78, -91.08) * mm, "end": v(56.93, -91.22) * mm});
            skLineSegment(sketch, "E1733", {"start": v(56.93, -91.22) * mm, "end": v(59.1, -91.5) * mm});
            skLineSegment(sketch, "E1734", {"start": v(59.1, -91.5) * mm, "end": v(60.09, -91.68) * mm});
            skLineSegment(sketch, "E1735", {"start": v(60.09, -91.68) * mm, "end": v(60.33, -92.3) * mm});
            skLineSegment(sketch, "E1736", {"start": v(60.33, -92.3) * mm, "end": v(60.8, -93.7) * mm});
            skLineSegment(sketch, "E1737", {"start": v(60.8, -93.7) * mm, "end": v(61.21, -95.1) * mm});
            skLineSegment(sketch, "E1738", {"start": v(61.21, -95.1) * mm, "end": v(61.34, -95.58) * mm});
            skLineSegment(sketch, "E1739", {"start": v(61.34, -95.58) * mm, "end": v(61.38, -95.76) * mm});
            skLineSegment(sketch, "E1740", {"start": v(61.38, -95.76) * mm, "end": v(60.65, -96.41) * mm});
            skLineSegment(sketch, "E1741", {"start": v(60.65, -96.41) * mm, "end": v(59.02, -97.78) * mm});
            skLineSegment(sketch, "E1742", {"start": v(59.02, -97.78) * mm, "end": v(57.34, -99.03) * mm});
            skLineSegment(sketch, "E1743", {"start": v(57.34, -99.03) * mm, "end": v(56.55, -99.56) * mm});
            skLineSegment(sketch, "E1744", {"start": v(56.55, -99.56) * mm, "end": v(56.7, -100.8) * mm});
            skLineSegment(sketch, "E1745", {"start": v(56.7, -100.8) * mm, "end": v(56.76, -101.52) * mm});
            skLineSegment(sketch, "E1746", {"start": v(56.76, -101.52) * mm, "end": v(56.83, -102.87) * mm});
            skLineSegment(sketch, "E1747", {"start": v(56.83, -102.87) * mm, "end": v(56.84, -103.49) * mm});
            skLineSegment(sketch, "E1748", {"start": v(56.84, -103.49) * mm, "end": v(56.84, -103.62) * mm});
            skLineSegment(sketch, "E1749", {"start": v(29.76, -102.57) * mm, "end": v(29.03, -102.88) * mm});
            skLineSegment(sketch, "E1750", {"start": v(29.03, -102.88) * mm, "end": v(28.73, -103.6) * mm});
            skLineSegment(sketch, "E1751", {"start": v(28.73, -103.6) * mm, "end": v(29.03, -104.33) * mm});
            skLineSegment(sketch, "E1752", {"start": v(29.03, -104.33) * mm, "end": v(29.76, -104.63) * mm});
            skLineSegment(sketch, "E1753", {"start": v(29.76, -104.63) * mm, "end": v(30.48, -104.33) * mm});
            skLineSegment(sketch, "E1754", {"start": v(30.48, -104.33) * mm, "end": v(30.78, -103.6) * mm});
            skLineSegment(sketch, "E1755", {"start": v(30.78, -103.6) * mm, "end": v(30.48, -102.88) * mm});
            skLineSegment(sketch, "E1756", {"start": v(30.48, -102.88) * mm, "end": v(29.76, -102.57) * mm});
            skLineSegment(sketch, "E1757", {"start": v(43.65, -41.27) * mm, "end": v(42.7, -41.1) * mm});
            skLineSegment(sketch, "E1758", {"start": v(42.7, -41.1) * mm, "end": v(40.58, -40.59) * mm});
            skLineSegment(sketch, "E1759", {"start": v(40.58, -40.59) * mm, "end": v(38.47, -39.86) * mm});
            skLineSegment(sketch, "E1760", {"start": v(38.47, -39.86) * mm, "end": v(37.77, -39.58) * mm});
            skLineSegment(sketch, "E1761", {"start": v(37.77, -39.58) * mm, "end": v(37.52, -39.46) * mm});
            skLineSegment(sketch, "E1762", {"start": v(37.52, -39.46) * mm, "end": v(37.39, -38.74) * mm});
            skLineSegment(sketch, "E1763", {"start": v(37.39, -38.74) * mm, "end": v(37.19, -37.15) * mm});
            skLineSegment(sketch, "E1764", {"start": v(37.19, -37.15) * mm, "end": v(37.1, -35.54) * mm});
            skLineSegment(sketch, "E1765", {"start": v(37.1, -35.54) * mm, "end": v(37.08, -34.81) * mm});
            skLineSegment(sketch, "E1766", {"start": v(37.08, -34.81) * mm, "end": v(37.94, -34.3) * mm});
            skLineSegment(sketch, "E1767", {"start": v(37.94, -34.3) * mm, "end": v(39.87, -33.32) * mm});
            skLineSegment(sketch, "E1768", {"start": v(39.87, -33.32) * mm, "end": v(41.83, -32.52) * mm});
            skLineSegment(sketch, "E1769", {"start": v(41.83, -32.52) * mm, "end": v(42.73, -32.21) * mm});
            skLineSegment(sketch, "E1770", {"start": v(42.73, -32.21) * mm, "end": v(42.83, -31.59) * mm});
            skLineSegment(sketch, "E1771", {"start": v(42.83, -31.59) * mm, "end": v(42.94, -30.95) * mm});
            skLineSegment(sketch, "E1772", {"start": v(42.94, -30.95) * mm, "end": v(43.1, -30.23) * mm});
            skLineSegment(sketch, "E1773", {"start": v(43.1, -30.23) * mm, "end": v(43.3, -29.52) * mm});
            skLineSegment(sketch, "E1774", {"start": v(43.3, -29.52) * mm, "end": v(43.5, -28.9) * mm});
            skLineSegment(sketch, "E1775", {"start": v(43.5, -28.9) * mm, "end": v(43.7, -28.3) * mm});
            skLineSegment(sketch, "E1776", {"start": v(43.7, -28.3) * mm, "end": v(43.74, -28.17) * mm});
            skLineSegment(sketch, "E1777", {"start": v(43.74, -28.17) * mm, "end": v(43.12, -27.43) * mm});
            skLineSegment(sketch, "E1778", {"start": v(43.12, -27.43) * mm, "end": v(41.83, -25.68) * mm});
            skLineSegment(sketch, "E1779", {"start": v(41.83, -25.68) * mm, "end": v(40.68, -23.77) * mm});
            skLineSegment(sketch, "E1780", {"start": v(40.68, -23.77) * mm, "end": v(40.2, -22.85) * mm});
            skLineSegment(sketch, "E1781", {"start": v(40.2, -22.85) * mm, "end": v(40.57, -22.22) * mm});
            skLineSegment(sketch, "E1782", {"start": v(40.57, -22.22) * mm, "end": v(41.44, -20.86) * mm});
            skLineSegment(sketch, "E1783", {"start": v(41.44, -20.86) * mm, "end": v(41.94, -20.16) * mm});
            skLineSegment(sketch, "E1784", {"start": v(41.94, -20.16) * mm, "end": v(42.4, -19.57) * mm});
            skLineSegment(sketch, "E1785", {"start": v(42.4, -19.57) * mm, "end": v(42.86, -19) * mm});
            skLineSegment(sketch, "E1786", {"start": v(42.86, -19) * mm, "end": v(43.85, -19.17) * mm});
            skLineSegment(sketch, "E1787", {"start": v(43.85, -19.17) * mm, "end": v(45.95, -19.66) * mm});
            skLineSegment(sketch, "E1788", {"start": v(45.95, -19.66) * mm, "end": v(47.97, -20.3) * mm});
            skLineSegment(sketch, "E1789", {"start": v(47.97, -20.3) * mm, "end": v(48.86, -20.65) * mm});
            skLineSegment(sketch, "E1790", {"start": v(48.86, -20.65) * mm, "end": v(49.33, -20.23) * mm});
            skLineSegment(sketch, "E1791", {"start": v(49.33, -20.23) * mm, "end": v(49.84, -19.82) * mm});
            skLineSegment(sketch, "E1792", {"start": v(49.84, -19.82) * mm, "end": v(50.43, -19.37) * mm});
            skLineSegment(sketch, "E1793", {"start": v(50.43, -19.37) * mm, "end": v(52.12, -18.27) * mm});
            skLineSegment(sketch, "E1794", {"start": v(52.12, -18.27) * mm, "end": v(52.24, -18.2) * mm});
            skLineSegment(sketch, "E1795", {"start": v(52.24, -18.2) * mm, "end": v(52.23, -17.23) * mm});
            skLineSegment(sketch, "E1796", {"start": v(52.23, -17.23) * mm, "end": v(52.37, -15.06) * mm});
            skLineSegment(sketch, "E1797", {"start": v(52.37, -15.06) * mm, "end": v(52.94, -11.85) * mm});
            skLineSegment(sketch, "E1798", {"start": v(52.94, -11.85) * mm, "end": v(53.62, -11.6) * mm});
            skLineSegment(sketch, "E1799", {"start": v(53.62, -11.6) * mm, "end": v(54.34, -11.36) * mm});
            skLineSegment(sketch, "E1800", {"start": v(54.34, -11.36) * mm, "end": v(55.16, -11.12) * mm});
            skLineSegment(sketch, "E1801", {"start": v(55.16, -11.12) * mm, "end": v(56.73, -10.74) * mm});
            skLineSegment(sketch, "E1802", {"start": v(56.73, -10.74) * mm, "end": v(57.45, -10.61) * mm});
            skLineSegment(sketch, "E1803", {"start": v(57.45, -10.61) * mm, "end": v(58.1, -11.37) * mm});
            skLineSegment(sketch, "E1804", {"start": v(58.1, -11.37) * mm, "end": v(59.4, -13.1) * mm});
            skLineSegment(sketch, "E1805", {"start": v(59.4, -13.1) * mm, "end": v(60.53, -14.9) * mm});
            skLineSegment(sketch, "E1806", {"start": v(60.53, -14.9) * mm, "end": v(60.86, -15.5) * mm});
            skLineSegment(sketch, "E1807", {"start": v(60.86, -15.5) * mm, "end": v(60.98, -15.73) * mm});
            skLineSegment(sketch, "E1808", {"start": v(60.98, -15.73) * mm, "end": v(61.62, -15.71) * mm});
            skLineSegment(sketch, "E1809", {"start": v(61.62, -15.71) * mm, "end": v(62.26, -15.73) * mm});
            skLineSegment(sketch, "E1810", {"start": v(62.26, -15.73) * mm, "end": v(63, -15.76) * mm});
            skLineSegment(sketch, "E1811", {"start": v(63, -15.76) * mm, "end": v(65, -16) * mm});
            skLineSegment(sketch, "E1812", {"start": v(65, -16) * mm, "end": v(65.14, -16.03) * mm});
            skLineSegment(sketch, "E1813", {"start": v(65.14, -16.03) * mm, "end": v(65.77, -15.27) * mm});
            skLineSegment(sketch, "E1814", {"start": v(65.77, -15.27) * mm, "end": v(67.27, -13.7) * mm});
            skLineSegment(sketch, "E1815", {"start": v(67.27, -13.7) * mm, "end": v(68.95, -12.23) * mm});
            skLineSegment(sketch, "E1816", {"start": v(68.95, -12.23) * mm, "end": v(69.77, -11.6) * mm});
            skLineSegment(sketch, "E1817", {"start": v(69.77, -11.6) * mm, "end": v(71.94, -12.48) * mm});
            skLineSegment(sketch, "E1818", {"start": v(71.94, -12.48) * mm, "end": v(73.38, -13.2) * mm});
            skLineSegment(sketch, "E1819", {"start": v(73.38, -13.2) * mm, "end": v(74.02, -13.56) * mm});
            skLineSegment(sketch, "E1820", {"start": v(74.02, -13.56) * mm, "end": v(74.03, -14.55) * mm});
            skLineSegment(sketch, "E1821", {"start": v(74.03, -14.55) * mm, "end": v(73.91, -16.71) * mm});
            skLineSegment(sketch, "E1822", {"start": v(73.91, -16.71) * mm, "end": v(73.63, -18.81) * mm});
            skLineSegment(sketch, "E1823", {"start": v(73.63, -18.81) * mm, "end": v(73.44, -19.75) * mm});
            skLineSegment(sketch, "E1824", {"start": v(73.44, -19.75) * mm, "end": v(73.93, -20.14) * mm});
            skLineSegment(sketch, "E1825", {"start": v(73.93, -20.14) * mm, "end": v(74.96, -21.07) * mm});
            skLineSegment(sketch, "E1826", {"start": v(74.96, -21.07) * mm, "end": v(75.49, -21.6) * mm});
            skLineSegment(sketch, "E1827", {"start": v(75.49, -21.6) * mm, "end": v(75.93, -22.07) * mm});
            skLineSegment(sketch, "E1828", {"start": v(75.93, -22.07) * mm, "end": v(76.43, -22.65) * mm});
            skLineSegment(sketch, "E1829", {"start": v(76.43, -22.65) * mm, "end": v(77.39, -22.48) * mm});
            skLineSegment(sketch, "E1830", {"start": v(77.39, -22.48) * mm, "end": v(78.4, -22.34) * mm});
            skLineSegment(sketch, "E1831", {"start": v(78.4, -22.34) * mm, "end": v(79.55, -22.24) * mm});
            skLineSegment(sketch, "E1832", {"start": v(79.55, -22.24) * mm, "end": v(81.78, -22.2) * mm});
            skLineSegment(sketch, "E1833", {"start": v(81.78, -22.2) * mm, "end": v(82.53, -22.22) * mm});
            skLineSegment(sketch, "E1834", {"start": v(82.53, -22.22) * mm, "end": v(82.81, -22.24) * mm});
            skLineSegment(sketch, "E1835", {"start": v(82.81, -22.24) * mm, "end": v(83.92, -24.3) * mm});
            skLineSegment(sketch, "E1836", {"start": v(83.92, -24.3) * mm, "end": v(84.56, -25.78) * mm});
            skLineSegment(sketch, "E1837", {"start": v(84.56, -25.78) * mm, "end": v(84.82, -26.46) * mm});
            skLineSegment(sketch, "E1838", {"start": v(84.82, -26.46) * mm, "end": v(84.18, -27.24) * mm});
            skLineSegment(sketch, "E1839", {"start": v(84.18, -27.24) * mm, "end": v(82.7, -28.82) * mm});
            skLineSegment(sketch, "E1840", {"start": v(82.7, -28.82) * mm, "end": v(81.14, -30.24) * mm});
            skLineSegment(sketch, "E1841", {"start": v(81.14, -30.24) * mm, "end": v(80.4, -30.84) * mm});
            skLineSegment(sketch, "E1842", {"start": v(80.4, -30.84) * mm, "end": v(80.44, -31) * mm});
            skLineSegment(sketch, "E1843", {"start": v(80.44, -31) * mm, "end": v(80.52, -31.46) * mm});
            skLineSegment(sketch, "E1844", {"start": v(80.52, -31.46) * mm, "end": v(80.71, -32.83) * mm});
            skLineSegment(sketch, "E1845", {"start": v(80.71, -32.83) * mm, "end": v(80.8, -34.22) * mm});
            skLineSegment(sketch, "E1846", {"start": v(80.8, -34.22) * mm, "end": v(80.82, -34.85) * mm});
            skLineSegment(sketch, "E1847", {"start": v(80.82, -34.85) * mm, "end": v(80.82, -34.98) * mm});
            skLineSegment(sketch, "E1848", {"start": v(80.82, -34.98) * mm, "end": v(81.66, -35.47) * mm});
            skLineSegment(sketch, "E1849", {"start": v(81.66, -35.47) * mm, "end": v(83.47, -36.68) * mm});
            skLineSegment(sketch, "E1850", {"start": v(83.47, -36.68) * mm, "end": v(85.21, -38.07) * mm});
            skLineSegment(sketch, "E1851", {"start": v(85.21, -38.07) * mm, "end": v(85.97, -38.77) * mm});
            skLineSegment(sketch, "E1852", {"start": v(85.97, -38.77) * mm, "end": v(85.5, -41.06) * mm});
            skLineSegment(sketch, "E1853", {"start": v(85.5, -41.06) * mm, "end": v(85.03, -42.6) * mm});
            skLineSegment(sketch, "E1854", {"start": v(85.03, -42.6) * mm, "end": v(84.8, -43.3) * mm});
            skLineSegment(sketch, "E1855", {"start": v(84.8, -43.3) * mm, "end": v(83.81, -43.48) * mm});
            skLineSegment(sketch, "E1856", {"start": v(83.81, -43.48) * mm, "end": v(81.66, -43.74) * mm});
            skLineSegment(sketch, "E1857", {"start": v(81.66, -43.74) * mm, "end": v(79.55, -43.82) * mm});
            skLineSegment(sketch, "E1858", {"start": v(79.55, -43.82) * mm, "end": v(78.6, -43.8) * mm});
            skLineSegment(sketch, "E1859", {"start": v(78.6, -43.8) * mm, "end": v(78.52, -43.96) * mm});
            skLineSegment(sketch, "E1860", {"start": v(78.52, -43.96) * mm, "end": v(78.3, -44.35) * mm});
            skLineSegment(sketch, "E1861", {"start": v(78.3, -44.35) * mm, "end": v(77.56, -45.54) * mm});
            skLineSegment(sketch, "E1862", {"start": v(77.56, -45.54) * mm, "end": v(76.74, -46.65) * mm});
            skLineSegment(sketch, "E1863", {"start": v(76.74, -46.65) * mm, "end": v(76.46, -47.02) * mm});
            skLineSegment(sketch, "E1864", {"start": v(76.46, -47.02) * mm, "end": v(76.25, -47.25) * mm});
            skLineSegment(sketch, "E1865", {"start": v(76.25, -47.25) * mm, "end": v(76.6, -48.16) * mm});
            skLineSegment(sketch, "E1866", {"start": v(76.6, -48.16) * mm, "end": v(77.2, -50.26) * mm});
            skLineSegment(sketch, "E1867", {"start": v(77.2, -50.26) * mm, "end": v(77.64, -52.45) * mm});
            skLineSegment(sketch, "E1868", {"start": v(77.64, -52.45) * mm, "end": v(77.77, -53.46) * mm});
            skLineSegment(sketch, "E1869", {"start": v(77.77, -53.46) * mm, "end": v(77.2, -53.94) * mm});
            skLineSegment(sketch, "E1870", {"start": v(77.2, -53.94) * mm, "end": v(75.92, -54.9) * mm});
            skLineSegment(sketch, "E1871", {"start": v(75.92, -54.9) * mm, "end": v(74.59, -55.8) * mm});
            skLineSegment(sketch, "E1872", {"start": v(74.59, -55.8) * mm, "end": v(73.96, -56.17) * mm});
            skLineSegment(sketch, "E1873", {"start": v(73.96, -56.17) * mm, "end": v(73.09, -55.68) * mm});
            skLineSegment(sketch, "E1874", {"start": v(73.09, -55.68) * mm, "end": v(71.27, -54.5) * mm});
            skLineSegment(sketch, "E1875", {"start": v(71.27, -54.5) * mm, "end": v(69.6, -53.21) * mm});
            skLineSegment(sketch, "E1876", {"start": v(69.6, -53.21) * mm, "end": v(69.07, -52.76) * mm});
            skLineSegment(sketch, "E1877", {"start": v(69.07, -52.76) * mm, "end": v(68.88, -52.58) * mm});
            skLineSegment(sketch, "E1878", {"start": v(68.88, -52.58) * mm, "end": v(68.3, -52.81) * mm});
            skLineSegment(sketch, "E1879", {"start": v(68.3, -52.81) * mm, "end": v(66.97, -53.24) * mm});
            skLineSegment(sketch, "E1880", {"start": v(66.97, -53.24) * mm, "end": v(65.63, -53.58) * mm});
            skLineSegment(sketch, "E1881", {"start": v(65.63, -53.58) * mm, "end": v(64.88, -53.72) * mm});
            skLineSegment(sketch, "E1882", {"start": v(64.88, -53.72) * mm, "end": v(64.79, -53.97) * mm});
            skLineSegment(sketch, "E1883", {"start": v(64.79, -53.97) * mm, "end": v(64.54, -54.63) * mm});
            skLineSegment(sketch, "E1884", {"start": v(64.54, -54.63) * mm, "end": v(63.67, -56.63) * mm});
            skLineSegment(sketch, "E1885", {"start": v(63.67, -56.63) * mm, "end": v(62.04, -59.45) * mm});
            skLineSegment(sketch, "E1886", {"start": v(62.04, -59.45) * mm, "end": v(61.3, -59.45) * mm});
            skLineSegment(sketch, "E1887", {"start": v(61.3, -59.45) * mm, "end": v(59.7, -59.37) * mm});
            skLineSegment(sketch, "E1888", {"start": v(59.7, -59.37) * mm, "end": v(58.1, -59.2) * mm});
            skLineSegment(sketch, "E1889", {"start": v(58.1, -59.2) * mm, "end": v(57.38, -59.07) * mm});
            skLineSegment(sketch, "E1890", {"start": v(57.38, -59.07) * mm, "end": v(57.03, -58.14) * mm});
            skLineSegment(sketch, "E1891", {"start": v(57.03, -58.14) * mm, "end": v(56.4, -56.07) * mm});
            skLineSegment(sketch, "E1892", {"start": v(56.4, -56.07) * mm, "end": v(55.94, -54) * mm});
            skLineSegment(sketch, "E1893", {"start": v(55.94, -54) * mm, "end": v(55.8, -53.06) * mm});
            skLineSegment(sketch, "E1894", {"start": v(55.8, -53.06) * mm, "end": v(55.2, -52.86) * mm});
            skLineSegment(sketch, "E1895", {"start": v(55.2, -52.86) * mm, "end": v(54.6, -52.63) * mm});
            skLineSegment(sketch, "E1896", {"start": v(54.6, -52.63) * mm, "end": v(53.91, -52.34) * mm});
            skLineSegment(sketch, "E1897", {"start": v(53.91, -52.34) * mm, "end": v(52.12, -51.42) * mm});
            skLineSegment(sketch, "E1898", {"start": v(52.12, -51.42) * mm, "end": v(52, -51.35) * mm});
            skLineSegment(sketch, "E1899", {"start": v(52, -51.35) * mm, "end": v(51.77, -51.5) * mm});
            skLineSegment(sketch, "E1900", {"start": v(51.77, -51.5) * mm, "end": v(51.16, -51.84) * mm});
            skLineSegment(sketch, "E1901", {"start": v(51.16, -51.84) * mm, "end": v(49.2, -52.8) * mm});
            skLineSegment(sketch, "E1902", {"start": v(49.2, -52.8) * mm, "end": v(47.13, -53.6) * mm});
            skLineSegment(sketch, "E1903", {"start": v(47.13, -53.6) * mm, "end": v(46.14, -53.92) * mm});
            skLineSegment(sketch, "E1904", {"start": v(46.14, -53.92) * mm, "end": v(45.98, -53.8) * mm});
            skLineSegment(sketch, "E1905", {"start": v(45.98, -53.8) * mm, "end": v(45.58, -53.45) * mm});
            skLineSegment(sketch, "E1906", {"start": v(45.58, -53.45) * mm, "end": v(44.4, -52.36) * mm});
            skLineSegment(sketch, "E1907", {"start": v(44.4, -52.36) * mm, "end": v(42.81, -50.64) * mm});
            skLineSegment(sketch, "E1908", {"start": v(42.81, -50.64) * mm, "end": v(43.15, -49.7) * mm});
            skLineSegment(sketch, "E1909", {"start": v(43.15, -49.7) * mm, "end": v(44, -47.7) * mm});
            skLineSegment(sketch, "E1910", {"start": v(44, -47.7) * mm, "end": v(45.47, -45.01) * mm});
            skLineSegment(sketch, "E1911", {"start": v(45.47, -45.01) * mm, "end": v(45.14, -44.47) * mm});
            skLineSegment(sketch, "E1912", {"start": v(45.14, -44.47) * mm, "end": v(44.82, -43.9) * mm});
            skLineSegment(sketch, "E1913", {"start": v(44.82, -43.9) * mm, "end": v(44.49, -43.25) * mm});
            skLineSegment(sketch, "E1914", {"start": v(44.49, -43.25) * mm, "end": v(43.7, -41.4) * mm});
            skLineSegment(sketch, "E1915", {"start": v(43.7, -41.4) * mm, "end": v(43.65, -41.27) * mm});
            skLineSegment(sketch, "E1916", {"start": v(61.53, -33.98) * mm, "end": v(60.79, -34.29) * mm});
            skLineSegment(sketch, "E1917", {"start": v(60.79, -34.29) * mm, "end": v(60.48, -35.03) * mm});
            skLineSegment(sketch, "E1918", {"start": v(60.48, -35.03) * mm, "end": v(60.79, -35.77) * mm});
            skLineSegment(sketch, "E1919", {"start": v(60.79, -35.77) * mm, "end": v(61.53, -36.08) * mm});
            skLineSegment(sketch, "E1920", {"start": v(61.53, -36.08) * mm, "end": v(62.27, -35.77) * mm});
            skLineSegment(sketch, "E1921", {"start": v(62.27, -35.77) * mm, "end": v(62.57, -35.03) * mm});
            skLineSegment(sketch, "E1922", {"start": v(62.57, -35.03) * mm, "end": v(62.27, -34.29) * mm});
            skLineSegment(sketch, "E1923", {"start": v(62.27, -34.29) * mm, "end": v(61.53, -33.98) * mm});
            skLineSegment(sketch, "E1924", {"start": v(52.53, 45.31) * mm, "end": v(53.36, 44.84) * mm});
            skLineSegment(sketch, "E1925", {"start": v(53.36, 44.84) * mm, "end": v(54.2, 44.28) * mm});
            skLineSegment(sketch, "E1926", {"start": v(54.2, 44.28) * mm, "end": v(55.11, 43.56) * mm});
            skLineSegment(sketch, "E1927", {"start": v(55.11, 43.56) * mm, "end": v(56, 42.73) * mm});
            skLineSegment(sketch, "E1928", {"start": v(56, 42.73) * mm, "end": v(56.7, 41.94) * mm});
            skLineSegment(sketch, "E1929", {"start": v(56.7, 41.94) * mm, "end": v(57.37, 41.1) * mm});
            skLineSegment(sketch, "E1930", {"start": v(57.37, 41.1) * mm, "end": v(57.31, 40.88) * mm});
            skLineSegment(sketch, "E1931", {"start": v(57.31, 40.88) * mm, "end": v(56.82, 39.54) * mm});
            skLineSegment(sketch, "E1932", {"start": v(56.82, 39.54) * mm, "end": v(56.4, 38.67) * mm});
            skLineSegment(sketch, "E1933", {"start": v(56.4, 38.67) * mm, "end": v(55.52, 37.1) * mm});
            skLineSegment(sketch, "E1934", {"start": v(55.52, 37.1) * mm, "end": v(55.19, 36.62) * mm});
            skLineSegment(sketch, "E1935", {"start": v(55.19, 36.62) * mm, "end": v(55.05, 36.44) * mm});
            skLineSegment(sketch, "E1936", {"start": v(55.05, 36.44) * mm, "end": v(54.03, 36.5) * mm});
            skLineSegment(sketch, "E1937", {"start": v(54.03, 36.5) * mm, "end": v(51.87, 36.87) * mm});
            skLineSegment(sketch, "E1938", {"start": v(51.87, 36.87) * mm, "end": v(49.85, 37.53) * mm});
            skLineSegment(sketch, "E1939", {"start": v(49.85, 37.53) * mm, "end": v(49, 37.91) * mm});
            skLineSegment(sketch, "E1940", {"start": v(49, 37.91) * mm, "end": v(48.88, 37.81) * mm});
            skLineSegment(sketch, "E1941", {"start": v(48.88, 37.81) * mm, "end": v(48.54, 37.56) * mm});
            skLineSegment(sketch, "E1942", {"start": v(48.54, 37.56) * mm, "end": v(47.47, 36.86) * mm});
            skLineSegment(sketch, "E1943", {"start": v(47.47, 36.86) * mm, "end": v(46.58, 36.43) * mm});
            skLineSegment(sketch, "E1944", {"start": v(46.58, 36.43) * mm, "end": v(45.65, 36.08) * mm});
            skLineSegment(sketch, "E1945", {"start": v(45.65, 36.08) * mm, "end": v(45.46, 35.16) * mm});
            skLineSegment(sketch, "E1946", {"start": v(45.46, 35.16) * mm, "end": v(44.78, 33.1) * mm});
            skLineSegment(sketch, "E1947", {"start": v(44.78, 33.1) * mm, "end": v(44.27, 32) * mm});
            skLineSegment(sketch, "E1948", {"start": v(44.27, 32) * mm, "end": v(43.73, 31.08) * mm});
            skLineSegment(sketch, "E1949", {"start": v(43.73, 31.08) * mm, "end": v(43.14, 30.2) * mm});
            skLineSegment(sketch, "E1950", {"start": v(43.14, 30.2) * mm, "end": v(42.91, 30.19) * mm});
            skLineSegment(sketch, "E1951", {"start": v(42.91, 30.19) * mm, "end": v(42.32, 30.2) * mm});
            skLineSegment(sketch, "E1952", {"start": v(42.32, 30.2) * mm, "end": v(40.54, 30.35) * mm});
            skLineSegment(sketch, "E1953", {"start": v(40.54, 30.35) * mm, "end": v(39.6, 30.5) * mm});
            skLineSegment(sketch, "E1954", {"start": v(39.6, 30.5) * mm, "end": v(38.2, 30.87) * mm});
            skLineSegment(sketch, "E1955", {"start": v(38.2, 30.87) * mm, "end": v(38, 30.94) * mm});
            skLineSegment(sketch, "E1956", {"start": v(38, 30.94) * mm, "end": v(37.74, 31.94) * mm});
            skLineSegment(sketch, "E1957", {"start": v(37.74, 31.94) * mm, "end": v(37.54, 32.95) * mm});
            skLineSegment(sketch, "E1958", {"start": v(37.54, 32.95) * mm, "end": v(37.42, 34.11) * mm});
            skLineSegment(sketch, "E1959", {"start": v(37.42, 34.11) * mm, "end": v(37.42, 36.23) * mm});
            skLineSegment(sketch, "E1960", {"start": v(37.42, 36.23) * mm, "end": v(37.53, 37.16) * mm});
            skLineSegment(sketch, "E1961", {"start": v(37.53, 37.16) * mm, "end": v(37.4, 37.25) * mm});
            skLineSegment(sketch, "E1962", {"start": v(37.4, 37.25) * mm, "end": v(37.05, 37.49) * mm});
            skLineSegment(sketch, "E1963", {"start": v(37.05, 37.49) * mm, "end": v(36.57, 37.84) * mm});
            skLineSegment(sketch, "E1964", {"start": v(36.57, 37.84) * mm, "end": v(35.8, 38.53) * mm});
            skLineSegment(sketch, "E1965", {"start": v(35.8, 38.53) * mm, "end": v(35.18, 39.22) * mm});
            skLineSegment(sketch, "E1966", {"start": v(35.18, 39.22) * mm, "end": v(34.76, 39.8) * mm});
            skLineSegment(sketch, "E1967", {"start": v(34.76, 39.8) * mm, "end": v(34.5, 39.75) * mm});
            skLineSegment(sketch, "E1968", {"start": v(34.5, 39.75) * mm, "end": v(33.8, 39.68) * mm});
            skLineSegment(sketch, "E1969", {"start": v(33.8, 39.68) * mm, "end": v(32.8, 39.64) * mm});
            skLineSegment(sketch, "E1970", {"start": v(32.8, 39.64) * mm, "end": v(31.63, 39.68) * mm});
            skLineSegment(sketch, "E1971", {"start": v(31.63, 39.68) * mm, "end": v(29.4, 40.05) * mm});
            skLineSegment(sketch, "E1972", {"start": v(29.4, 40.05) * mm, "end": v(28.37, 40.35) * mm});
            skLineSegment(sketch, "E1973", {"start": v(28.37, 40.35) * mm, "end": v(28.3, 40.56) * mm});
            skLineSegment(sketch, "E1974", {"start": v(28.3, 40.56) * mm, "end": v(28.11, 41.13) * mm});
            skLineSegment(sketch, "E1975", {"start": v(28.11, 41.13) * mm, "end": v(27.8, 42.4) * mm});
            skLineSegment(sketch, "E1976", {"start": v(27.8, 42.4) * mm, "end": v(27.57, 43.83) * mm});
            skLineSegment(sketch, "E1977", {"start": v(27.57, 43.83) * mm, "end": v(27.5, 45.25) * mm});
            skLineSegment(sketch, "E1978", {"start": v(27.5, 45.25) * mm, "end": v(27.49, 45.48) * mm});
            skLineSegment(sketch, "E1979", {"start": v(27.49, 45.48) * mm, "end": v(28.37, 46.03) * mm});
            skLineSegment(sketch, "E1980", {"start": v(28.37, 46.03) * mm, "end": v(29.27, 46.52) * mm});
            skLineSegment(sketch, "E1981", {"start": v(29.27, 46.52) * mm, "end": v(29.78, 46.77) * mm});
            skLineSegment(sketch, "E1982", {"start": v(29.78, 46.77) * mm, "end": v(30.33, 47) * mm});
            skLineSegment(sketch, "E1983", {"start": v(30.33, 47) * mm, "end": v(32.34, 47.66) * mm});
            skLineSegment(sketch, "E1984", {"start": v(32.34, 47.66) * mm, "end": v(33.27, 47.84) * mm});
            skLineSegment(sketch, "E1985", {"start": v(33.27, 47.84) * mm, "end": v(33.42, 48.4) * mm});
            skLineSegment(sketch, "E1986", {"start": v(33.42, 48.4) * mm, "end": v(33.74, 49.27) * mm});
            skLineSegment(sketch, "E1987", {"start": v(33.74, 49.27) * mm, "end": v(34.2, 50.2) * mm});
            skLineSegment(sketch, "E1988", {"start": v(34.2, 50.2) * mm, "end": v(34.63, 50.9) * mm});
            skLineSegment(sketch, "E1989", {"start": v(34.63, 50.9) * mm, "end": v(34.9, 51.28) * mm});
            skLineSegment(sketch, "E1990", {"start": v(34.9, 51.28) * mm, "end": v(34.5, 52.16) * mm});
            skLineSegment(sketch, "E1991", {"start": v(34.5, 52.16) * mm, "end": v(33.84, 54.23) * mm});
            skLineSegment(sketch, "E1992", {"start": v(33.84, 54.23) * mm, "end": v(33.5, 56.47) * mm});
            skLineSegment(sketch, "E1993", {"start": v(33.5, 56.47) * mm, "end": v(33.47, 57.24) * mm});
            skLineSegment(sketch, "E1994", {"start": v(33.47, 57.24) * mm, "end": v(33.47, 57.53) * mm});
            skLineSegment(sketch, "E1995", {"start": v(33.47, 57.53) * mm, "end": v(34.12, 58.02) * mm});
            skLineSegment(sketch, "E1996", {"start": v(34.12, 58.02) * mm, "end": v(34.83, 58.47) * mm});
            skLineSegment(sketch, "E1997", {"start": v(34.83, 58.47) * mm, "end": v(35.66, 58.94) * mm});
            skLineSegment(sketch, "E1998", {"start": v(35.66, 58.94) * mm, "end": v(37.3, 59.68) * mm});
            skLineSegment(sketch, "E1999", {"start": v(37.3, 59.68) * mm, "end": v(38.07, 59.96) * mm});
            skLineSegment(sketch, "E2000", {"start": v(38.07, 59.96) * mm, "end": v(38.3, 59.79) * mm});
            skLineSegment(sketch, "E2001", {"start": v(38.3, 59.79) * mm, "end": v(38.86, 59.3) * mm});
            skLineSegment(sketch, "E2002", {"start": v(38.86, 59.3) * mm, "end": v(40.4, 57.73) * mm});
            skLineSegment(sketch, "E2003", {"start": v(40.4, 57.73) * mm, "end": v(41.64, 56.02) * mm});
            skLineSegment(sketch, "E2004", {"start": v(41.64, 56.02) * mm, "end": v(42.1, 55.19) * mm});
            skLineSegment(sketch, "E2005", {"start": v(42.1, 55.19) * mm, "end": v(42.68, 55.22) * mm});
            skLineSegment(sketch, "E2006", {"start": v(42.68, 55.22) * mm, "end": v(43.28, 55.2) * mm});
            skLineSegment(sketch, "E2007", {"start": v(43.28, 55.2) * mm, "end": v(43.96, 55.14) * mm});
            skLineSegment(sketch, "E2008", {"start": v(43.96, 55.14) * mm, "end": v(44.64, 55.04) * mm});
            skLineSegment(sketch, "E2009", {"start": v(44.64, 55.04) * mm, "end": v(45.62, 54.8) * mm});
            skLineSegment(sketch, "E2010", {"start": v(45.62, 54.8) * mm, "end": v(45.77, 54.74) * mm});
            skLineSegment(sketch, "E2011", {"start": v(45.77, 54.74) * mm, "end": v(45.89, 54.7) * mm});
            skLineSegment(sketch, "E2012", {"start": v(45.89, 54.7) * mm, "end": v(46.6, 55.35) * mm});
            skLineSegment(sketch, "E2013", {"start": v(46.6, 55.35) * mm, "end": v(48.35, 56.62) * mm});
            skLineSegment(sketch, "E2014", {"start": v(48.35, 56.62) * mm, "end": v(50.39, 57.63) * mm});
            skLineSegment(sketch, "E2015", {"start": v(50.39, 57.63) * mm, "end": v(51.11, 57.91) * mm});
            skLineSegment(sketch, "E2016", {"start": v(51.11, 57.91) * mm, "end": v(51.4, 58) * mm});
            skLineSegment(sketch, "E2017", {"start": v(51.4, 58) * mm, "end": v(52.05, 57.51) * mm});
            skLineSegment(sketch, "E2018", {"start": v(52.05, 57.51) * mm, "end": v(53.4, 56.34) * mm});
            skLineSegment(sketch, "E2019", {"start": v(53.4, 56.34) * mm, "end": v(54.06, 55.65) * mm});
            skLineSegment(sketch, "E2020", {"start": v(54.06, 55.65) * mm, "end": v(54.61, 55.02) * mm});
            skLineSegment(sketch, "E2021", {"start": v(54.61, 55.02) * mm, "end": v(55.1, 54.37) * mm});
            skLineSegment(sketch, "E2022", {"start": v(55.1, 54.37) * mm, "end": v(55, 54.1) * mm});
            skLineSegment(sketch, "E2023", {"start": v(55, 54.1) * mm, "end": v(54.73, 53.42) * mm});
            skLineSegment(sketch, "E2024", {"start": v(54.73, 53.42) * mm, "end": v(53.72, 51.47) * mm});
            skLineSegment(sketch, "E2025", {"start": v(53.72, 51.47) * mm, "end": v(52.47, 49.76) * mm});
            skLineSegment(sketch, "E2026", {"start": v(52.47, 49.76) * mm, "end": v(52.01, 49.25) * mm});
            skLineSegment(sketch, "E2027", {"start": v(52.01, 49.25) * mm, "end": v(51.83, 49.06) * mm});
            skLineSegment(sketch, "E2028", {"start": v(51.83, 49.06) * mm, "end": v(52.03, 48.52) * mm});
            skLineSegment(sketch, "E2029", {"start": v(52.03, 48.52) * mm, "end": v(52.2, 47.95) * mm});
            skLineSegment(sketch, "E2030", {"start": v(52.2, 47.95) * mm, "end": v(52.35, 47.29) * mm});
            skLineSegment(sketch, "E2031", {"start": v(52.35, 47.29) * mm, "end": v(52.5, 46.02) * mm});
            skLineSegment(sketch, "E2032", {"start": v(52.5, 46.02) * mm, "end": v(52.54, 45.44) * mm});
            skLineSegment(sketch, "E2033", {"start": v(52.54, 45.44) * mm, "end": v(52.53, 45.31) * mm});
            skLineSegment(sketch, "E2034", {"start": v(42.43, 46.1) * mm, "end": v(41.7, 45.8) * mm});
            skLineSegment(sketch, "E2035", {"start": v(41.7, 45.8) * mm, "end": v(41.4, 45.07) * mm});
            skLineSegment(sketch, "E2036", {"start": v(41.4, 45.07) * mm, "end": v(41.7, 44.34) * mm});
            skLineSegment(sketch, "E2037", {"start": v(41.7, 44.34) * mm, "end": v(42.43, 44.04) * mm});
            skLineSegment(sketch, "E2038", {"start": v(42.43, 44.04) * mm, "end": v(43.16, 44.34) * mm});
            skLineSegment(sketch, "E2039", {"start": v(43.16, 44.34) * mm, "end": v(43.46, 45.07) * mm});
            skLineSegment(sketch, "E2040", {"start": v(43.46, 45.07) * mm, "end": v(43.16, 45.8) * mm});
            skLineSegment(sketch, "E2041", {"start": v(43.16, 45.8) * mm, "end": v(42.43, 46.1) * mm});
            skSolve(sketch);
        }
        {
            var Q0;
            Q0=makeQuery(id+"F2.imprint","IMPRINT",FACE,{"disambiguationData":[TD([[makeQuery(id+"F2.imprint","IMPRINT",EDGE,{"derivedFrom":sQuery(id+"F2.wireOp",EDGE,"E1001")}),-1.0]])]});
            extrude(context, id + "F3", {"entities" : qUnion([Q0]), "depth" : 4 * mm});
        }
        {
            var Q0;
            Q0=makeQuery(id+"F2.imprint","IMPRINT",FACE,{"disambiguationData":[TD([[makeQuery(id+"F2.imprint","IMPRINT",EDGE,{"derivedFrom":sQuery(id+"F2.wireOp",EDGE,"E1528")}),-1.0]])]});
            extrude(context, id + "F4", {"entities" : qUnion([Q0]), "depth" : 4 * mm});
        }
        {
            var Q0;
            Q0=makeQuery(id+"F2.imprint","IMPRINT",FACE,{"disambiguationData":[TD([[makeQuery(id+"F2.imprint","IMPRINT",EDGE,{"derivedFrom":sQuery(id+"F2.wireOp",EDGE,"E1757")}),-1.0]])]});
            extrude(context, id + "F5", {"entities" : qUnion([Q0]), "depth" : 4 * mm});
        }
        {
            var Q0;
            Q0=makeQuery(id+"F2.imprint","IMPRINT",FACE,{"disambiguationData":[TD([[makeQuery(id+"F2.imprint","IMPRINT",EDGE,{"derivedFrom":sQuery(id+"F2.wireOp",EDGE,"E1924")}),-1.0]])]});
            extrude(context, id + "F6", {"entities" : qUnion([Q0]), "depth" : 4 * mm});
        }
        {
            var Q0;
            Q0=makeQuery(id+"F2.imprint","IMPRINT",FACE,{"disambiguationData":[TD([[makeQuery(id+"F2.imprint","IMPRINT",EDGE,{"derivedFrom":sQuery(id+"F2.wireOp",EDGE,"E1278")}),-1.0]])]});
            extrude(context, id + "F7", {"entities" : qUnion([Q0]), "depth" : 4 * mm});
        }
        {
            var Q0;
            Q0=qCreatedBy(makeId("Top.planeOp"),FACE);
            var sketch = newSketch(context, id + "F8", { "sketchPlane" : qUnion([Q0])});
            skCircle(sketch, "E2042", {"center": v(-28.31, -18.63) * mm, "radius": 0.94 * mm});
            skCircle(sketch, "E2043", {"center": v(42.46, 45.07) * mm, "radius": 0.95 * mm});
            skCircle(sketch, "E2044", {"center": v(-1.53, 91.28) * mm, "radius": 1.08 * mm});
            skCircle(sketch, "E2045", {"center": v(55.68, 69.79) * mm, "radius": 7.76 * mm});
            skCircle(sketch, "E2046", {"center": v(61.52, -35.11) * mm, "radius": 0.97 * mm});
            skCircle(sketch, "E2047", {"center": v(29.73, -103.62) * mm, "radius": 0.91 * mm});
            skSolve(sketch);
        }
        {
            var Q0;
            Q0=makeQuery(id+"F8.imprint","IMPRINT",FACE,{"disambiguationData":[TD([[makeQuery(id+"F8.imprint","IMPRINT",EDGE,{"derivedFrom":sQuery(id+"F8.wireOp",EDGE,"E2047")}),1.0]])]});
            var Q1;
            Q1=makeQuery(id+"F8.imprint","IMPRINT",FACE,{"disambiguationData":[TD([[makeQuery(id+"F8.imprint","IMPRINT",EDGE,{"derivedFrom":sQuery(id+"F8.wireOp",EDGE,"E2046")}),1.0]])]});
            var Q2;
            Q2=makeQuery(id+"F8.imprint","IMPRINT",FACE,{"disambiguationData":[TD([[makeQuery(id+"F8.imprint","IMPRINT",EDGE,{"derivedFrom":sQuery(id+"F8.wireOp",EDGE,"E2043")}),1.0]])]});
            var Q3;
            Q3=makeQuery(id+"F8.imprint","IMPRINT",FACE,{"disambiguationData":[TD([[makeQuery(id+"F8.imprint","IMPRINT",EDGE,{"derivedFrom":sQuery(id+"F8.wireOp",EDGE,"E2042")}),1.0]])]});
            var Q4;
            Q4=makeQuery(id+"F8.imprint","IMPRINT",FACE,{"disambiguationData":[TD([[makeQuery(id+"F8.imprint","IMPRINT",EDGE,{"derivedFrom":sQuery(id+"F8.wireOp",EDGE,"E2044")}),1.0]])]});
            extrude(context, id + "F9", {"entities" : qUnion([Q0, Q1, Q2, Q3, Q4]), "depth" : 25.4 * mm});
        }
    });
